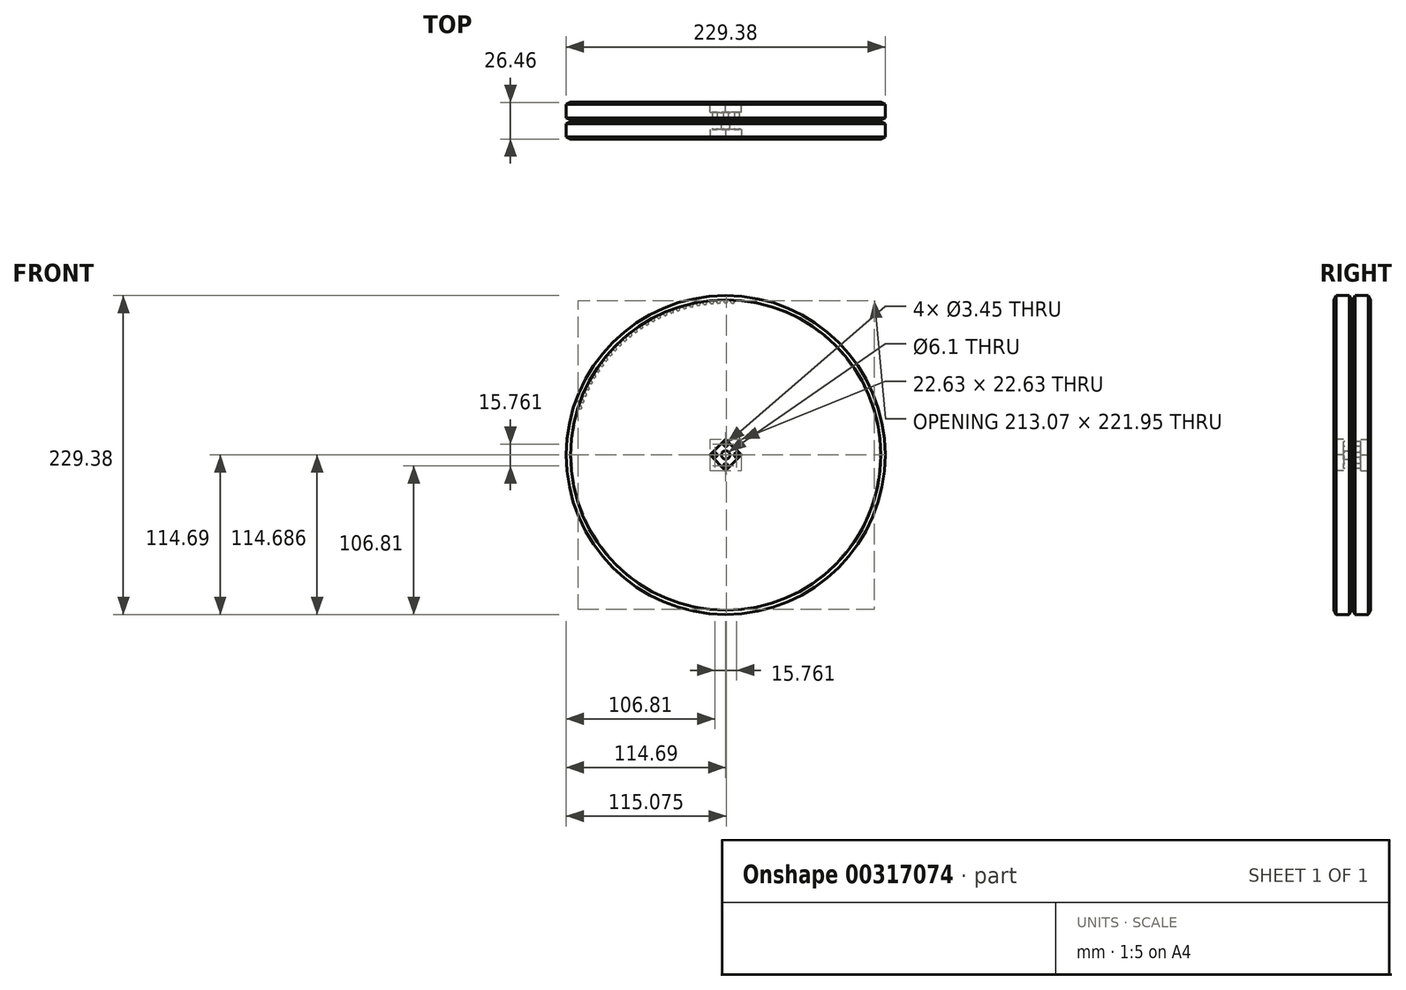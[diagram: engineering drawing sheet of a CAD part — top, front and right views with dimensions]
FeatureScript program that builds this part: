
annotation { "Feature Type Name" : "Feature", "Feature Type Description" : "" }
export const myFeature = defineFeature(function(context is Context, id is Id, definition is map)
    precondition{}
    {
        {
            var Q0;
            Q0=qCreatedBy(makeId("Front.planeOp"),FACE);
            var sketch = newSketch(context, id + "F0", { "sketchPlane" : qUnion([Q0])});
            skArc(sketch, "E0", {"start": v(-1.98, 110.97) * mm, "mid": v(-2.5, 110.96) * mm, "end": v(-3, 110.95) * mm});
            skArc(sketch, "E1", {"start": v(0.5, 109.19) * mm, "mid": v(0, 109.19) * mm, "end": v(-0.5, 109.19) * mm});
            skLineSegment(sketch, "E2", {"start": v(0, 0) * mm, "end": v(0, 109.19) * mm, "construction": true});
            skLineSegment(sketch, "E3", {"start": v(0.86, 109.42) * mm, "end": v(1.42, 110.62) * mm});
            skLineSegment(sketch, "E4", {"start": v(-0.86, 109.42) * mm, "end": v(-1.42, 110.62) * mm});
            skLineSegment(sketch, "E5", {"start": v(0, 109.19) * mm, "end": v(0, 110.99) * mm, "construction": true});
            skPoint(sketch, "E6.visualSharp", {"position": v(-1.59, 110.98) * mm});
            skArc(sketch, "E6.filletArc", {"start": v(-1.42, 110.62) * mm, "mid": v(-1.65, 110.88) * mm, "end": v(-1.98, 110.97) * mm});
            skPoint(sketch, "E7.visualSharp", {"position": v(1.59, 110.98) * mm});
            skArc(sketch, "E7.filletArc", {"start": v(1.98, 110.97) * mm, "mid": v(1.65, 110.88) * mm, "end": v(1.42, 110.62) * mm});
            skPoint(sketch, "E8.visualSharp", {"position": v(-0.75, 109.19) * mm});
            skArc(sketch, "E8.filletArc", {"start": v(-0.86, 109.42) * mm, "mid": v(-0.71, 109.25) * mm, "end": v(-0.5, 109.19) * mm});
            skPoint(sketch, "E9.visualSharp", {"position": v(0.75, 109.19) * mm});
            skArc(sketch, "E9.filletArc", {"start": v(0.5, 109.19) * mm, "mid": v(0.71, 109.25) * mm, "end": v(0.86, 109.42) * mm});
            skLineSegment(sketch, "E10.1.0", {"start": v(-4.9, 109.08) * mm, "end": v(-4.98, 110.88) * mm, "construction": true});
            skLineSegment(sketch, "E10.1.1", {"start": v(-5.77, 109.27) * mm, "end": v(-6.38, 110.45) * mm});
            skPoint(sketch, "E10.1.2", {"position": v(-6.56, 110.8) * mm});
            skPoint(sketch, "E10.1.3", {"position": v(-4.15, 109.1) * mm});
            skPoint(sketch, "E10.1.4", {"position": v(-5.65, 109.04) * mm});
            skPoint(sketch, "E10.1.5", {"position": v(-3.4, 110.94) * mm});
            skLineSegment(sketch, "E10.1.6", {"start": v(-4.05, 109.35) * mm, "end": v(-3.54, 110.58) * mm});
            skArc(sketch, "E10.1.7", {"start": v(-6.38, 110.45) * mm, "mid": v(-6.62, 110.7) * mm, "end": v(-6.95, 110.77) * mm});
            skArc(sketch, "E10.1.8", {"start": v(-3, 110.95) * mm, "mid": v(-3.33, 110.84) * mm, "end": v(-3.54, 110.58) * mm});
            skArc(sketch, "E10.1.9", {"start": v(-4.4, 109.1) * mm, "mid": v(-4.9, 109.08) * mm, "end": v(-5.4, 109.06) * mm});
            skArc(sketch, "E10.1.10", {"start": v(-4.4, 109.1) * mm, "mid": v(-4.2, 109.17) * mm, "end": v(-4.05, 109.35) * mm});
            skArc(sketch, "E10.1.11", {"start": v(-5.77, 109.27) * mm, "mid": v(-5.61, 109.1) * mm, "end": v(-5.4, 109.06) * mm});
            skLineSegment(sketch, "E10.2.0", {"start": v(-9.79, 108.75) * mm, "end": v(-9.95, 110.54) * mm, "construction": true});
            skLineSegment(sketch, "E10.2.1", {"start": v(-10.66, 108.9) * mm, "end": v(-11.33, 110.05) * mm});
            skPoint(sketch, "E10.2.2", {"position": v(-11.53, 110.39) * mm});
            skPoint(sketch, "E10.2.3", {"position": v(-9.04, 108.81) * mm});
            skPoint(sketch, "E10.2.4", {"position": v(-10.53, 108.68) * mm});
            skPoint(sketch, "E10.2.5", {"position": v(-8.37, 110.67) * mm});
            skLineSegment(sketch, "E10.2.6", {"start": v(-8.95, 109.05) * mm, "end": v(-8.5, 110.3) * mm});
            skArc(sketch, "E10.2.7", {"start": v(-11.33, 110.05) * mm, "mid": v(-11.58, 110.29) * mm, "end": v(-11.91, 110.35) * mm});
            skArc(sketch, "E10.2.8", {"start": v(-7.98, 110.7) * mm, "mid": v(-8.3, 110.58) * mm, "end": v(-8.5, 110.3) * mm});
            skArc(sketch, "E10.2.9", {"start": v(-9.3, 108.8) * mm, "mid": v(-9.79, 108.75) * mm, "end": v(-10.28, 108.7) * mm});
            skArc(sketch, "E10.2.10", {"start": v(-9.3, 108.8) * mm, "mid": v(-9.09, 108.87) * mm, "end": v(-8.95, 109.05) * mm});
            skArc(sketch, "E10.2.11", {"start": v(-10.66, 108.9) * mm, "mid": v(-10.5, 108.75) * mm, "end": v(-10.28, 108.7) * mm});
            skLineSegment(sketch, "E10.3.0", {"start": v(-14.66, 108.2) * mm, "end": v(-14.9, 109.98) * mm, "construction": true});
            skLineSegment(sketch, "E10.3.1", {"start": v(-15.54, 108.31) * mm, "end": v(-16.26, 109.43) * mm});
            skPoint(sketch, "E10.3.2", {"position": v(-16.47, 109.76) * mm});
            skPoint(sketch, "E10.3.3", {"position": v(-13.91, 108.3) * mm});
            skPoint(sketch, "E10.3.4", {"position": v(-15.4, 108.1) * mm});
            skPoint(sketch, "E10.3.5", {"position": v(-13.33, 110.19) * mm});
            skLineSegment(sketch, "E10.3.6", {"start": v(-13.84, 108.54) * mm, "end": v(-13.44, 109.81) * mm});
            skArc(sketch, "E10.3.7", {"start": v(-16.26, 109.43) * mm, "mid": v(-16.52, 109.66) * mm, "end": v(-16.85, 109.7) * mm});
            skArc(sketch, "E10.3.8", {"start": v(-12.94, 110.23) * mm, "mid": v(-13.25, 110.1) * mm, "end": v(-13.44, 109.81) * mm});
            skArc(sketch, "E10.3.9", {"start": v(-14.17, 108.27) * mm, "mid": v(-14.66, 108.2) * mm, "end": v(-15.15, 108.13) * mm});
            skArc(sketch, "E10.3.10", {"start": v(-14.17, 108.27) * mm, "mid": v(-13.96, 108.36) * mm, "end": v(-13.84, 108.54) * mm});
            skArc(sketch, "E10.3.11", {"start": v(-15.54, 108.31) * mm, "mid": v(-15.37, 108.17) * mm, "end": v(-15.15, 108.13) * mm});
            skLineSegment(sketch, "E10.4.0", {"start": v(-19.5, 107.43) * mm, "end": v(-19.82, 109.2) * mm, "construction": true});
            skLineSegment(sketch, "E10.4.1", {"start": v(-20.38, 107.5) * mm, "end": v(-21.15, 108.6) * mm});
            skPoint(sketch, "E10.4.2", {"position": v(-21.38, 108.91) * mm});
            skPoint(sketch, "E10.4.3", {"position": v(-18.76, 107.57) * mm});
            skPoint(sketch, "E10.4.4", {"position": v(-20.23, 107.3) * mm});
            skPoint(sketch, "E10.4.5", {"position": v(-18.26, 109.48) * mm});
            skLineSegment(sketch, "E10.4.6", {"start": v(-18.7, 107.81) * mm, "end": v(-18.35, 109.1) * mm});
            skArc(sketch, "E10.4.7", {"start": v(-21.15, 108.6) * mm, "mid": v(-21.42, 108.8) * mm, "end": v(-21.76, 108.83) * mm});
            skArc(sketch, "E10.4.8", {"start": v(-17.87, 109.54) * mm, "mid": v(-18.18, 109.4) * mm, "end": v(-18.35, 109.1) * mm});
            skArc(sketch, "E10.4.9", {"start": v(-19.01, 107.52) * mm, "mid": v(-19.5, 107.43) * mm, "end": v(-19.98, 107.34) * mm});
            skArc(sketch, "E10.4.10", {"start": v(-19.01, 107.52) * mm, "mid": v(-18.8, 107.62) * mm, "end": v(-18.7, 107.81) * mm});
            skArc(sketch, "E10.4.11", {"start": v(-20.38, 107.5) * mm, "mid": v(-20.2, 107.37) * mm, "end": v(-19.98, 107.34) * mm});
            skLineSegment(sketch, "E10.5.0", {"start": v(-24.3, 106.45) * mm, "end": v(-24.7, 108.2) * mm, "construction": true});
            skLineSegment(sketch, "E10.5.1", {"start": v(-25.18, 106.48) * mm, "end": v(-26, 107.53) * mm});
            skPoint(sketch, "E10.5.2", {"position": v(-26.24, 107.84) * mm});
            skPoint(sketch, "E10.5.3", {"position": v(-23.56, 106.62) * mm});
            skPoint(sketch, "E10.5.4", {"position": v(-25.03, 106.28) * mm});
            skPoint(sketch, "E10.5.5", {"position": v(-23.15, 108.55) * mm});
            skLineSegment(sketch, "E10.5.6", {"start": v(-23.51, 106.87) * mm, "end": v(-23.23, 108.17) * mm});
            skArc(sketch, "E10.5.7", {"start": v(-26, 107.53) * mm, "mid": v(-26.28, 107.73) * mm, "end": v(-26.62, 107.75) * mm});
            skArc(sketch, "E10.5.8", {"start": v(-22.77, 108.63) * mm, "mid": v(-23.07, 108.47) * mm, "end": v(-23.23, 108.17) * mm});
            skArc(sketch, "E10.5.9", {"start": v(-23.81, 106.56) * mm, "mid": v(-24.3, 106.45) * mm, "end": v(-24.78, 106.34) * mm});
            skArc(sketch, "E10.5.10", {"start": v(-23.81, 106.56) * mm, "mid": v(-23.62, 106.67) * mm, "end": v(-23.51, 106.87) * mm});
            skArc(sketch, "E10.5.11", {"start": v(-25.18, 106.48) * mm, "mid": v(-25, 106.35) * mm, "end": v(-24.78, 106.34) * mm});
            skLineSegment(sketch, "E10.6.0", {"start": v(-29.05, 105.25) * mm, "end": v(-29.53, 106.99) * mm, "construction": true});
            skLineSegment(sketch, "E10.6.1", {"start": v(-29.94, 105.25) * mm, "end": v(-30.8, 106.26) * mm});
            skPoint(sketch, "E10.6.2", {"position": v(-31.05, 106.56) * mm});
            skPoint(sketch, "E10.6.3", {"position": v(-28.32, 105.45) * mm});
            skPoint(sketch, "E10.6.4", {"position": v(-29.77, 105.05) * mm});
            skPoint(sketch, "E10.6.5", {"position": v(-28, 107.4) * mm});
            skLineSegment(sketch, "E10.6.6", {"start": v(-28.28, 105.7) * mm, "end": v(-28.06, 107.02) * mm});
            skArc(sketch, "E10.6.7", {"start": v(-30.8, 106.26) * mm, "mid": v(-31.09, 106.45) * mm, "end": v(-31.43, 106.45) * mm});
            skArc(sketch, "E10.6.8", {"start": v(-27.62, 107.5) * mm, "mid": v(-27.91, 107.32) * mm, "end": v(-28.06, 107.02) * mm});
            skArc(sketch, "E10.6.9", {"start": v(-28.57, 105.38) * mm, "mid": v(-29.05, 105.25) * mm, "end": v(-29.52, 105.12) * mm});
            skArc(sketch, "E10.6.10", {"start": v(-28.57, 105.38) * mm, "mid": v(-28.38, 105.5) * mm, "end": v(-28.28, 105.7) * mm});
            skArc(sketch, "E10.6.11", {"start": v(-29.94, 105.25) * mm, "mid": v(-29.75, 105.12) * mm, "end": v(-29.52, 105.12) * mm});
            skLineSegment(sketch, "E10.7.0", {"start": v(-33.74, 103.84) * mm, "end": v(-34.3, 105.56) * mm, "construction": true});
            skLineSegment(sketch, "E10.7.1", {"start": v(-34.63, 103.8) * mm, "end": v(-35.54, 104.77) * mm});
            skPoint(sketch, "E10.7.2", {"position": v(-35.8, 105.06) * mm});
            skPoint(sketch, "E10.7.3", {"position": v(-33.03, 104.07) * mm});
            skPoint(sketch, "E10.7.4", {"position": v(-34.45, 103.61) * mm});
            skPoint(sketch, "E10.7.5", {"position": v(-32.79, 106.04) * mm});
            skLineSegment(sketch, "E10.7.6", {"start": v(-33, 104.33) * mm, "end": v(-32.83, 105.65) * mm});
            skArc(sketch, "E10.7.7", {"start": v(-35.54, 104.77) * mm, "mid": v(-35.83, 104.94) * mm, "end": v(-36.17, 104.93) * mm});
            skArc(sketch, "E10.7.8", {"start": v(-32.41, 106.15) * mm, "mid": v(-32.7, 105.96) * mm, "end": v(-32.83, 105.65) * mm});
            skArc(sketch, "E10.7.9", {"start": v(-33.27, 104) * mm, "mid": v(-33.74, 103.84) * mm, "end": v(-34.21, 103.7) * mm});
            skArc(sketch, "E10.7.10", {"start": v(-33.27, 104) * mm, "mid": v(-33.08, 104.12) * mm, "end": v(-33, 104.33) * mm});
            skArc(sketch, "E10.7.11", {"start": v(-34.63, 103.8) * mm, "mid": v(-34.44, 103.68) * mm, "end": v(-34.21, 103.7) * mm});
            skLineSegment(sketch, "E10.8.0", {"start": v(-38.37, 102.23) * mm, "end": v(-39, 103.91) * mm, "construction": true});
            skLineSegment(sketch, "E10.8.1", {"start": v(-39.25, 102.14) * mm, "end": v(-40.2, 103.07) * mm});
            skPoint(sketch, "E10.8.2", {"position": v(-40.48, 103.34) * mm});
            skPoint(sketch, "E10.8.3", {"position": v(-37.66, 102.49) * mm});
            skPoint(sketch, "E10.8.4", {"position": v(-39.07, 101.96) * mm});
            skPoint(sketch, "E10.8.5", {"position": v(-37.51, 104.46) * mm});
            skLineSegment(sketch, "E10.8.6", {"start": v(-37.64, 102.74) * mm, "end": v(-37.54, 104.07) * mm});
            skArc(sketch, "E10.8.7", {"start": v(-40.2, 103.07) * mm, "mid": v(-40.5, 103.23) * mm, "end": v(-40.84, 103.2) * mm});
            skArc(sketch, "E10.8.8", {"start": v(-37.14, 104.59) * mm, "mid": v(-37.42, 104.39) * mm, "end": v(-37.54, 104.07) * mm});
            skArc(sketch, "E10.8.9", {"start": v(-37.9, 102.4) * mm, "mid": v(-38.37, 102.23) * mm, "end": v(-38.83, 102.05) * mm});
            skArc(sketch, "E10.8.10", {"start": v(-37.9, 102.4) * mm, "mid": v(-37.72, 102.53) * mm, "end": v(-37.64, 102.74) * mm});
            skArc(sketch, "E10.8.11", {"start": v(-39.25, 102.14) * mm, "mid": v(-39.05, 102.03) * mm, "end": v(-38.83, 102.05) * mm});
            skLineSegment(sketch, "E10.9.0", {"start": v(-42.91, 100.4) * mm, "end": v(-43.62, 102.06) * mm, "construction": true});
            skLineSegment(sketch, "E10.9.1", {"start": v(-43.8, 100.28) * mm, "end": v(-44.78, 101.16) * mm});
            skPoint(sketch, "E10.9.2", {"position": v(-45.07, 101.42) * mm});
            skPoint(sketch, "E10.9.3", {"position": v(-42.22, 100.7) * mm});
            skPoint(sketch, "E10.9.4", {"position": v(-43.6, 100.1) * mm});
            skPoint(sketch, "E10.9.5", {"position": v(-42.16, 102.67) * mm});
            skLineSegment(sketch, "E10.9.6", {"start": v(-42.21, 100.95) * mm, "end": v(-42.17, 102.28) * mm});
            skArc(sketch, "E10.9.7", {"start": v(-44.78, 101.16) * mm, "mid": v(-45.1, 101.3) * mm, "end": v(-45.43, 101.26) * mm});
            skArc(sketch, "E10.9.8", {"start": v(-41.8, 102.82) * mm, "mid": v(-42.06, 102.6) * mm, "end": v(-42.17, 102.28) * mm});
            skArc(sketch, "E10.9.9", {"start": v(-42.46, 100.6) * mm, "mid": v(-42.91, 100.4) * mm, "end": v(-43.37, 100.2) * mm});
            skArc(sketch, "E10.9.10", {"start": v(-42.46, 100.6) * mm, "mid": v(-42.28, 100.74) * mm, "end": v(-42.21, 100.95) * mm});
            skArc(sketch, "E10.9.11", {"start": v(-43.8, 100.28) * mm, "mid": v(-43.6, 100.18) * mm, "end": v(-43.37, 100.2) * mm});
            skLineSegment(sketch, "E10.10.0", {"start": v(-47.38, 98.38) * mm, "end": v(-48.16, 100) * mm, "construction": true});
            skLineSegment(sketch, "E10.10.1", {"start": v(-48.25, 98.21) * mm, "end": v(-49.28, 99.05) * mm});
            skPoint(sketch, "E10.10.2", {"position": v(-49.58, 99.3) * mm});
            skPoint(sketch, "E10.10.3", {"position": v(-46.7, 98.7) * mm});
            skPoint(sketch, "E10.10.4", {"position": v(-48.05, 98.05) * mm});
            skPoint(sketch, "E10.10.5", {"position": v(-46.72, 100.67) * mm});
            skLineSegment(sketch, "E10.10.6", {"start": v(-46.7, 98.95) * mm, "end": v(-46.72, 100.29) * mm});
            skArc(sketch, "E10.10.7", {"start": v(-49.28, 99.05) * mm, "mid": v(-49.6, 99.18) * mm, "end": v(-49.93, 99.12) * mm});
            skArc(sketch, "E10.10.8", {"start": v(-46.37, 100.84) * mm, "mid": v(-46.63, 100.61) * mm, "end": v(-46.72, 100.29) * mm});
            skArc(sketch, "E10.10.9", {"start": v(-46.93, 98.59) * mm, "mid": v(-47.38, 98.38) * mm, "end": v(-47.82, 98.16) * mm});
            skArc(sketch, "E10.10.10", {"start": v(-46.93, 98.59) * mm, "mid": v(-46.76, 98.74) * mm, "end": v(-46.7, 98.95) * mm});
            skArc(sketch, "E10.10.11", {"start": v(-48.25, 98.21) * mm, "mid": v(-48.04, 98.12) * mm, "end": v(-47.82, 98.16) * mm});
            skLineSegment(sketch, "E10.11.0", {"start": v(-51.74, 96.15) * mm, "end": v(-52.6, 97.74) * mm, "construction": true});
            skLineSegment(sketch, "E10.11.1", {"start": v(-52.6, 95.95) * mm, "end": v(-53.67, 96.74) * mm});
            skPoint(sketch, "E10.11.2", {"position": v(-53.98, 96.97) * mm});
            skPoint(sketch, "E10.11.3", {"position": v(-51.08, 96.5) * mm});
            skPoint(sketch, "E10.11.4", {"position": v(-52.4, 95.8) * mm});
            skPoint(sketch, "E10.11.5", {"position": v(-51.2, 98.48) * mm});
            skLineSegment(sketch, "E10.11.6", {"start": v(-51.1, 96.76) * mm, "end": v(-51.17, 98.09) * mm});
            skArc(sketch, "E10.11.7", {"start": v(-53.67, 96.74) * mm, "mid": v(-54, 96.86) * mm, "end": v(-54.33, 96.78) * mm});
            skArc(sketch, "E10.11.8", {"start": v(-50.85, 98.66) * mm, "mid": v(-51.1, 98.42) * mm, "end": v(-51.17, 98.09) * mm});
            skArc(sketch, "E10.11.9", {"start": v(-51.3, 96.38) * mm, "mid": v(-51.74, 96.15) * mm, "end": v(-52.18, 95.92) * mm});
            skArc(sketch, "E10.11.10", {"start": v(-51.3, 96.38) * mm, "mid": v(-51.14, 96.54) * mm, "end": v(-51.1, 96.76) * mm});
            skArc(sketch, "E10.11.11", {"start": v(-52.6, 95.95) * mm, "mid": v(-52.4, 95.87) * mm, "end": v(-52.18, 95.92) * mm});
            skLineSegment(sketch, "E10.12.0", {"start": v(-56, 93.73) * mm, "end": v(-56.93, 95.28) * mm, "construction": true});
            skLineSegment(sketch, "E10.12.1", {"start": v(-56.86, 93.49) * mm, "end": v(-57.96, 94.24) * mm});
            skPoint(sketch, "E10.12.2", {"position": v(-58.28, 94.46) * mm});
            skPoint(sketch, "E10.12.3", {"position": v(-55.36, 94.12) * mm});
            skPoint(sketch, "E10.12.4", {"position": v(-56.65, 93.35) * mm});
            skPoint(sketch, "E10.12.5", {"position": v(-55.56, 96.08) * mm});
            skLineSegment(sketch, "E10.12.6", {"start": v(-55.38, 94.37) * mm, "end": v(-55.52, 95.7) * mm});
            skArc(sketch, "E10.12.7", {"start": v(-57.96, 94.24) * mm, "mid": v(-58.28, 94.34) * mm, "end": v(-58.61, 94.25) * mm});
            skArc(sketch, "E10.12.8", {"start": v(-55.22, 96.28) * mm, "mid": v(-55.46, 96.03) * mm, "end": v(-55.52, 95.7) * mm});
            skArc(sketch, "E10.12.9", {"start": v(-55.58, 93.99) * mm, "mid": v(-56, 93.73) * mm, "end": v(-56.43, 93.48) * mm});
            skArc(sketch, "E10.12.10", {"start": v(-55.58, 93.99) * mm, "mid": v(-55.42, 94.15) * mm, "end": v(-55.38, 94.37) * mm});
            skArc(sketch, "E10.12.11", {"start": v(-56.86, 93.49) * mm, "mid": v(-56.64, 93.42) * mm, "end": v(-56.43, 93.48) * mm});
            skLineSegment(sketch, "E10.13.0", {"start": v(-60.15, 91.13) * mm, "end": v(-61.14, 92.63) * mm, "construction": true});
            skLineSegment(sketch, "E10.13.1", {"start": v(-61, 90.84) * mm, "end": v(-62.13, 91.54) * mm});
            skPoint(sketch, "E10.13.2", {"position": v(-62.46, 91.75) * mm});
            skPoint(sketch, "E10.13.3", {"position": v(-59.52, 91.54) * mm});
            skPoint(sketch, "E10.13.4", {"position": v(-60.78, 90.71) * mm});
            skPoint(sketch, "E10.13.5", {"position": v(-59.81, 93.5) * mm});
            skLineSegment(sketch, "E10.13.6", {"start": v(-59.56, 91.8) * mm, "end": v(-59.76, 93.1) * mm});
            skArc(sketch, "E10.13.7", {"start": v(-62.13, 91.54) * mm, "mid": v(-62.46, 91.63) * mm, "end": v(-62.78, 91.53) * mm});
            skArc(sketch, "E10.13.8", {"start": v(-59.49, 93.7) * mm, "mid": v(-59.7, 93.44) * mm, "end": v(-59.76, 93.1) * mm});
            skArc(sketch, "E10.13.9", {"start": v(-59.74, 91.4) * mm, "mid": v(-60.15, 91.13) * mm, "end": v(-60.56, 90.85) * mm});
            skArc(sketch, "E10.13.10", {"start": v(-59.74, 91.4) * mm, "mid": v(-59.6, 91.57) * mm, "end": v(-59.56, 91.8) * mm});
            skArc(sketch, "E10.13.11", {"start": v(-61, 90.84) * mm, "mid": v(-60.78, 90.79) * mm, "end": v(-60.56, 90.85) * mm});
            skLineSegment(sketch, "E10.14.0", {"start": v(-64.18, 88.34) * mm, "end": v(-65.24, 89.8) * mm, "construction": true});
            skLineSegment(sketch, "E10.14.1", {"start": v(-65, 88.02) * mm, "end": v(-66.17, 88.66) * mm});
            skPoint(sketch, "E10.14.2", {"position": v(-66.51, 88.85) * mm});
            skPoint(sketch, "E10.14.3", {"position": v(-63.57, 88.77) * mm});
            skPoint(sketch, "E10.14.4", {"position": v(-64.78, 87.9) * mm});
            skPoint(sketch, "E10.14.5", {"position": v(-63.95, 90.71) * mm});
            skLineSegment(sketch, "E10.14.6", {"start": v(-63.62, 89.03) * mm, "end": v(-63.87, 90.33) * mm});
            skArc(sketch, "E10.14.7", {"start": v(-66.17, 88.66) * mm, "mid": v(-66.5, 88.74) * mm, "end": v(-66.83, 88.62) * mm});
            skArc(sketch, "E10.14.8", {"start": v(-63.63, 90.94) * mm, "mid": v(-63.84, 90.67) * mm, "end": v(-63.87, 90.33) * mm});
            skArc(sketch, "E10.14.9", {"start": v(-63.78, 88.62) * mm, "mid": v(-64.18, 88.34) * mm, "end": v(-64.58, 88.04) * mm});
            skArc(sketch, "E10.14.10", {"start": v(-63.78, 88.62) * mm, "mid": v(-63.64, 88.8) * mm, "end": v(-63.62, 89.03) * mm});
            skArc(sketch, "E10.14.11", {"start": v(-65, 88.02) * mm, "mid": v(-64.79, 87.97) * mm, "end": v(-64.58, 88.04) * mm});
            skLineSegment(sketch, "E10.15.0", {"start": v(-68.08, 85.37) * mm, "end": v(-69.2, 86.77) * mm, "construction": true});
            skLineSegment(sketch, "E10.15.1", {"start": v(-68.9, 85.01) * mm, "end": v(-70.08, 85.6) * mm});
            skPoint(sketch, "E10.15.2", {"position": v(-70.43, 85.78) * mm});
            skPoint(sketch, "E10.15.3", {"position": v(-67.49, 85.83) * mm});
            skPoint(sketch, "E10.15.4", {"position": v(-68.66, 84.9) * mm});
            skPoint(sketch, "E10.15.5", {"position": v(-67.95, 87.75) * mm});
            skLineSegment(sketch, "E10.15.6", {"start": v(-67.55, 86.08) * mm, "end": v(-67.86, 87.38) * mm});
            skArc(sketch, "E10.15.7", {"start": v(-70.08, 85.6) * mm, "mid": v(-70.42, 85.66) * mm, "end": v(-70.73, 85.53) * mm});
            skArc(sketch, "E10.15.8", {"start": v(-67.64, 88) * mm, "mid": v(-67.85, 87.72) * mm, "end": v(-67.86, 87.38) * mm});
            skArc(sketch, "E10.15.9", {"start": v(-67.7, 85.67) * mm, "mid": v(-68.08, 85.37) * mm, "end": v(-68.46, 85.06) * mm});
            skArc(sketch, "E10.15.10", {"start": v(-67.7, 85.67) * mm, "mid": v(-67.56, 85.86) * mm, "end": v(-67.55, 86.08) * mm});
            skArc(sketch, "E10.15.11", {"start": v(-68.9, 85.01) * mm, "mid": v(-68.67, 84.97) * mm, "end": v(-68.46, 85.06) * mm});
            skArc(sketch, "E11.trimOffspring", {"start": v(3, 110.95) * mm, "mid": v(2.5, 110.96) * mm, "end": v(1.98, 110.97) * mm});
            skArc(sketch, "E12.trimOffspring", {"start": v(-66.83, 88.62) * mm, "mid": v(-67.24, 88.3) * mm, "end": v(-67.64, 88) * mm});
            skArc(sketch, "E13.trimOffspring", {"start": v(-62.78, 91.53) * mm, "mid": v(-63.2, 91.23) * mm, "end": v(-63.63, 90.94) * mm});
            skArc(sketch, "E14.trimOffspring", {"start": v(-58.61, 94.25) * mm, "mid": v(-59.05, 93.98) * mm, "end": v(-59.49, 93.7) * mm});
            skArc(sketch, "E15.trimOffspring", {"start": v(-54.33, 96.78) * mm, "mid": v(-54.77, 96.53) * mm, "end": v(-55.22, 96.28) * mm});
            skArc(sketch, "E16.trimOffspring", {"start": v(-49.93, 99.12) * mm, "mid": v(-50.39, 98.9) * mm, "end": v(-50.85, 98.66) * mm});
            skArc(sketch, "E17.trimOffspring", {"start": v(-45.43, 101.26) * mm, "mid": v(-45.9, 101.05) * mm, "end": v(-46.37, 100.84) * mm});
            skArc(sketch, "E18.trimOffspring", {"start": v(-40.84, 103.2) * mm, "mid": v(-41.32, 103.01) * mm, "end": v(-41.8, 102.82) * mm});
            skArc(sketch, "E19.trimOffspring", {"start": v(-36.17, 104.93) * mm, "mid": v(-36.66, 104.76) * mm, "end": v(-37.14, 104.59) * mm});
            skArc(sketch, "E20.trimOffspring", {"start": v(-31.43, 106.45) * mm, "mid": v(-31.92, 106.3) * mm, "end": v(-32.41, 106.15) * mm});
            skArc(sketch, "E21.trimOffspring", {"start": v(-26.62, 107.75) * mm, "mid": v(-27.12, 107.62) * mm, "end": v(-27.62, 107.5) * mm});
            skArc(sketch, "E22.trimOffspring", {"start": v(-21.76, 108.83) * mm, "mid": v(-22.26, 108.73) * mm, "end": v(-22.77, 108.63) * mm});
            skArc(sketch, "E23.trimOffspring", {"start": v(-16.85, 109.7) * mm, "mid": v(-17.36, 109.62) * mm, "end": v(-17.87, 109.54) * mm});
            skArc(sketch, "E24.trimOffspring", {"start": v(-11.91, 110.35) * mm, "mid": v(-12.43, 110.3) * mm, "end": v(-12.94, 110.23) * mm});
            skArc(sketch, "E25.trimOffspring", {"start": v(-6.95, 110.77) * mm, "mid": v(-7.47, 110.74) * mm, "end": v(-7.98, 110.7) * mm});
            skArc(sketch, "E26", {"start": v(-70.73, 85.53) * mm, "mid": v(-71.13, 85.2) * mm, "end": v(-71.52, 84.87) * mm, "construction": true});
            skCircle(sketch, "E27", {"center": v(0, 0) * mm, "radius": 109.19 * mm, "construction": true});
            skCircle(sketch, "E28", {"center": v(0, 0) * mm, "radius": 111.42 * mm, "construction": true});
            skLineSegment(sketch, "E29", {"start": v(0, 110.99) * mm, "end": v(0, 111.42) * mm, "construction": true});
            skLineSegment(sketch, "E30", {"start": v(4.98, 110.88) * mm, "end": v(5, 111.3) * mm, "construction": true});
            skLineSegment(sketch, "E31.3.16.0", {"start": v(-72.64, 81.84) * mm, "end": v(-73.85, 82.37) * mm});
            skPoint(sketch, "E31.6.16.0", {"position": v(-74.21, 82.53) * mm});
            skPoint(sketch, "E31.7.16.0", {"position": v(-71.27, 82.72) * mm});
            skPoint(sketch, "E31.8.16.0", {"position": v(-72.4, 81.73) * mm});
            skPoint(sketch, "E31.9.16.0", {"position": v(-71.82, 84.62) * mm});
            skLineSegment(sketch, "E31.10.16.0", {"start": v(-71.34, 82.96) * mm, "end": v(-71.71, 84.24) * mm});
            skArc(sketch, "E31.13.16.0", {"start": v(-73.85, 82.37) * mm, "mid": v(-74.2, 82.42) * mm, "end": v(-74.5, 82.27) * mm});
            skLineSegment(sketch, "E31.14.16.0", {"start": v(-71.84, 82.23) * mm, "end": v(-73.02, 83.58) * mm, "construction": true});
            skArc(sketch, "E31.17.16.0", {"start": v(-71.52, 84.87) * mm, "mid": v(-71.71, 84.58) * mm, "end": v(-71.71, 84.24) * mm});
            skArc(sketch, "E31.21.16.0", {"start": v(-71.47, 82.55) * mm, "mid": v(-71.84, 82.23) * mm, "end": v(-72.21, 81.9) * mm});
            skArc(sketch, "E31.25.16.0", {"start": v(-71.47, 82.55) * mm, "mid": v(-71.34, 82.74) * mm, "end": v(-71.34, 82.96) * mm});
            skArc(sketch, "E31.29.16.0", {"start": v(-72.64, 81.84) * mm, "mid": v(-72.41, 81.8) * mm, "end": v(-72.21, 81.9) * mm});
            skLineSegment(sketch, "E31.3.17.0", {"start": v(-76.24, 78.5) * mm, "end": v(-77.48, 78.98) * mm});
            skPoint(sketch, "E31.6.17.0", {"position": v(-77.84, 79.12) * mm});
            skPoint(sketch, "E31.7.17.0", {"position": v(-74.91, 79.44) * mm});
            skPoint(sketch, "E31.8.17.0", {"position": v(-76, 78.4) * mm});
            skPoint(sketch, "E31.9.17.0", {"position": v(-75.55, 81.3) * mm});
            skLineSegment(sketch, "E31.10.17.0", {"start": v(-75, 79.68) * mm, "end": v(-75.42, 80.94) * mm});
            skArc(sketch, "E31.13.17.0", {"start": v(-77.48, 78.98) * mm, "mid": v(-77.82, 79) * mm, "end": v(-78.12, 78.84) * mm});
            skLineSegment(sketch, "E31.14.17.0", {"start": v(-75.46, 78.92) * mm, "end": v(-76.7, 80.22) * mm, "construction": true});
            skArc(sketch, "E31.17.17.0", {"start": v(-75.26, 81.57) * mm, "mid": v(-75.43, 81.28) * mm, "end": v(-75.42, 80.94) * mm});
            skArc(sketch, "E31.21.17.0", {"start": v(-75.1, 79.26) * mm, "mid": v(-75.46, 78.92) * mm, "end": v(-75.81, 78.58) * mm});
            skArc(sketch, "E31.25.17.0", {"start": v(-75.1, 79.26) * mm, "mid": v(-74.99, 79.46) * mm, "end": v(-75, 79.68) * mm});
            skArc(sketch, "E31.29.17.0", {"start": v(-76.24, 78.5) * mm, "mid": v(-76.01, 78.47) * mm, "end": v(-75.81, 78.58) * mm});
            skLineSegment(sketch, "E31.3.18.0", {"start": v(-79.68, 75) * mm, "end": v(-80.94, 75.42) * mm});
            skPoint(sketch, "E31.6.18.0", {"position": v(-81.3, 75.55) * mm});
            skPoint(sketch, "E31.7.18.0", {"position": v(-78.4, 76) * mm});
            skPoint(sketch, "E31.8.18.0", {"position": v(-79.44, 74.91) * mm});
            skPoint(sketch, "E31.9.18.0", {"position": v(-79.12, 77.84) * mm});
            skLineSegment(sketch, "E31.10.18.0", {"start": v(-78.5, 76.24) * mm, "end": v(-78.98, 77.48) * mm});
            skArc(sketch, "E31.13.18.0", {"start": v(-80.94, 75.42) * mm, "mid": v(-81.28, 75.43) * mm, "end": v(-81.57, 75.26) * mm});
            skLineSegment(sketch, "E31.14.18.0", {"start": v(-78.92, 75.46) * mm, "end": v(-80.22, 76.7) * mm, "construction": true});
            skArc(sketch, "E31.17.18.0", {"start": v(-78.84, 78.12) * mm, "mid": v(-79, 77.82) * mm, "end": v(-78.98, 77.48) * mm});
            skArc(sketch, "E31.21.18.0", {"start": v(-78.58, 75.81) * mm, "mid": v(-78.92, 75.46) * mm, "end": v(-79.26, 75.1) * mm});
            skArc(sketch, "E31.25.18.0", {"start": v(-78.58, 75.81) * mm, "mid": v(-78.47, 76.01) * mm, "end": v(-78.5, 76.24) * mm});
            skArc(sketch, "E31.29.18.0", {"start": v(-79.68, 75) * mm, "mid": v(-79.46, 74.99) * mm, "end": v(-79.26, 75.1) * mm});
            skArc(sketch, "E32.trimOffspring", {"start": v(-74.5, 82.27) * mm, "mid": v(-74.88, 81.92) * mm, "end": v(-75.26, 81.57) * mm, "construction": true});
            skArc(sketch, "E33.trimOffspring", {"start": v(-70.73, 85.53) * mm, "mid": v(-71.13, 85.2) * mm, "end": v(-71.52, 84.87) * mm});
            skArc(sketch, "E34.trimOffspring", {"start": v(-74.5, 82.27) * mm, "mid": v(-74.88, 81.92) * mm, "end": v(-75.26, 81.57) * mm});
            skArc(sketch, "E35.trimOffspring", {"start": v(-78.12, 78.84) * mm, "mid": v(-78.62, 78.34) * mm, "end": v(-79.12, 77.84) * mm, "construction": true});
            skArc(sketch, "E36.trimOffspring", {"start": v(-78.12, 78.84) * mm, "mid": v(-78.62, 78.34) * mm, "end": v(-79.12, 77.84) * mm});
            skLineSegment(sketch, "E37.3.19.0", {"start": v(-82.96, 71.34) * mm, "end": v(-84.24, 71.71) * mm});
            skPoint(sketch, "E37.6.19.0", {"position": v(-84.62, 71.82) * mm});
            skPoint(sketch, "E37.7.19.0", {"position": v(-81.73, 72.4) * mm});
            skPoint(sketch, "E37.8.19.0", {"position": v(-82.72, 71.27) * mm});
            skPoint(sketch, "E37.9.19.0", {"position": v(-82.53, 74.21) * mm});
            skLineSegment(sketch, "E37.10.19.0", {"start": v(-81.84, 72.64) * mm, "end": v(-82.37, 73.85) * mm});
            skArc(sketch, "E37.13.19.0", {"start": v(-84.24, 71.71) * mm, "mid": v(-84.58, 71.71) * mm, "end": v(-84.87, 71.52) * mm});
            skLineSegment(sketch, "E37.14.19.0", {"start": v(-82.23, 71.84) * mm, "end": v(-83.58, 73.02) * mm, "construction": true});
            skArc(sketch, "E37.17.19.0", {"start": v(-82.27, 74.5) * mm, "mid": v(-82.42, 74.2) * mm, "end": v(-82.37, 73.85) * mm});
            skArc(sketch, "E37.21.19.0", {"start": v(-81.9, 72.21) * mm, "mid": v(-82.23, 71.84) * mm, "end": v(-82.55, 71.47) * mm});
            skArc(sketch, "E37.25.19.0", {"start": v(-81.9, 72.21) * mm, "mid": v(-81.8, 72.41) * mm, "end": v(-81.84, 72.64) * mm});
            skArc(sketch, "E37.29.19.0", {"start": v(-82.96, 71.34) * mm, "mid": v(-82.74, 71.34) * mm, "end": v(-82.55, 71.47) * mm});
            skLineSegment(sketch, "E37.3.20.0", {"start": v(-86.08, 67.55) * mm, "end": v(-87.38, 67.86) * mm});
            skPoint(sketch, "E37.6.20.0", {"position": v(-87.75, 67.95) * mm});
            skPoint(sketch, "E37.7.20.0", {"position": v(-84.9, 68.66) * mm});
            skPoint(sketch, "E37.8.20.0", {"position": v(-85.83, 67.49) * mm});
            skPoint(sketch, "E37.9.20.0", {"position": v(-85.78, 70.43) * mm});
            skLineSegment(sketch, "E37.10.20.0", {"start": v(-85.01, 68.9) * mm, "end": v(-85.6, 70.08) * mm});
            skArc(sketch, "E37.13.20.0", {"start": v(-87.38, 67.86) * mm, "mid": v(-87.72, 67.85) * mm, "end": v(-88, 67.64) * mm});
            skLineSegment(sketch, "E37.14.20.0", {"start": v(-85.37, 68.08) * mm, "end": v(-86.77, 69.2) * mm, "construction": true});
            skArc(sketch, "E37.17.20.0", {"start": v(-85.53, 70.73) * mm, "mid": v(-85.66, 70.42) * mm, "end": v(-85.6, 70.08) * mm});
            skArc(sketch, "E37.21.20.0", {"start": v(-85.06, 68.46) * mm, "mid": v(-85.37, 68.08) * mm, "end": v(-85.67, 67.7) * mm});
            skArc(sketch, "E37.25.20.0", {"start": v(-85.06, 68.46) * mm, "mid": v(-84.97, 68.67) * mm, "end": v(-85.01, 68.9) * mm});
            skArc(sketch, "E37.29.20.0", {"start": v(-86.08, 67.55) * mm, "mid": v(-85.86, 67.56) * mm, "end": v(-85.67, 67.7) * mm});
            skLineSegment(sketch, "E37.3.21.0", {"start": v(-89.03, 63.62) * mm, "end": v(-90.33, 63.87) * mm});
            skPoint(sketch, "E37.6.21.0", {"position": v(-90.71, 63.95) * mm});
            skPoint(sketch, "E37.7.21.0", {"position": v(-87.9, 64.78) * mm});
            skPoint(sketch, "E37.8.21.0", {"position": v(-88.77, 63.57) * mm});
            skPoint(sketch, "E37.9.21.0", {"position": v(-88.85, 66.51) * mm});
            skLineSegment(sketch, "E37.10.21.0", {"start": v(-88.02, 65) * mm, "end": v(-88.66, 66.17) * mm});
            skArc(sketch, "E37.13.21.0", {"start": v(-90.33, 63.87) * mm, "mid": v(-90.67, 63.84) * mm, "end": v(-90.94, 63.63) * mm});
            skLineSegment(sketch, "E37.14.21.0", {"start": v(-88.34, 64.18) * mm, "end": v(-89.8, 65.24) * mm, "construction": true});
            skArc(sketch, "E37.17.21.0", {"start": v(-88.62, 66.83) * mm, "mid": v(-88.74, 66.5) * mm, "end": v(-88.66, 66.17) * mm});
            skArc(sketch, "E37.21.21.0", {"start": v(-88.04, 64.58) * mm, "mid": v(-88.34, 64.18) * mm, "end": v(-88.62, 63.78) * mm});
            skArc(sketch, "E37.25.21.0", {"start": v(-88.04, 64.58) * mm, "mid": v(-87.97, 64.79) * mm, "end": v(-88.02, 65) * mm});
            skArc(sketch, "E37.29.21.0", {"start": v(-89.03, 63.62) * mm, "mid": v(-88.8, 63.64) * mm, "end": v(-88.62, 63.78) * mm});
            skLineSegment(sketch, "E37.3.22.0", {"start": v(-91.8, 59.56) * mm, "end": v(-93.1, 59.76) * mm});
            skPoint(sketch, "E37.6.22.0", {"position": v(-93.5, 59.81) * mm});
            skPoint(sketch, "E37.7.22.0", {"position": v(-90.71, 60.78) * mm});
            skPoint(sketch, "E37.8.22.0", {"position": v(-91.54, 59.52) * mm});
            skPoint(sketch, "E37.9.22.0", {"position": v(-91.75, 62.46) * mm});
            skLineSegment(sketch, "E37.10.22.0", {"start": v(-90.84, 61) * mm, "end": v(-91.54, 62.13) * mm});
            skArc(sketch, "E37.13.22.0", {"start": v(-93.1, 59.76) * mm, "mid": v(-93.44, 59.7) * mm, "end": v(-93.7, 59.49) * mm});
            skLineSegment(sketch, "E37.14.22.0", {"start": v(-91.13, 60.15) * mm, "end": v(-92.63, 61.14) * mm, "construction": true});
            skArc(sketch, "E37.17.22.0", {"start": v(-91.53, 62.78) * mm, "mid": v(-91.63, 62.46) * mm, "end": v(-91.54, 62.13) * mm});
            skArc(sketch, "E37.21.22.0", {"start": v(-90.85, 60.56) * mm, "mid": v(-91.13, 60.15) * mm, "end": v(-91.4, 59.74) * mm});
            skArc(sketch, "E37.25.22.0", {"start": v(-90.85, 60.56) * mm, "mid": v(-90.79, 60.78) * mm, "end": v(-90.84, 61) * mm});
            skArc(sketch, "E37.29.22.0", {"start": v(-91.8, 59.56) * mm, "mid": v(-91.57, 59.6) * mm, "end": v(-91.4, 59.74) * mm});
            skLineSegment(sketch, "E37.3.23.0", {"start": v(-94.37, 55.38) * mm, "end": v(-95.7, 55.52) * mm});
            skPoint(sketch, "E37.6.23.0", {"position": v(-96.08, 55.56) * mm});
            skPoint(sketch, "E37.7.23.0", {"position": v(-93.35, 56.65) * mm});
            skPoint(sketch, "E37.8.23.0", {"position": v(-94.12, 55.36) * mm});
            skPoint(sketch, "E37.9.23.0", {"position": v(-94.46, 58.28) * mm});
            skLineSegment(sketch, "E37.10.23.0", {"start": v(-93.49, 56.86) * mm, "end": v(-94.24, 57.96) * mm});
            skArc(sketch, "E37.13.23.0", {"start": v(-95.7, 55.52) * mm, "mid": v(-96.03, 55.46) * mm, "end": v(-96.28, 55.22) * mm});
            skLineSegment(sketch, "E37.14.23.0", {"start": v(-93.73, 56) * mm, "end": v(-95.28, 56.93) * mm, "construction": true});
            skArc(sketch, "E37.17.23.0", {"start": v(-94.25, 58.61) * mm, "mid": v(-94.34, 58.28) * mm, "end": v(-94.24, 57.96) * mm});
            skArc(sketch, "E37.21.23.0", {"start": v(-93.48, 56.43) * mm, "mid": v(-93.73, 56) * mm, "end": v(-93.99, 55.58) * mm});
            skArc(sketch, "E37.25.23.0", {"start": v(-93.48, 56.43) * mm, "mid": v(-93.42, 56.64) * mm, "end": v(-93.49, 56.86) * mm});
            skArc(sketch, "E37.29.23.0", {"start": v(-94.37, 55.38) * mm, "mid": v(-94.15, 55.42) * mm, "end": v(-93.99, 55.58) * mm});
            skLineSegment(sketch, "E37.3.24.0", {"start": v(-96.76, 51.1) * mm, "end": v(-98.09, 51.17) * mm});
            skPoint(sketch, "E37.6.24.0", {"position": v(-98.48, 51.2) * mm});
            skPoint(sketch, "E37.7.24.0", {"position": v(-95.8, 52.4) * mm});
            skPoint(sketch, "E37.8.24.0", {"position": v(-96.5, 51.08) * mm});
            skPoint(sketch, "E37.9.24.0", {"position": v(-96.97, 53.98) * mm});
            skLineSegment(sketch, "E37.10.24.0", {"start": v(-95.95, 52.6) * mm, "end": v(-96.74, 53.67) * mm});
            skArc(sketch, "E37.13.24.0", {"start": v(-98.09, 51.17) * mm, "mid": v(-98.42, 51.1) * mm, "end": v(-98.66, 50.85) * mm});
            skLineSegment(sketch, "E37.14.24.0", {"start": v(-96.15, 51.74) * mm, "end": v(-97.74, 52.6) * mm, "construction": true});
            skArc(sketch, "E37.17.24.0", {"start": v(-96.78, 54.33) * mm, "mid": v(-96.86, 54) * mm, "end": v(-96.74, 53.67) * mm});
            skArc(sketch, "E37.21.24.0", {"start": v(-95.92, 52.18) * mm, "mid": v(-96.15, 51.74) * mm, "end": v(-96.38, 51.3) * mm});
            skArc(sketch, "E37.25.24.0", {"start": v(-95.92, 52.18) * mm, "mid": v(-95.87, 52.4) * mm, "end": v(-95.95, 52.6) * mm});
            skArc(sketch, "E37.29.24.0", {"start": v(-96.76, 51.1) * mm, "mid": v(-96.54, 51.14) * mm, "end": v(-96.38, 51.3) * mm});
            skLineSegment(sketch, "E38.3.25.0", {"start": v(-98.95, 46.7) * mm, "end": v(-100.29, 46.72) * mm});
            skPoint(sketch, "E38.6.25.0", {"position": v(-100.67, 46.72) * mm});
            skPoint(sketch, "E38.7.25.0", {"position": v(-98.05, 48.05) * mm});
            skPoint(sketch, "E38.8.25.0", {"position": v(-98.7, 46.7) * mm});
            skPoint(sketch, "E38.9.25.0", {"position": v(-99.3, 49.58) * mm});
            skLineSegment(sketch, "E38.10.25.0", {"start": v(-98.21, 48.25) * mm, "end": v(-99.05, 49.28) * mm});
            skArc(sketch, "E38.13.25.0", {"start": v(-100.29, 46.72) * mm, "mid": v(-100.61, 46.63) * mm, "end": v(-100.84, 46.37) * mm});
            skLineSegment(sketch, "E38.14.25.0", {"start": v(-98.38, 47.38) * mm, "end": v(-100, 48.16) * mm, "construction": true});
            skArc(sketch, "E38.17.25.0", {"start": v(-99.12, 49.93) * mm, "mid": v(-99.18, 49.6) * mm, "end": v(-99.05, 49.28) * mm});
            skArc(sketch, "E38.21.25.0", {"start": v(-98.16, 47.82) * mm, "mid": v(-98.38, 47.38) * mm, "end": v(-98.59, 46.93) * mm});
            skArc(sketch, "E38.25.25.0", {"start": v(-98.16, 47.82) * mm, "mid": v(-98.12, 48.04) * mm, "end": v(-98.21, 48.25) * mm});
            skArc(sketch, "E38.29.25.0", {"start": v(-98.95, 46.7) * mm, "mid": v(-98.74, 46.76) * mm, "end": v(-98.59, 46.93) * mm});
            skLineSegment(sketch, "E38.3.26.0", {"start": v(-100.95, 42.21) * mm, "end": v(-102.28, 42.17) * mm});
            skPoint(sketch, "E38.6.26.0", {"position": v(-102.67, 42.16) * mm});
            skPoint(sketch, "E38.7.26.0", {"position": v(-100.1, 43.6) * mm});
            skPoint(sketch, "E38.8.26.0", {"position": v(-100.7, 42.22) * mm});
            skPoint(sketch, "E38.9.26.0", {"position": v(-101.42, 45.07) * mm});
            skLineSegment(sketch, "E38.10.26.0", {"start": v(-100.28, 43.8) * mm, "end": v(-101.16, 44.78) * mm});
            skArc(sketch, "E38.13.26.0", {"start": v(-102.28, 42.17) * mm, "mid": v(-102.6, 42.06) * mm, "end": v(-102.82, 41.8) * mm});
            skLineSegment(sketch, "E38.14.26.0", {"start": v(-100.4, 42.91) * mm, "end": v(-102.06, 43.62) * mm, "construction": true});
            skArc(sketch, "E38.17.26.0", {"start": v(-101.26, 45.43) * mm, "mid": v(-101.3, 45.1) * mm, "end": v(-101.16, 44.78) * mm});
            skArc(sketch, "E38.21.26.0", {"start": v(-100.2, 43.37) * mm, "mid": v(-100.4, 42.91) * mm, "end": v(-100.6, 42.46) * mm});
            skArc(sketch, "E38.25.26.0", {"start": v(-100.2, 43.37) * mm, "mid": v(-100.18, 43.6) * mm, "end": v(-100.28, 43.8) * mm});
            skArc(sketch, "E38.29.26.0", {"start": v(-100.95, 42.21) * mm, "mid": v(-100.74, 42.28) * mm, "end": v(-100.6, 42.46) * mm});
            skLineSegment(sketch, "E38.3.27.0", {"start": v(-102.74, 37.64) * mm, "end": v(-104.07, 37.54) * mm});
            skPoint(sketch, "E38.6.27.0", {"position": v(-104.46, 37.51) * mm});
            skPoint(sketch, "E38.7.27.0", {"position": v(-101.96, 39.07) * mm});
            skPoint(sketch, "E38.8.27.0", {"position": v(-102.49, 37.66) * mm});
            skPoint(sketch, "E38.9.27.0", {"position": v(-103.34, 40.48) * mm});
            skLineSegment(sketch, "E38.10.27.0", {"start": v(-102.14, 39.25) * mm, "end": v(-103.07, 40.2) * mm});
            skArc(sketch, "E38.13.27.0", {"start": v(-104.07, 37.54) * mm, "mid": v(-104.39, 37.42) * mm, "end": v(-104.59, 37.14) * mm});
            skLineSegment(sketch, "E38.14.27.0", {"start": v(-102.23, 38.37) * mm, "end": v(-103.91, 39) * mm, "construction": true});
            skArc(sketch, "E38.17.27.0", {"start": v(-103.2, 40.84) * mm, "mid": v(-103.23, 40.5) * mm, "end": v(-103.07, 40.2) * mm});
            skArc(sketch, "E38.21.27.0", {"start": v(-102.05, 38.83) * mm, "mid": v(-102.23, 38.37) * mm, "end": v(-102.4, 37.9) * mm});
            skArc(sketch, "E38.25.27.0", {"start": v(-102.05, 38.83) * mm, "mid": v(-102.03, 39.05) * mm, "end": v(-102.14, 39.25) * mm});
            skArc(sketch, "E38.29.27.0", {"start": v(-102.74, 37.64) * mm, "mid": v(-102.53, 37.72) * mm, "end": v(-102.4, 37.9) * mm});
            skLineSegment(sketch, "E38.3.28.0", {"start": v(-104.33, 33) * mm, "end": v(-105.65, 32.83) * mm});
            skPoint(sketch, "E38.6.28.0", {"position": v(-106.04, 32.79) * mm});
            skPoint(sketch, "E38.7.28.0", {"position": v(-103.61, 34.45) * mm});
            skPoint(sketch, "E38.8.28.0", {"position": v(-104.07, 33.03) * mm});
            skPoint(sketch, "E38.9.28.0", {"position": v(-105.06, 35.8) * mm});
            skLineSegment(sketch, "E38.10.28.0", {"start": v(-103.8, 34.63) * mm, "end": v(-104.77, 35.54) * mm});
            skArc(sketch, "E38.13.28.0", {"start": v(-105.65, 32.83) * mm, "mid": v(-105.96, 32.7) * mm, "end": v(-106.15, 32.41) * mm});
            skLineSegment(sketch, "E38.14.28.0", {"start": v(-103.84, 33.74) * mm, "end": v(-105.56, 34.3) * mm, "construction": true});
            skArc(sketch, "E38.17.28.0", {"start": v(-104.93, 36.17) * mm, "mid": v(-104.94, 35.83) * mm, "end": v(-104.77, 35.54) * mm});
            skArc(sketch, "E38.21.28.0", {"start": v(-103.7, 34.21) * mm, "mid": v(-103.84, 33.74) * mm, "end": v(-104, 33.27) * mm});
            skArc(sketch, "E38.25.28.0", {"start": v(-103.7, 34.21) * mm, "mid": v(-103.68, 34.44) * mm, "end": v(-103.8, 34.63) * mm});
            skArc(sketch, "E38.29.28.0", {"start": v(-104.33, 33) * mm, "mid": v(-104.12, 33.08) * mm, "end": v(-104, 33.27) * mm});
            skLineSegment(sketch, "E38.3.29.0", {"start": v(-105.7, 28.28) * mm, "end": v(-107.02, 28.06) * mm});
            skPoint(sketch, "E38.6.29.0", {"position": v(-107.4, 28) * mm});
            skPoint(sketch, "E38.7.29.0", {"position": v(-105.05, 29.77) * mm});
            skPoint(sketch, "E38.8.29.0", {"position": v(-105.45, 28.32) * mm});
            skPoint(sketch, "E38.9.29.0", {"position": v(-106.56, 31.05) * mm});
            skLineSegment(sketch, "E38.10.29.0", {"start": v(-105.25, 29.94) * mm, "end": v(-106.26, 30.8) * mm});
            skArc(sketch, "E38.13.29.0", {"start": v(-107.02, 28.06) * mm, "mid": v(-107.32, 27.91) * mm, "end": v(-107.5, 27.62) * mm});
            skLineSegment(sketch, "E38.14.29.0", {"start": v(-105.25, 29.05) * mm, "end": v(-106.99, 29.53) * mm, "construction": true});
            skArc(sketch, "E38.17.29.0", {"start": v(-106.45, 31.43) * mm, "mid": v(-106.45, 31.09) * mm, "end": v(-106.26, 30.8) * mm});
            skArc(sketch, "E38.21.29.0", {"start": v(-105.12, 29.52) * mm, "mid": v(-105.25, 29.05) * mm, "end": v(-105.38, 28.57) * mm});
            skArc(sketch, "E38.25.29.0", {"start": v(-105.12, 29.52) * mm, "mid": v(-105.12, 29.75) * mm, "end": v(-105.25, 29.94) * mm});
            skArc(sketch, "E38.29.29.0", {"start": v(-105.7, 28.28) * mm, "mid": v(-105.5, 28.38) * mm, "end": v(-105.38, 28.57) * mm});
            skLineSegment(sketch, "E39.3.30.0", {"start": v(-106.87, 23.51) * mm, "end": v(-108.17, 23.23) * mm});
            skPoint(sketch, "E39.6.30.0", {"position": v(-108.55, 23.15) * mm});
            skPoint(sketch, "E39.7.30.0", {"position": v(-106.28, 25.03) * mm});
            skPoint(sketch, "E39.8.30.0", {"position": v(-106.62, 23.56) * mm});
            skPoint(sketch, "E39.9.30.0", {"position": v(-107.84, 26.24) * mm});
            skLineSegment(sketch, "E39.10.30.0", {"start": v(-106.48, 25.18) * mm, "end": v(-107.53, 26) * mm});
            skArc(sketch, "E39.13.30.0", {"start": v(-108.17, 23.23) * mm, "mid": v(-108.47, 23.07) * mm, "end": v(-108.63, 22.77) * mm});
            skLineSegment(sketch, "E39.14.30.0", {"start": v(-106.45, 24.3) * mm, "end": v(-108.2, 24.7) * mm, "construction": true});
            skArc(sketch, "E39.17.30.0", {"start": v(-107.75, 26.62) * mm, "mid": v(-107.73, 26.28) * mm, "end": v(-107.53, 26) * mm});
            skArc(sketch, "E39.21.30.0", {"start": v(-106.34, 24.78) * mm, "mid": v(-106.45, 24.3) * mm, "end": v(-106.56, 23.81) * mm});
            skArc(sketch, "E39.25.30.0", {"start": v(-106.34, 24.78) * mm, "mid": v(-106.35, 25) * mm, "end": v(-106.48, 25.18) * mm});
            skArc(sketch, "E39.29.30.0", {"start": v(-106.87, 23.51) * mm, "mid": v(-106.67, 23.62) * mm, "end": v(-106.56, 23.81) * mm});
            skLineSegment(sketch, "E39.3.31.0", {"start": v(-107.81, 18.7) * mm, "end": v(-109.1, 18.35) * mm});
            skPoint(sketch, "E39.6.31.0", {"position": v(-109.48, 18.26) * mm});
            skPoint(sketch, "E39.7.31.0", {"position": v(-107.3, 20.23) * mm});
            skPoint(sketch, "E39.8.31.0", {"position": v(-107.57, 18.76) * mm});
            skPoint(sketch, "E39.9.31.0", {"position": v(-108.91, 21.38) * mm});
            skLineSegment(sketch, "E39.10.31.0", {"start": v(-107.5, 20.38) * mm, "end": v(-108.6, 21.15) * mm});
            skArc(sketch, "E39.13.31.0", {"start": v(-109.1, 18.35) * mm, "mid": v(-109.4, 18.18) * mm, "end": v(-109.54, 17.87) * mm});
            skLineSegment(sketch, "E39.14.31.0", {"start": v(-107.43, 19.5) * mm, "end": v(-109.2, 19.82) * mm, "construction": true});
            skArc(sketch, "E39.17.31.0", {"start": v(-108.83, 21.76) * mm, "mid": v(-108.8, 21.42) * mm, "end": v(-108.6, 21.15) * mm});
            skArc(sketch, "E39.21.31.0", {"start": v(-107.34, 19.98) * mm, "mid": v(-107.43, 19.5) * mm, "end": v(-107.52, 19.01) * mm});
            skArc(sketch, "E39.25.31.0", {"start": v(-107.34, 19.98) * mm, "mid": v(-107.37, 20.2) * mm, "end": v(-107.5, 20.38) * mm});
            skArc(sketch, "E39.29.31.0", {"start": v(-107.81, 18.7) * mm, "mid": v(-107.62, 18.8) * mm, "end": v(-107.52, 19.01) * mm});
            skLineSegment(sketch, "E39.3.32.0", {"start": v(-108.54, 13.84) * mm, "end": v(-109.81, 13.44) * mm});
            skPoint(sketch, "E39.6.32.0", {"position": v(-110.19, 13.33) * mm});
            skPoint(sketch, "E39.7.32.0", {"position": v(-108.1, 15.4) * mm});
            skPoint(sketch, "E39.8.32.0", {"position": v(-108.3, 13.91) * mm});
            skPoint(sketch, "E39.9.32.0", {"position": v(-109.76, 16.47) * mm});
            skLineSegment(sketch, "E39.10.32.0", {"start": v(-108.31, 15.54) * mm, "end": v(-109.43, 16.26) * mm});
            skArc(sketch, "E39.13.32.0", {"start": v(-109.81, 13.44) * mm, "mid": v(-110.1, 13.25) * mm, "end": v(-110.23, 12.94) * mm});
            skLineSegment(sketch, "E39.14.32.0", {"start": v(-108.2, 14.66) * mm, "end": v(-109.98, 14.9) * mm, "construction": true});
            skArc(sketch, "E39.17.32.0", {"start": v(-109.7, 16.85) * mm, "mid": v(-109.66, 16.52) * mm, "end": v(-109.43, 16.26) * mm});
            skArc(sketch, "E39.21.32.0", {"start": v(-108.13, 15.15) * mm, "mid": v(-108.2, 14.66) * mm, "end": v(-108.27, 14.17) * mm});
            skArc(sketch, "E39.25.32.0", {"start": v(-108.13, 15.15) * mm, "mid": v(-108.17, 15.37) * mm, "end": v(-108.31, 15.54) * mm});
            skArc(sketch, "E39.29.32.0", {"start": v(-108.54, 13.84) * mm, "mid": v(-108.36, 13.96) * mm, "end": v(-108.27, 14.17) * mm});
            skLineSegment(sketch, "E39.3.33.0", {"start": v(-109.05, 8.95) * mm, "end": v(-110.3, 8.5) * mm});
            skPoint(sketch, "E39.6.33.0", {"position": v(-110.67, 8.37) * mm});
            skPoint(sketch, "E39.7.33.0", {"position": v(-108.68, 10.53) * mm});
            skPoint(sketch, "E39.8.33.0", {"position": v(-108.81, 9.04) * mm});
            skPoint(sketch, "E39.9.33.0", {"position": v(-110.39, 11.53) * mm});
            skLineSegment(sketch, "E39.10.33.0", {"start": v(-108.9, 10.66) * mm, "end": v(-110.05, 11.33) * mm});
            skArc(sketch, "E39.13.33.0", {"start": v(-110.3, 8.5) * mm, "mid": v(-110.58, 8.3) * mm, "end": v(-110.7, 7.98) * mm});
            skLineSegment(sketch, "E39.14.33.0", {"start": v(-108.75, 9.79) * mm, "end": v(-110.54, 9.95) * mm, "construction": true});
            skArc(sketch, "E39.17.33.0", {"start": v(-110.35, 11.91) * mm, "mid": v(-110.29, 11.58) * mm, "end": v(-110.05, 11.33) * mm});
            skArc(sketch, "E39.21.33.0", {"start": v(-108.7, 10.28) * mm, "mid": v(-108.75, 9.79) * mm, "end": v(-108.8, 9.3) * mm});
            skArc(sketch, "E39.25.33.0", {"start": v(-108.7, 10.28) * mm, "mid": v(-108.75, 10.5) * mm, "end": v(-108.9, 10.66) * mm});
            skArc(sketch, "E39.29.33.0", {"start": v(-109.05, 8.95) * mm, "mid": v(-108.87, 9.09) * mm, "end": v(-108.8, 9.3) * mm});
            skLineSegment(sketch, "E39.3.34.0", {"start": v(-109.35, 4.05) * mm, "end": v(-110.58, 3.54) * mm});
            skPoint(sketch, "E39.6.34.0", {"position": v(-110.94, 3.4) * mm});
            skPoint(sketch, "E39.7.34.0", {"position": v(-109.04, 5.65) * mm});
            skPoint(sketch, "E39.8.34.0", {"position": v(-109.1, 4.15) * mm});
            skPoint(sketch, "E39.9.34.0", {"position": v(-110.8, 6.56) * mm});
            skLineSegment(sketch, "E39.10.34.0", {"start": v(-109.27, 5.77) * mm, "end": v(-110.45, 6.38) * mm});
            skArc(sketch, "E39.13.34.0", {"start": v(-110.58, 3.54) * mm, "mid": v(-110.84, 3.33) * mm, "end": v(-110.95, 3) * mm});
            skLineSegment(sketch, "E39.14.34.0", {"start": v(-109.08, 4.9) * mm, "end": v(-110.88, 4.98) * mm, "construction": true});
            skArc(sketch, "E39.17.34.0", {"start": v(-110.77, 6.95) * mm, "mid": v(-110.7, 6.62) * mm, "end": v(-110.45, 6.38) * mm});
            skArc(sketch, "E39.21.34.0", {"start": v(-109.06, 5.4) * mm, "mid": v(-109.08, 4.9) * mm, "end": v(-109.1, 4.4) * mm});
            skArc(sketch, "E39.25.34.0", {"start": v(-109.06, 5.4) * mm, "mid": v(-109.1, 5.61) * mm, "end": v(-109.27, 5.77) * mm});
            skArc(sketch, "E39.29.34.0", {"start": v(-109.35, 4.05) * mm, "mid": v(-109.17, 4.2) * mm, "end": v(-109.1, 4.4) * mm});
            skLineSegment(sketch, "E39.3.35.0", {"start": v(-109.42, -0.86) * mm, "end": v(-110.62, -1.42) * mm});
            skPoint(sketch, "E39.6.35.0", {"position": v(-110.98, -1.59) * mm});
            skPoint(sketch, "E39.7.35.0", {"position": v(-109.19, 0.75) * mm});
            skPoint(sketch, "E39.8.35.0", {"position": v(-109.19, -0.75) * mm});
            skPoint(sketch, "E39.9.35.0", {"position": v(-110.98, 1.59) * mm});
            skLineSegment(sketch, "E39.10.35.0", {"start": v(-109.42, 0.86) * mm, "end": v(-110.62, 1.42) * mm});
            skArc(sketch, "E39.13.35.0", {"start": v(-110.62, -1.42) * mm, "mid": v(-110.88, -1.65) * mm, "end": v(-110.97, -1.98) * mm});
            skLineSegment(sketch, "E39.14.35.0", {"start": v(-109.19, 0) * mm, "end": v(-110.99, 0) * mm, "construction": true});
            skArc(sketch, "E39.17.35.0", {"start": v(-110.97, 1.98) * mm, "mid": v(-110.88, 1.65) * mm, "end": v(-110.62, 1.42) * mm});
            skArc(sketch, "E39.21.35.0", {"start": v(-109.19, 0.5) * mm, "mid": v(-109.19, 0) * mm, "end": v(-109.19, -0.5) * mm});
            skArc(sketch, "E39.25.35.0", {"start": v(-109.19, 0.5) * mm, "mid": v(-109.25, 0.71) * mm, "end": v(-109.42, 0.86) * mm});
            skArc(sketch, "E39.29.35.0", {"start": v(-109.42, -0.86) * mm, "mid": v(-109.25, -0.71) * mm, "end": v(-109.19, -0.5) * mm});
            skLineSegment(sketch, "E39.3.36.0", {"start": v(-109.27, -5.77) * mm, "end": v(-110.45, -6.38) * mm});
            skPoint(sketch, "E39.6.36.0", {"position": v(-110.8, -6.56) * mm});
            skPoint(sketch, "E39.7.36.0", {"position": v(-109.1, -4.15) * mm});
            skPoint(sketch, "E39.8.36.0", {"position": v(-109.04, -5.65) * mm});
            skPoint(sketch, "E39.9.36.0", {"position": v(-110.94, -3.4) * mm});
            skLineSegment(sketch, "E39.10.36.0", {"start": v(-109.35, -4.05) * mm, "end": v(-110.58, -3.54) * mm});
            skArc(sketch, "E39.13.36.0", {"start": v(-110.45, -6.38) * mm, "mid": v(-110.7, -6.62) * mm, "end": v(-110.77, -6.95) * mm});
            skLineSegment(sketch, "E39.14.36.0", {"start": v(-109.08, -4.9) * mm, "end": v(-110.88, -4.98) * mm, "construction": true});
            skArc(sketch, "E39.17.36.0", {"start": v(-110.95, -3) * mm, "mid": v(-110.84, -3.33) * mm, "end": v(-110.58, -3.54) * mm});
            skArc(sketch, "E39.21.36.0", {"start": v(-109.1, -4.4) * mm, "mid": v(-109.08, -4.9) * mm, "end": v(-109.06, -5.4) * mm});
            skArc(sketch, "E39.25.36.0", {"start": v(-109.1, -4.4) * mm, "mid": v(-109.17, -4.2) * mm, "end": v(-109.35, -4.05) * mm});
            skArc(sketch, "E39.29.36.0", {"start": v(-109.27, -5.77) * mm, "mid": v(-109.1, -5.61) * mm, "end": v(-109.06, -5.4) * mm});
            skLineSegment(sketch, "E39.3.37.0", {"start": v(-108.9, -10.66) * mm, "end": v(-110.05, -11.33) * mm});
            skPoint(sketch, "E39.6.37.0", {"position": v(-110.39, -11.53) * mm});
            skPoint(sketch, "E39.7.37.0", {"position": v(-108.81, -9.04) * mm});
            skPoint(sketch, "E39.8.37.0", {"position": v(-108.68, -10.53) * mm});
            skPoint(sketch, "E39.9.37.0", {"position": v(-110.67, -8.37) * mm});
            skLineSegment(sketch, "E39.10.37.0", {"start": v(-109.05, -8.95) * mm, "end": v(-110.3, -8.5) * mm});
            skArc(sketch, "E39.13.37.0", {"start": v(-110.05, -11.33) * mm, "mid": v(-110.29, -11.58) * mm, "end": v(-110.35, -11.91) * mm});
            skLineSegment(sketch, "E39.14.37.0", {"start": v(-108.75, -9.79) * mm, "end": v(-110.54, -9.95) * mm, "construction": true});
            skArc(sketch, "E39.17.37.0", {"start": v(-110.7, -7.98) * mm, "mid": v(-110.58, -8.3) * mm, "end": v(-110.3, -8.5) * mm});
            skArc(sketch, "E39.21.37.0", {"start": v(-108.8, -9.3) * mm, "mid": v(-108.75, -9.79) * mm, "end": v(-108.7, -10.28) * mm});
            skArc(sketch, "E39.25.37.0", {"start": v(-108.8, -9.3) * mm, "mid": v(-108.87, -9.09) * mm, "end": v(-109.05, -8.95) * mm});
            skArc(sketch, "E39.29.37.0", {"start": v(-108.9, -10.66) * mm, "mid": v(-108.75, -10.5) * mm, "end": v(-108.7, -10.28) * mm});
            skLineSegment(sketch, "E39.3.38.0", {"start": v(-108.31, -15.54) * mm, "end": v(-109.43, -16.26) * mm});
            skPoint(sketch, "E39.6.38.0", {"position": v(-109.76, -16.47) * mm});
            skPoint(sketch, "E39.7.38.0", {"position": v(-108.3, -13.91) * mm});
            skPoint(sketch, "E39.8.38.0", {"position": v(-108.1, -15.4) * mm});
            skPoint(sketch, "E39.9.38.0", {"position": v(-110.19, -13.33) * mm});
            skLineSegment(sketch, "E39.10.38.0", {"start": v(-108.54, -13.84) * mm, "end": v(-109.81, -13.44) * mm});
            skArc(sketch, "E39.13.38.0", {"start": v(-109.43, -16.26) * mm, "mid": v(-109.66, -16.52) * mm, "end": v(-109.7, -16.85) * mm});
            skLineSegment(sketch, "E39.14.38.0", {"start": v(-108.2, -14.66) * mm, "end": v(-109.98, -14.9) * mm, "construction": true});
            skArc(sketch, "E39.17.38.0", {"start": v(-110.23, -12.94) * mm, "mid": v(-110.1, -13.25) * mm, "end": v(-109.81, -13.44) * mm});
            skArc(sketch, "E39.21.38.0", {"start": v(-108.27, -14.17) * mm, "mid": v(-108.2, -14.66) * mm, "end": v(-108.13, -15.15) * mm});
            skArc(sketch, "E39.25.38.0", {"start": v(-108.27, -14.17) * mm, "mid": v(-108.36, -13.96) * mm, "end": v(-108.54, -13.84) * mm});
            skArc(sketch, "E39.29.38.0", {"start": v(-108.31, -15.54) * mm, "mid": v(-108.17, -15.37) * mm, "end": v(-108.13, -15.15) * mm});
            skLineSegment(sketch, "E39.3.39.0", {"start": v(-107.5, -20.38) * mm, "end": v(-108.6, -21.15) * mm});
            skPoint(sketch, "E39.6.39.0", {"position": v(-108.91, -21.38) * mm});
            skPoint(sketch, "E39.7.39.0", {"position": v(-107.57, -18.76) * mm});
            skPoint(sketch, "E39.8.39.0", {"position": v(-107.3, -20.23) * mm});
            skPoint(sketch, "E39.9.39.0", {"position": v(-109.48, -18.26) * mm});
            skLineSegment(sketch, "E39.10.39.0", {"start": v(-107.81, -18.7) * mm, "end": v(-109.1, -18.35) * mm});
            skArc(sketch, "E39.13.39.0", {"start": v(-108.6, -21.15) * mm, "mid": v(-108.8, -21.42) * mm, "end": v(-108.83, -21.76) * mm});
            skLineSegment(sketch, "E39.14.39.0", {"start": v(-107.43, -19.5) * mm, "end": v(-109.2, -19.82) * mm, "construction": true});
            skArc(sketch, "E39.17.39.0", {"start": v(-109.54, -17.87) * mm, "mid": v(-109.4, -18.18) * mm, "end": v(-109.1, -18.35) * mm});
            skArc(sketch, "E39.21.39.0", {"start": v(-107.52, -19.01) * mm, "mid": v(-107.43, -19.5) * mm, "end": v(-107.34, -19.98) * mm});
            skArc(sketch, "E39.25.39.0", {"start": v(-107.52, -19.01) * mm, "mid": v(-107.62, -18.8) * mm, "end": v(-107.81, -18.7) * mm});
            skArc(sketch, "E39.29.39.0", {"start": v(-107.5, -20.38) * mm, "mid": v(-107.37, -20.2) * mm, "end": v(-107.34, -19.98) * mm});
            skLineSegment(sketch, "E39.3.40.0", {"start": v(-106.48, -25.18) * mm, "end": v(-107.53, -26) * mm});
            skPoint(sketch, "E39.6.40.0", {"position": v(-107.84, -26.24) * mm});
            skPoint(sketch, "E39.7.40.0", {"position": v(-106.62, -23.56) * mm});
            skPoint(sketch, "E39.8.40.0", {"position": v(-106.28, -25.03) * mm});
            skPoint(sketch, "E39.9.40.0", {"position": v(-108.55, -23.15) * mm});
            skLineSegment(sketch, "E39.10.40.0", {"start": v(-106.87, -23.51) * mm, "end": v(-108.17, -23.23) * mm});
            skArc(sketch, "E39.13.40.0", {"start": v(-107.53, -26) * mm, "mid": v(-107.73, -26.28) * mm, "end": v(-107.75, -26.62) * mm});
            skLineSegment(sketch, "E39.14.40.0", {"start": v(-106.45, -24.3) * mm, "end": v(-108.2, -24.7) * mm, "construction": true});
            skArc(sketch, "E39.17.40.0", {"start": v(-108.63, -22.77) * mm, "mid": v(-108.47, -23.07) * mm, "end": v(-108.17, -23.23) * mm});
            skArc(sketch, "E39.21.40.0", {"start": v(-106.56, -23.81) * mm, "mid": v(-106.45, -24.3) * mm, "end": v(-106.34, -24.78) * mm});
            skArc(sketch, "E39.25.40.0", {"start": v(-106.56, -23.81) * mm, "mid": v(-106.67, -23.62) * mm, "end": v(-106.87, -23.51) * mm});
            skArc(sketch, "E39.29.40.0", {"start": v(-106.48, -25.18) * mm, "mid": v(-106.35, -25) * mm, "end": v(-106.34, -24.78) * mm});
            skLineSegment(sketch, "E39.3.41.0", {"start": v(-105.25, -29.94) * mm, "end": v(-106.26, -30.8) * mm});
            skPoint(sketch, "E39.6.41.0", {"position": v(-106.56, -31.05) * mm});
            skPoint(sketch, "E39.7.41.0", {"position": v(-105.45, -28.32) * mm});
            skPoint(sketch, "E39.8.41.0", {"position": v(-105.05, -29.77) * mm});
            skPoint(sketch, "E39.9.41.0", {"position": v(-107.4, -28) * mm});
            skLineSegment(sketch, "E39.10.41.0", {"start": v(-105.7, -28.28) * mm, "end": v(-107.02, -28.06) * mm});
            skArc(sketch, "E39.13.41.0", {"start": v(-106.26, -30.8) * mm, "mid": v(-106.45, -31.09) * mm, "end": v(-106.45, -31.43) * mm});
            skLineSegment(sketch, "E39.14.41.0", {"start": v(-105.25, -29.05) * mm, "end": v(-106.99, -29.53) * mm, "construction": true});
            skArc(sketch, "E39.17.41.0", {"start": v(-107.5, -27.62) * mm, "mid": v(-107.32, -27.91) * mm, "end": v(-107.02, -28.06) * mm});
            skArc(sketch, "E39.21.41.0", {"start": v(-105.38, -28.57) * mm, "mid": v(-105.25, -29.05) * mm, "end": v(-105.12, -29.52) * mm});
            skArc(sketch, "E39.25.41.0", {"start": v(-105.38, -28.57) * mm, "mid": v(-105.5, -28.38) * mm, "end": v(-105.7, -28.28) * mm});
            skArc(sketch, "E39.29.41.0", {"start": v(-105.25, -29.94) * mm, "mid": v(-105.12, -29.75) * mm, "end": v(-105.12, -29.52) * mm});
            skLineSegment(sketch, "E39.3.42.0", {"start": v(-103.8, -34.63) * mm, "end": v(-104.77, -35.54) * mm});
            skPoint(sketch, "E39.6.42.0", {"position": v(-105.06, -35.8) * mm});
            skPoint(sketch, "E39.7.42.0", {"position": v(-104.07, -33.03) * mm});
            skPoint(sketch, "E39.8.42.0", {"position": v(-103.61, -34.45) * mm});
            skPoint(sketch, "E39.9.42.0", {"position": v(-106.04, -32.79) * mm});
            skLineSegment(sketch, "E39.10.42.0", {"start": v(-104.33, -33) * mm, "end": v(-105.65, -32.83) * mm});
            skArc(sketch, "E39.13.42.0", {"start": v(-104.77, -35.54) * mm, "mid": v(-104.94, -35.83) * mm, "end": v(-104.93, -36.17) * mm});
            skLineSegment(sketch, "E39.14.42.0", {"start": v(-103.84, -33.74) * mm, "end": v(-105.56, -34.3) * mm, "construction": true});
            skArc(sketch, "E39.17.42.0", {"start": v(-106.15, -32.41) * mm, "mid": v(-105.96, -32.7) * mm, "end": v(-105.65, -32.83) * mm});
            skArc(sketch, "E39.21.42.0", {"start": v(-104, -33.27) * mm, "mid": v(-103.84, -33.74) * mm, "end": v(-103.7, -34.21) * mm});
            skArc(sketch, "E39.25.42.0", {"start": v(-104, -33.27) * mm, "mid": v(-104.12, -33.08) * mm, "end": v(-104.33, -33) * mm});
            skArc(sketch, "E39.29.42.0", {"start": v(-103.8, -34.63) * mm, "mid": v(-103.68, -34.44) * mm, "end": v(-103.7, -34.21) * mm});
            skLineSegment(sketch, "E39.3.43.0", {"start": v(-102.14, -39.25) * mm, "end": v(-103.07, -40.2) * mm});
            skPoint(sketch, "E39.6.43.0", {"position": v(-103.34, -40.48) * mm});
            skPoint(sketch, "E39.7.43.0", {"position": v(-102.49, -37.66) * mm});
            skPoint(sketch, "E39.8.43.0", {"position": v(-101.96, -39.07) * mm});
            skPoint(sketch, "E39.9.43.0", {"position": v(-104.46, -37.51) * mm});
            skLineSegment(sketch, "E39.10.43.0", {"start": v(-102.74, -37.64) * mm, "end": v(-104.07, -37.54) * mm});
            skArc(sketch, "E39.13.43.0", {"start": v(-103.07, -40.2) * mm, "mid": v(-103.23, -40.5) * mm, "end": v(-103.2, -40.84) * mm});
            skLineSegment(sketch, "E39.14.43.0", {"start": v(-102.23, -38.37) * mm, "end": v(-103.91, -39) * mm, "construction": true});
            skArc(sketch, "E39.17.43.0", {"start": v(-104.59, -37.14) * mm, "mid": v(-104.39, -37.42) * mm, "end": v(-104.07, -37.54) * mm});
            skArc(sketch, "E39.21.43.0", {"start": v(-102.4, -37.9) * mm, "mid": v(-102.23, -38.37) * mm, "end": v(-102.05, -38.83) * mm});
            skArc(sketch, "E39.25.43.0", {"start": v(-102.4, -37.9) * mm, "mid": v(-102.53, -37.72) * mm, "end": v(-102.74, -37.64) * mm});
            skArc(sketch, "E39.29.43.0", {"start": v(-102.14, -39.25) * mm, "mid": v(-102.03, -39.05) * mm, "end": v(-102.05, -38.83) * mm});
            skLineSegment(sketch, "E39.3.44.0", {"start": v(-100.28, -43.8) * mm, "end": v(-101.16, -44.78) * mm});
            skPoint(sketch, "E39.6.44.0", {"position": v(-101.42, -45.07) * mm});
            skPoint(sketch, "E39.7.44.0", {"position": v(-100.7, -42.22) * mm});
            skPoint(sketch, "E39.8.44.0", {"position": v(-100.1, -43.6) * mm});
            skPoint(sketch, "E39.9.44.0", {"position": v(-102.67, -42.16) * mm});
            skLineSegment(sketch, "E39.10.44.0", {"start": v(-100.95, -42.21) * mm, "end": v(-102.28, -42.17) * mm});
            skArc(sketch, "E39.13.44.0", {"start": v(-101.16, -44.78) * mm, "mid": v(-101.3, -45.1) * mm, "end": v(-101.26, -45.43) * mm});
            skLineSegment(sketch, "E39.14.44.0", {"start": v(-100.4, -42.91) * mm, "end": v(-102.06, -43.62) * mm, "construction": true});
            skArc(sketch, "E39.17.44.0", {"start": v(-102.82, -41.8) * mm, "mid": v(-102.6, -42.06) * mm, "end": v(-102.28, -42.17) * mm});
            skArc(sketch, "E39.21.44.0", {"start": v(-100.6, -42.46) * mm, "mid": v(-100.4, -42.91) * mm, "end": v(-100.2, -43.37) * mm});
            skArc(sketch, "E39.25.44.0", {"start": v(-100.6, -42.46) * mm, "mid": v(-100.74, -42.28) * mm, "end": v(-100.95, -42.21) * mm});
            skArc(sketch, "E39.29.44.0", {"start": v(-100.28, -43.8) * mm, "mid": v(-100.18, -43.6) * mm, "end": v(-100.2, -43.37) * mm});
            skLineSegment(sketch, "E39.3.45.0", {"start": v(-98.21, -48.25) * mm, "end": v(-99.05, -49.28) * mm});
            skPoint(sketch, "E39.6.45.0", {"position": v(-99.3, -49.58) * mm});
            skPoint(sketch, "E39.7.45.0", {"position": v(-98.7, -46.7) * mm});
            skPoint(sketch, "E39.8.45.0", {"position": v(-98.05, -48.05) * mm});
            skPoint(sketch, "E39.9.45.0", {"position": v(-100.67, -46.72) * mm});
            skLineSegment(sketch, "E39.10.45.0", {"start": v(-98.95, -46.7) * mm, "end": v(-100.29, -46.72) * mm});
            skArc(sketch, "E39.13.45.0", {"start": v(-99.05, -49.28) * mm, "mid": v(-99.18, -49.6) * mm, "end": v(-99.12, -49.93) * mm});
            skLineSegment(sketch, "E39.14.45.0", {"start": v(-98.38, -47.38) * mm, "end": v(-100, -48.16) * mm, "construction": true});
            skArc(sketch, "E39.17.45.0", {"start": v(-100.84, -46.37) * mm, "mid": v(-100.61, -46.63) * mm, "end": v(-100.29, -46.72) * mm});
            skArc(sketch, "E39.21.45.0", {"start": v(-98.59, -46.93) * mm, "mid": v(-98.38, -47.38) * mm, "end": v(-98.16, -47.82) * mm});
            skArc(sketch, "E39.25.45.0", {"start": v(-98.59, -46.93) * mm, "mid": v(-98.74, -46.76) * mm, "end": v(-98.95, -46.7) * mm});
            skArc(sketch, "E39.29.45.0", {"start": v(-98.21, -48.25) * mm, "mid": v(-98.12, -48.04) * mm, "end": v(-98.16, -47.82) * mm});
            skLineSegment(sketch, "E39.3.46.0", {"start": v(-95.95, -52.6) * mm, "end": v(-96.74, -53.67) * mm});
            skPoint(sketch, "E39.6.46.0", {"position": v(-96.97, -53.98) * mm});
            skPoint(sketch, "E39.7.46.0", {"position": v(-96.5, -51.08) * mm});
            skPoint(sketch, "E39.8.46.0", {"position": v(-95.8, -52.4) * mm});
            skPoint(sketch, "E39.9.46.0", {"position": v(-98.48, -51.2) * mm});
            skLineSegment(sketch, "E39.10.46.0", {"start": v(-96.76, -51.1) * mm, "end": v(-98.09, -51.17) * mm});
            skArc(sketch, "E39.13.46.0", {"start": v(-96.74, -53.67) * mm, "mid": v(-96.86, -54) * mm, "end": v(-96.78, -54.33) * mm});
            skLineSegment(sketch, "E39.14.46.0", {"start": v(-96.15, -51.74) * mm, "end": v(-97.74, -52.6) * mm, "construction": true});
            skArc(sketch, "E39.17.46.0", {"start": v(-98.66, -50.85) * mm, "mid": v(-98.42, -51.1) * mm, "end": v(-98.09, -51.17) * mm});
            skArc(sketch, "E39.21.46.0", {"start": v(-96.38, -51.3) * mm, "mid": v(-96.15, -51.74) * mm, "end": v(-95.92, -52.18) * mm});
            skArc(sketch, "E39.25.46.0", {"start": v(-96.38, -51.3) * mm, "mid": v(-96.54, -51.14) * mm, "end": v(-96.76, -51.1) * mm});
            skArc(sketch, "E39.29.46.0", {"start": v(-95.95, -52.6) * mm, "mid": v(-95.87, -52.4) * mm, "end": v(-95.92, -52.18) * mm});
            skLineSegment(sketch, "E39.3.47.0", {"start": v(-93.49, -56.86) * mm, "end": v(-94.24, -57.96) * mm});
            skPoint(sketch, "E39.6.47.0", {"position": v(-94.46, -58.28) * mm});
            skPoint(sketch, "E39.7.47.0", {"position": v(-94.12, -55.36) * mm});
            skPoint(sketch, "E39.8.47.0", {"position": v(-93.35, -56.65) * mm});
            skPoint(sketch, "E39.9.47.0", {"position": v(-96.08, -55.56) * mm});
            skLineSegment(sketch, "E39.10.47.0", {"start": v(-94.37, -55.38) * mm, "end": v(-95.7, -55.52) * mm});
            skArc(sketch, "E39.13.47.0", {"start": v(-94.24, -57.96) * mm, "mid": v(-94.34, -58.28) * mm, "end": v(-94.25, -58.61) * mm});
            skLineSegment(sketch, "E39.14.47.0", {"start": v(-93.73, -56) * mm, "end": v(-95.28, -56.93) * mm, "construction": true});
            skArc(sketch, "E39.17.47.0", {"start": v(-96.28, -55.22) * mm, "mid": v(-96.03, -55.46) * mm, "end": v(-95.7, -55.52) * mm});
            skArc(sketch, "E39.21.47.0", {"start": v(-93.99, -55.58) * mm, "mid": v(-93.73, -56) * mm, "end": v(-93.48, -56.43) * mm});
            skArc(sketch, "E39.25.47.0", {"start": v(-93.99, -55.58) * mm, "mid": v(-94.15, -55.42) * mm, "end": v(-94.37, -55.38) * mm});
            skArc(sketch, "E39.29.47.0", {"start": v(-93.49, -56.86) * mm, "mid": v(-93.42, -56.64) * mm, "end": v(-93.48, -56.43) * mm});
            skLineSegment(sketch, "E39.3.48.0", {"start": v(-90.84, -61) * mm, "end": v(-91.54, -62.13) * mm});
            skPoint(sketch, "E39.6.48.0", {"position": v(-91.75, -62.46) * mm});
            skPoint(sketch, "E39.7.48.0", {"position": v(-91.54, -59.52) * mm});
            skPoint(sketch, "E39.8.48.0", {"position": v(-90.71, -60.78) * mm});
            skPoint(sketch, "E39.9.48.0", {"position": v(-93.5, -59.81) * mm});
            skLineSegment(sketch, "E39.10.48.0", {"start": v(-91.8, -59.56) * mm, "end": v(-93.1, -59.76) * mm});
            skArc(sketch, "E39.13.48.0", {"start": v(-91.54, -62.13) * mm, "mid": v(-91.63, -62.46) * mm, "end": v(-91.53, -62.78) * mm});
            skLineSegment(sketch, "E39.14.48.0", {"start": v(-91.13, -60.15) * mm, "end": v(-92.63, -61.14) * mm, "construction": true});
            skArc(sketch, "E39.17.48.0", {"start": v(-93.7, -59.49) * mm, "mid": v(-93.44, -59.7) * mm, "end": v(-93.1, -59.76) * mm});
            skArc(sketch, "E39.21.48.0", {"start": v(-91.4, -59.74) * mm, "mid": v(-91.13, -60.15) * mm, "end": v(-90.85, -60.56) * mm});
            skArc(sketch, "E39.25.48.0", {"start": v(-91.4, -59.74) * mm, "mid": v(-91.57, -59.6) * mm, "end": v(-91.8, -59.56) * mm});
            skArc(sketch, "E39.29.48.0", {"start": v(-90.84, -61) * mm, "mid": v(-90.79, -60.78) * mm, "end": v(-90.85, -60.56) * mm});
            skLineSegment(sketch, "E39.3.49.0", {"start": v(-88.02, -65) * mm, "end": v(-88.66, -66.17) * mm});
            skPoint(sketch, "E39.6.49.0", {"position": v(-88.85, -66.51) * mm});
            skPoint(sketch, "E39.7.49.0", {"position": v(-88.77, -63.57) * mm});
            skPoint(sketch, "E39.8.49.0", {"position": v(-87.9, -64.78) * mm});
            skPoint(sketch, "E39.9.49.0", {"position": v(-90.71, -63.95) * mm});
            skLineSegment(sketch, "E39.10.49.0", {"start": v(-89.03, -63.62) * mm, "end": v(-90.33, -63.87) * mm});
            skArc(sketch, "E39.13.49.0", {"start": v(-88.66, -66.17) * mm, "mid": v(-88.74, -66.5) * mm, "end": v(-88.62, -66.83) * mm});
            skLineSegment(sketch, "E39.14.49.0", {"start": v(-88.34, -64.18) * mm, "end": v(-89.8, -65.24) * mm, "construction": true});
            skArc(sketch, "E39.17.49.0", {"start": v(-90.94, -63.63) * mm, "mid": v(-90.67, -63.84) * mm, "end": v(-90.33, -63.87) * mm});
            skArc(sketch, "E39.21.49.0", {"start": v(-88.62, -63.78) * mm, "mid": v(-88.34, -64.18) * mm, "end": v(-88.04, -64.58) * mm});
            skArc(sketch, "E39.25.49.0", {"start": v(-88.62, -63.78) * mm, "mid": v(-88.8, -63.64) * mm, "end": v(-89.03, -63.62) * mm});
            skArc(sketch, "E39.29.49.0", {"start": v(-88.02, -65) * mm, "mid": v(-87.97, -64.79) * mm, "end": v(-88.04, -64.58) * mm});
            skLineSegment(sketch, "E40.3.50.0", {"start": v(-85.01, -68.9) * mm, "end": v(-85.6, -70.08) * mm});
            skPoint(sketch, "E40.6.50.0", {"position": v(-85.78, -70.43) * mm});
            skPoint(sketch, "E40.7.50.0", {"position": v(-85.83, -67.49) * mm});
            skPoint(sketch, "E40.8.50.0", {"position": v(-84.9, -68.66) * mm});
            skPoint(sketch, "E40.9.50.0", {"position": v(-87.75, -67.95) * mm});
            skLineSegment(sketch, "E40.10.50.0", {"start": v(-86.08, -67.55) * mm, "end": v(-87.38, -67.86) * mm});
            skArc(sketch, "E40.13.50.0", {"start": v(-85.6, -70.08) * mm, "mid": v(-85.66, -70.42) * mm, "end": v(-85.53, -70.73) * mm});
            skLineSegment(sketch, "E40.14.50.0", {"start": v(-85.37, -68.08) * mm, "end": v(-86.77, -69.2) * mm, "construction": true});
            skArc(sketch, "E40.17.50.0", {"start": v(-88, -67.64) * mm, "mid": v(-87.72, -67.85) * mm, "end": v(-87.38, -67.86) * mm});
            skArc(sketch, "E40.21.50.0", {"start": v(-85.67, -67.7) * mm, "mid": v(-85.37, -68.08) * mm, "end": v(-85.06, -68.46) * mm});
            skArc(sketch, "E40.25.50.0", {"start": v(-85.67, -67.7) * mm, "mid": v(-85.86, -67.56) * mm, "end": v(-86.08, -67.55) * mm});
            skArc(sketch, "E40.29.50.0", {"start": v(-85.01, -68.9) * mm, "mid": v(-84.97, -68.67) * mm, "end": v(-85.06, -68.46) * mm});
            skLineSegment(sketch, "E40.3.51.0", {"start": v(-81.84, -72.64) * mm, "end": v(-82.37, -73.85) * mm});
            skPoint(sketch, "E40.6.51.0", {"position": v(-82.53, -74.21) * mm});
            skPoint(sketch, "E40.7.51.0", {"position": v(-82.72, -71.27) * mm});
            skPoint(sketch, "E40.8.51.0", {"position": v(-81.73, -72.4) * mm});
            skPoint(sketch, "E40.9.51.0", {"position": v(-84.62, -71.82) * mm});
            skLineSegment(sketch, "E40.10.51.0", {"start": v(-82.96, -71.34) * mm, "end": v(-84.24, -71.71) * mm});
            skArc(sketch, "E40.13.51.0", {"start": v(-82.37, -73.85) * mm, "mid": v(-82.42, -74.2) * mm, "end": v(-82.27, -74.5) * mm});
            skLineSegment(sketch, "E40.14.51.0", {"start": v(-82.23, -71.84) * mm, "end": v(-83.58, -73.02) * mm, "construction": true});
            skArc(sketch, "E40.17.51.0", {"start": v(-84.87, -71.52) * mm, "mid": v(-84.58, -71.71) * mm, "end": v(-84.24, -71.71) * mm});
            skArc(sketch, "E40.21.51.0", {"start": v(-82.55, -71.47) * mm, "mid": v(-82.23, -71.84) * mm, "end": v(-81.9, -72.21) * mm});
            skArc(sketch, "E40.25.51.0", {"start": v(-82.55, -71.47) * mm, "mid": v(-82.74, -71.34) * mm, "end": v(-82.96, -71.34) * mm});
            skArc(sketch, "E40.29.51.0", {"start": v(-81.84, -72.64) * mm, "mid": v(-81.8, -72.41) * mm, "end": v(-81.9, -72.21) * mm});
            skLineSegment(sketch, "E40.3.52.0", {"start": v(-78.5, -76.24) * mm, "end": v(-78.98, -77.48) * mm});
            skPoint(sketch, "E40.6.52.0", {"position": v(-79.12, -77.84) * mm});
            skPoint(sketch, "E40.7.52.0", {"position": v(-79.44, -74.91) * mm});
            skPoint(sketch, "E40.8.52.0", {"position": v(-78.4, -76) * mm});
            skPoint(sketch, "E40.9.52.0", {"position": v(-81.3, -75.55) * mm});
            skLineSegment(sketch, "E40.10.52.0", {"start": v(-79.68, -75) * mm, "end": v(-80.94, -75.42) * mm});
            skArc(sketch, "E40.13.52.0", {"start": v(-78.98, -77.48) * mm, "mid": v(-79, -77.82) * mm, "end": v(-78.84, -78.12) * mm});
            skLineSegment(sketch, "E40.14.52.0", {"start": v(-78.92, -75.46) * mm, "end": v(-80.22, -76.7) * mm, "construction": true});
            skArc(sketch, "E40.17.52.0", {"start": v(-81.57, -75.26) * mm, "mid": v(-81.28, -75.43) * mm, "end": v(-80.94, -75.42) * mm});
            skArc(sketch, "E40.21.52.0", {"start": v(-79.26, -75.1) * mm, "mid": v(-78.92, -75.46) * mm, "end": v(-78.58, -75.81) * mm});
            skArc(sketch, "E40.25.52.0", {"start": v(-79.26, -75.1) * mm, "mid": v(-79.46, -74.99) * mm, "end": v(-79.68, -75) * mm});
            skArc(sketch, "E40.29.52.0", {"start": v(-78.5, -76.24) * mm, "mid": v(-78.47, -76.01) * mm, "end": v(-78.58, -75.81) * mm});
            skLineSegment(sketch, "E40.3.53.0", {"start": v(-75, -79.68) * mm, "end": v(-75.42, -80.94) * mm});
            skPoint(sketch, "E40.6.53.0", {"position": v(-75.55, -81.3) * mm});
            skPoint(sketch, "E40.7.53.0", {"position": v(-76, -78.4) * mm});
            skPoint(sketch, "E40.8.53.0", {"position": v(-74.91, -79.44) * mm});
            skPoint(sketch, "E40.9.53.0", {"position": v(-77.84, -79.12) * mm});
            skLineSegment(sketch, "E40.10.53.0", {"start": v(-76.24, -78.5) * mm, "end": v(-77.48, -78.98) * mm});
            skArc(sketch, "E40.13.53.0", {"start": v(-75.42, -80.94) * mm, "mid": v(-75.43, -81.28) * mm, "end": v(-75.26, -81.57) * mm});
            skLineSegment(sketch, "E40.14.53.0", {"start": v(-75.46, -78.92) * mm, "end": v(-76.7, -80.22) * mm, "construction": true});
            skArc(sketch, "E40.17.53.0", {"start": v(-78.12, -78.84) * mm, "mid": v(-77.82, -79) * mm, "end": v(-77.48, -78.98) * mm});
            skArc(sketch, "E40.21.53.0", {"start": v(-75.81, -78.58) * mm, "mid": v(-75.46, -78.92) * mm, "end": v(-75.1, -79.26) * mm});
            skArc(sketch, "E40.25.53.0", {"start": v(-75.81, -78.58) * mm, "mid": v(-76.01, -78.47) * mm, "end": v(-76.24, -78.5) * mm});
            skArc(sketch, "E40.29.53.0", {"start": v(-75, -79.68) * mm, "mid": v(-74.99, -79.46) * mm, "end": v(-75.1, -79.26) * mm});
            skLineSegment(sketch, "E40.3.54.0", {"start": v(-71.34, -82.96) * mm, "end": v(-71.71, -84.24) * mm});
            skPoint(sketch, "E40.6.54.0", {"position": v(-71.82, -84.62) * mm});
            skPoint(sketch, "E40.7.54.0", {"position": v(-72.4, -81.73) * mm});
            skPoint(sketch, "E40.8.54.0", {"position": v(-71.27, -82.72) * mm});
            skPoint(sketch, "E40.9.54.0", {"position": v(-74.21, -82.53) * mm});
            skLineSegment(sketch, "E40.10.54.0", {"start": v(-72.64, -81.84) * mm, "end": v(-73.85, -82.37) * mm});
            skArc(sketch, "E40.13.54.0", {"start": v(-71.71, -84.24) * mm, "mid": v(-71.71, -84.58) * mm, "end": v(-71.52, -84.87) * mm});
            skLineSegment(sketch, "E40.14.54.0", {"start": v(-71.84, -82.23) * mm, "end": v(-73.02, -83.58) * mm, "construction": true});
            skArc(sketch, "E40.17.54.0", {"start": v(-74.5, -82.27) * mm, "mid": v(-74.2, -82.42) * mm, "end": v(-73.85, -82.37) * mm});
            skArc(sketch, "E40.21.54.0", {"start": v(-72.21, -81.9) * mm, "mid": v(-71.84, -82.23) * mm, "end": v(-71.47, -82.55) * mm});
            skArc(sketch, "E40.25.54.0", {"start": v(-72.21, -81.9) * mm, "mid": v(-72.41, -81.8) * mm, "end": v(-72.64, -81.84) * mm});
            skArc(sketch, "E40.29.54.0", {"start": v(-71.34, -82.96) * mm, "mid": v(-71.34, -82.74) * mm, "end": v(-71.47, -82.55) * mm});
            skLineSegment(sketch, "E40.3.55.0", {"start": v(-67.55, -86.08) * mm, "end": v(-67.86, -87.38) * mm});
            skPoint(sketch, "E40.6.55.0", {"position": v(-67.95, -87.75) * mm});
            skPoint(sketch, "E40.7.55.0", {"position": v(-68.66, -84.9) * mm});
            skPoint(sketch, "E40.8.55.0", {"position": v(-67.49, -85.83) * mm});
            skPoint(sketch, "E40.9.55.0", {"position": v(-70.43, -85.78) * mm});
            skLineSegment(sketch, "E40.10.55.0", {"start": v(-68.9, -85.01) * mm, "end": v(-70.08, -85.6) * mm});
            skArc(sketch, "E40.13.55.0", {"start": v(-67.86, -87.38) * mm, "mid": v(-67.85, -87.72) * mm, "end": v(-67.64, -88) * mm});
            skLineSegment(sketch, "E40.14.55.0", {"start": v(-68.08, -85.37) * mm, "end": v(-69.2, -86.77) * mm, "construction": true});
            skArc(sketch, "E40.17.55.0", {"start": v(-70.73, -85.53) * mm, "mid": v(-70.42, -85.66) * mm, "end": v(-70.08, -85.6) * mm});
            skArc(sketch, "E40.21.55.0", {"start": v(-68.46, -85.06) * mm, "mid": v(-68.08, -85.37) * mm, "end": v(-67.7, -85.67) * mm});
            skArc(sketch, "E40.25.55.0", {"start": v(-68.46, -85.06) * mm, "mid": v(-68.67, -84.97) * mm, "end": v(-68.9, -85.01) * mm});
            skArc(sketch, "E40.29.55.0", {"start": v(-67.55, -86.08) * mm, "mid": v(-67.56, -85.86) * mm, "end": v(-67.7, -85.67) * mm});
            skLineSegment(sketch, "E40.3.56.0", {"start": v(-63.62, -89.03) * mm, "end": v(-63.87, -90.33) * mm});
            skPoint(sketch, "E40.6.56.0", {"position": v(-63.95, -90.71) * mm});
            skPoint(sketch, "E40.7.56.0", {"position": v(-64.78, -87.9) * mm});
            skPoint(sketch, "E40.8.56.0", {"position": v(-63.57, -88.77) * mm});
            skPoint(sketch, "E40.9.56.0", {"position": v(-66.51, -88.85) * mm});
            skLineSegment(sketch, "E40.10.56.0", {"start": v(-65, -88.02) * mm, "end": v(-66.17, -88.66) * mm});
            skArc(sketch, "E40.13.56.0", {"start": v(-63.87, -90.33) * mm, "mid": v(-63.84, -90.67) * mm, "end": v(-63.63, -90.94) * mm});
            skLineSegment(sketch, "E40.14.56.0", {"start": v(-64.18, -88.34) * mm, "end": v(-65.24, -89.8) * mm, "construction": true});
            skArc(sketch, "E40.17.56.0", {"start": v(-66.83, -88.62) * mm, "mid": v(-66.5, -88.74) * mm, "end": v(-66.17, -88.66) * mm});
            skArc(sketch, "E40.21.56.0", {"start": v(-64.58, -88.04) * mm, "mid": v(-64.18, -88.34) * mm, "end": v(-63.78, -88.62) * mm});
            skArc(sketch, "E40.25.56.0", {"start": v(-64.58, -88.04) * mm, "mid": v(-64.79, -87.97) * mm, "end": v(-65, -88.02) * mm});
            skArc(sketch, "E40.29.56.0", {"start": v(-63.62, -89.03) * mm, "mid": v(-63.64, -88.8) * mm, "end": v(-63.78, -88.62) * mm});
            skLineSegment(sketch, "E40.3.57.0", {"start": v(-59.56, -91.8) * mm, "end": v(-59.76, -93.1) * mm});
            skPoint(sketch, "E40.6.57.0", {"position": v(-59.81, -93.5) * mm});
            skPoint(sketch, "E40.7.57.0", {"position": v(-60.78, -90.71) * mm});
            skPoint(sketch, "E40.8.57.0", {"position": v(-59.52, -91.54) * mm});
            skPoint(sketch, "E40.9.57.0", {"position": v(-62.46, -91.75) * mm});
            skLineSegment(sketch, "E40.10.57.0", {"start": v(-61, -90.84) * mm, "end": v(-62.13, -91.54) * mm});
            skArc(sketch, "E40.13.57.0", {"start": v(-59.76, -93.1) * mm, "mid": v(-59.7, -93.44) * mm, "end": v(-59.49, -93.7) * mm});
            skLineSegment(sketch, "E40.14.57.0", {"start": v(-60.15, -91.13) * mm, "end": v(-61.14, -92.63) * mm, "construction": true});
            skArc(sketch, "E40.17.57.0", {"start": v(-62.78, -91.53) * mm, "mid": v(-62.46, -91.63) * mm, "end": v(-62.13, -91.54) * mm});
            skArc(sketch, "E40.21.57.0", {"start": v(-60.56, -90.85) * mm, "mid": v(-60.15, -91.13) * mm, "end": v(-59.74, -91.4) * mm});
            skArc(sketch, "E40.25.57.0", {"start": v(-60.56, -90.85) * mm, "mid": v(-60.78, -90.79) * mm, "end": v(-61, -90.84) * mm});
            skArc(sketch, "E40.29.57.0", {"start": v(-59.56, -91.8) * mm, "mid": v(-59.6, -91.57) * mm, "end": v(-59.74, -91.4) * mm});
            skLineSegment(sketch, "E40.3.58.0", {"start": v(-55.38, -94.37) * mm, "end": v(-55.52, -95.7) * mm});
            skPoint(sketch, "E40.6.58.0", {"position": v(-55.56, -96.08) * mm});
            skPoint(sketch, "E40.7.58.0", {"position": v(-56.65, -93.35) * mm});
            skPoint(sketch, "E40.8.58.0", {"position": v(-55.36, -94.12) * mm});
            skPoint(sketch, "E40.9.58.0", {"position": v(-58.28, -94.46) * mm});
            skLineSegment(sketch, "E40.10.58.0", {"start": v(-56.86, -93.49) * mm, "end": v(-57.96, -94.24) * mm});
            skArc(sketch, "E40.13.58.0", {"start": v(-55.52, -95.7) * mm, "mid": v(-55.46, -96.03) * mm, "end": v(-55.22, -96.28) * mm});
            skLineSegment(sketch, "E40.14.58.0", {"start": v(-56, -93.73) * mm, "end": v(-56.93, -95.28) * mm, "construction": true});
            skArc(sketch, "E40.17.58.0", {"start": v(-58.61, -94.25) * mm, "mid": v(-58.28, -94.34) * mm, "end": v(-57.96, -94.24) * mm});
            skArc(sketch, "E40.21.58.0", {"start": v(-56.43, -93.48) * mm, "mid": v(-56, -93.73) * mm, "end": v(-55.58, -93.99) * mm});
            skArc(sketch, "E40.25.58.0", {"start": v(-56.43, -93.48) * mm, "mid": v(-56.64, -93.42) * mm, "end": v(-56.86, -93.49) * mm});
            skArc(sketch, "E40.29.58.0", {"start": v(-55.38, -94.37) * mm, "mid": v(-55.42, -94.15) * mm, "end": v(-55.58, -93.99) * mm});
            skLineSegment(sketch, "E40.3.59.0", {"start": v(-51.1, -96.76) * mm, "end": v(-51.17, -98.09) * mm});
            skPoint(sketch, "E40.6.59.0", {"position": v(-51.2, -98.48) * mm});
            skPoint(sketch, "E40.7.59.0", {"position": v(-52.4, -95.8) * mm});
            skPoint(sketch, "E40.8.59.0", {"position": v(-51.08, -96.5) * mm});
            skPoint(sketch, "E40.9.59.0", {"position": v(-53.98, -96.97) * mm});
            skLineSegment(sketch, "E40.10.59.0", {"start": v(-52.6, -95.95) * mm, "end": v(-53.67, -96.74) * mm});
            skArc(sketch, "E40.13.59.0", {"start": v(-51.17, -98.09) * mm, "mid": v(-51.1, -98.42) * mm, "end": v(-50.85, -98.66) * mm});
            skLineSegment(sketch, "E40.14.59.0", {"start": v(-51.74, -96.15) * mm, "end": v(-52.6, -97.74) * mm, "construction": true});
            skArc(sketch, "E40.17.59.0", {"start": v(-54.33, -96.78) * mm, "mid": v(-54, -96.86) * mm, "end": v(-53.67, -96.74) * mm});
            skArc(sketch, "E40.21.59.0", {"start": v(-52.18, -95.92) * mm, "mid": v(-51.74, -96.15) * mm, "end": v(-51.3, -96.38) * mm});
            skArc(sketch, "E40.25.59.0", {"start": v(-52.18, -95.92) * mm, "mid": v(-52.4, -95.87) * mm, "end": v(-52.6, -95.95) * mm});
            skArc(sketch, "E40.29.59.0", {"start": v(-51.1, -96.76) * mm, "mid": v(-51.14, -96.54) * mm, "end": v(-51.3, -96.38) * mm});
            skLineSegment(sketch, "E40.3.60.0", {"start": v(-46.7, -98.95) * mm, "end": v(-46.72, -100.29) * mm});
            skPoint(sketch, "E40.6.60.0", {"position": v(-46.72, -100.67) * mm});
            skPoint(sketch, "E40.7.60.0", {"position": v(-48.05, -98.05) * mm});
            skPoint(sketch, "E40.8.60.0", {"position": v(-46.7, -98.7) * mm});
            skPoint(sketch, "E40.9.60.0", {"position": v(-49.58, -99.3) * mm});
            skLineSegment(sketch, "E40.10.60.0", {"start": v(-48.25, -98.21) * mm, "end": v(-49.28, -99.05) * mm});
            skArc(sketch, "E40.13.60.0", {"start": v(-46.72, -100.29) * mm, "mid": v(-46.63, -100.61) * mm, "end": v(-46.37, -100.84) * mm});
            skLineSegment(sketch, "E40.14.60.0", {"start": v(-47.38, -98.38) * mm, "end": v(-48.16, -100) * mm, "construction": true});
            skArc(sketch, "E40.17.60.0", {"start": v(-49.93, -99.12) * mm, "mid": v(-49.6, -99.18) * mm, "end": v(-49.28, -99.05) * mm});
            skArc(sketch, "E40.21.60.0", {"start": v(-47.82, -98.16) * mm, "mid": v(-47.38, -98.38) * mm, "end": v(-46.93, -98.59) * mm});
            skArc(sketch, "E40.25.60.0", {"start": v(-47.82, -98.16) * mm, "mid": v(-48.04, -98.12) * mm, "end": v(-48.25, -98.21) * mm});
            skArc(sketch, "E40.29.60.0", {"start": v(-46.7, -98.95) * mm, "mid": v(-46.76, -98.74) * mm, "end": v(-46.93, -98.59) * mm});
            skLineSegment(sketch, "E40.3.61.0", {"start": v(-42.21, -100.95) * mm, "end": v(-42.17, -102.28) * mm});
            skPoint(sketch, "E40.6.61.0", {"position": v(-42.16, -102.67) * mm});
            skPoint(sketch, "E40.7.61.0", {"position": v(-43.6, -100.1) * mm});
            skPoint(sketch, "E40.8.61.0", {"position": v(-42.22, -100.7) * mm});
            skPoint(sketch, "E40.9.61.0", {"position": v(-45.07, -101.42) * mm});
            skLineSegment(sketch, "E40.10.61.0", {"start": v(-43.8, -100.28) * mm, "end": v(-44.78, -101.16) * mm});
            skArc(sketch, "E40.13.61.0", {"start": v(-42.17, -102.28) * mm, "mid": v(-42.06, -102.6) * mm, "end": v(-41.8, -102.82) * mm});
            skLineSegment(sketch, "E40.14.61.0", {"start": v(-42.91, -100.4) * mm, "end": v(-43.62, -102.06) * mm, "construction": true});
            skArc(sketch, "E40.17.61.0", {"start": v(-45.43, -101.26) * mm, "mid": v(-45.1, -101.3) * mm, "end": v(-44.78, -101.16) * mm});
            skArc(sketch, "E40.21.61.0", {"start": v(-43.37, -100.2) * mm, "mid": v(-42.91, -100.4) * mm, "end": v(-42.46, -100.6) * mm});
            skArc(sketch, "E40.25.61.0", {"start": v(-43.37, -100.2) * mm, "mid": v(-43.6, -100.18) * mm, "end": v(-43.8, -100.28) * mm});
            skArc(sketch, "E40.29.61.0", {"start": v(-42.21, -100.95) * mm, "mid": v(-42.28, -100.74) * mm, "end": v(-42.46, -100.6) * mm});
            skLineSegment(sketch, "E40.3.62.0", {"start": v(-37.64, -102.74) * mm, "end": v(-37.54, -104.07) * mm});
            skPoint(sketch, "E40.6.62.0", {"position": v(-37.51, -104.46) * mm});
            skPoint(sketch, "E40.7.62.0", {"position": v(-39.07, -101.96) * mm});
            skPoint(sketch, "E40.8.62.0", {"position": v(-37.66, -102.49) * mm});
            skPoint(sketch, "E40.9.62.0", {"position": v(-40.48, -103.34) * mm});
            skLineSegment(sketch, "E40.10.62.0", {"start": v(-39.25, -102.14) * mm, "end": v(-40.2, -103.07) * mm});
            skArc(sketch, "E40.13.62.0", {"start": v(-37.54, -104.07) * mm, "mid": v(-37.42, -104.39) * mm, "end": v(-37.14, -104.59) * mm});
            skLineSegment(sketch, "E40.14.62.0", {"start": v(-38.37, -102.23) * mm, "end": v(-39, -103.91) * mm, "construction": true});
            skArc(sketch, "E40.17.62.0", {"start": v(-40.84, -103.2) * mm, "mid": v(-40.5, -103.23) * mm, "end": v(-40.2, -103.07) * mm});
            skArc(sketch, "E40.21.62.0", {"start": v(-38.83, -102.05) * mm, "mid": v(-38.37, -102.23) * mm, "end": v(-37.9, -102.4) * mm});
            skArc(sketch, "E40.25.62.0", {"start": v(-38.83, -102.05) * mm, "mid": v(-39.05, -102.03) * mm, "end": v(-39.25, -102.14) * mm});
            skArc(sketch, "E40.29.62.0", {"start": v(-37.64, -102.74) * mm, "mid": v(-37.72, -102.53) * mm, "end": v(-37.9, -102.4) * mm});
            skLineSegment(sketch, "E40.3.63.0", {"start": v(-33, -104.33) * mm, "end": v(-32.83, -105.65) * mm});
            skPoint(sketch, "E40.6.63.0", {"position": v(-32.79, -106.04) * mm});
            skPoint(sketch, "E40.7.63.0", {"position": v(-34.45, -103.61) * mm});
            skPoint(sketch, "E40.8.63.0", {"position": v(-33.03, -104.07) * mm});
            skPoint(sketch, "E40.9.63.0", {"position": v(-35.8, -105.06) * mm});
            skLineSegment(sketch, "E40.10.63.0", {"start": v(-34.63, -103.8) * mm, "end": v(-35.54, -104.77) * mm});
            skArc(sketch, "E40.13.63.0", {"start": v(-32.83, -105.65) * mm, "mid": v(-32.7, -105.96) * mm, "end": v(-32.41, -106.15) * mm});
            skLineSegment(sketch, "E40.14.63.0", {"start": v(-33.74, -103.84) * mm, "end": v(-34.3, -105.56) * mm, "construction": true});
            skArc(sketch, "E40.17.63.0", {"start": v(-36.17, -104.93) * mm, "mid": v(-35.83, -104.94) * mm, "end": v(-35.54, -104.77) * mm});
            skArc(sketch, "E40.21.63.0", {"start": v(-34.21, -103.7) * mm, "mid": v(-33.74, -103.84) * mm, "end": v(-33.27, -104) * mm});
            skArc(sketch, "E40.25.63.0", {"start": v(-34.21, -103.7) * mm, "mid": v(-34.44, -103.68) * mm, "end": v(-34.63, -103.8) * mm});
            skArc(sketch, "E40.29.63.0", {"start": v(-33, -104.33) * mm, "mid": v(-33.08, -104.12) * mm, "end": v(-33.27, -104) * mm});
            skLineSegment(sketch, "E40.3.64.0", {"start": v(-28.28, -105.7) * mm, "end": v(-28.06, -107.02) * mm});
            skPoint(sketch, "E40.6.64.0", {"position": v(-28, -107.4) * mm});
            skPoint(sketch, "E40.7.64.0", {"position": v(-29.77, -105.05) * mm});
            skPoint(sketch, "E40.8.64.0", {"position": v(-28.32, -105.45) * mm});
            skPoint(sketch, "E40.9.64.0", {"position": v(-31.05, -106.56) * mm});
            skLineSegment(sketch, "E40.10.64.0", {"start": v(-29.94, -105.25) * mm, "end": v(-30.8, -106.26) * mm});
            skArc(sketch, "E40.13.64.0", {"start": v(-28.06, -107.02) * mm, "mid": v(-27.91, -107.32) * mm, "end": v(-27.62, -107.5) * mm});
            skLineSegment(sketch, "E40.14.64.0", {"start": v(-29.05, -105.25) * mm, "end": v(-29.53, -106.99) * mm, "construction": true});
            skArc(sketch, "E40.17.64.0", {"start": v(-31.43, -106.45) * mm, "mid": v(-31.09, -106.45) * mm, "end": v(-30.8, -106.26) * mm});
            skArc(sketch, "E40.21.64.0", {"start": v(-29.52, -105.12) * mm, "mid": v(-29.05, -105.25) * mm, "end": v(-28.57, -105.38) * mm});
            skArc(sketch, "E40.25.64.0", {"start": v(-29.52, -105.12) * mm, "mid": v(-29.75, -105.12) * mm, "end": v(-29.94, -105.25) * mm});
            skArc(sketch, "E40.29.64.0", {"start": v(-28.28, -105.7) * mm, "mid": v(-28.38, -105.5) * mm, "end": v(-28.57, -105.38) * mm});
            skLineSegment(sketch, "E40.3.65.0", {"start": v(-23.51, -106.87) * mm, "end": v(-23.23, -108.17) * mm});
            skPoint(sketch, "E40.6.65.0", {"position": v(-23.15, -108.55) * mm});
            skPoint(sketch, "E40.7.65.0", {"position": v(-25.03, -106.28) * mm});
            skPoint(sketch, "E40.8.65.0", {"position": v(-23.56, -106.62) * mm});
            skPoint(sketch, "E40.9.65.0", {"position": v(-26.24, -107.84) * mm});
            skLineSegment(sketch, "E40.10.65.0", {"start": v(-25.18, -106.48) * mm, "end": v(-26, -107.53) * mm});
            skArc(sketch, "E40.13.65.0", {"start": v(-23.23, -108.17) * mm, "mid": v(-23.07, -108.47) * mm, "end": v(-22.77, -108.63) * mm});
            skLineSegment(sketch, "E40.14.65.0", {"start": v(-24.3, -106.45) * mm, "end": v(-24.7, -108.2) * mm, "construction": true});
            skArc(sketch, "E40.17.65.0", {"start": v(-26.62, -107.75) * mm, "mid": v(-26.28, -107.73) * mm, "end": v(-26, -107.53) * mm});
            skArc(sketch, "E40.21.65.0", {"start": v(-24.78, -106.34) * mm, "mid": v(-24.3, -106.45) * mm, "end": v(-23.81, -106.56) * mm});
            skArc(sketch, "E40.25.65.0", {"start": v(-24.78, -106.34) * mm, "mid": v(-25, -106.35) * mm, "end": v(-25.18, -106.48) * mm});
            skArc(sketch, "E40.29.65.0", {"start": v(-23.51, -106.87) * mm, "mid": v(-23.62, -106.67) * mm, "end": v(-23.81, -106.56) * mm});
            skLineSegment(sketch, "E40.3.66.0", {"start": v(-18.7, -107.81) * mm, "end": v(-18.35, -109.1) * mm});
            skPoint(sketch, "E40.6.66.0", {"position": v(-18.26, -109.48) * mm});
            skPoint(sketch, "E40.7.66.0", {"position": v(-20.23, -107.3) * mm});
            skPoint(sketch, "E40.8.66.0", {"position": v(-18.76, -107.57) * mm});
            skPoint(sketch, "E40.9.66.0", {"position": v(-21.38, -108.91) * mm});
            skLineSegment(sketch, "E40.10.66.0", {"start": v(-20.38, -107.5) * mm, "end": v(-21.15, -108.6) * mm});
            skArc(sketch, "E40.13.66.0", {"start": v(-18.35, -109.1) * mm, "mid": v(-18.18, -109.4) * mm, "end": v(-17.87, -109.54) * mm});
            skLineSegment(sketch, "E40.14.66.0", {"start": v(-19.5, -107.43) * mm, "end": v(-19.82, -109.2) * mm, "construction": true});
            skArc(sketch, "E40.17.66.0", {"start": v(-21.76, -108.83) * mm, "mid": v(-21.42, -108.8) * mm, "end": v(-21.15, -108.6) * mm});
            skArc(sketch, "E40.21.66.0", {"start": v(-19.98, -107.34) * mm, "mid": v(-19.5, -107.43) * mm, "end": v(-19.01, -107.52) * mm});
            skArc(sketch, "E40.25.66.0", {"start": v(-19.98, -107.34) * mm, "mid": v(-20.2, -107.37) * mm, "end": v(-20.38, -107.5) * mm});
            skArc(sketch, "E40.29.66.0", {"start": v(-18.7, -107.81) * mm, "mid": v(-18.8, -107.62) * mm, "end": v(-19.01, -107.52) * mm});
            skLineSegment(sketch, "E40.3.67.0", {"start": v(-13.84, -108.54) * mm, "end": v(-13.44, -109.81) * mm});
            skPoint(sketch, "E40.6.67.0", {"position": v(-13.33, -110.19) * mm});
            skPoint(sketch, "E40.7.67.0", {"position": v(-15.4, -108.1) * mm});
            skPoint(sketch, "E40.8.67.0", {"position": v(-13.91, -108.3) * mm});
            skPoint(sketch, "E40.9.67.0", {"position": v(-16.47, -109.76) * mm});
            skLineSegment(sketch, "E40.10.67.0", {"start": v(-15.54, -108.31) * mm, "end": v(-16.26, -109.43) * mm});
            skArc(sketch, "E40.13.67.0", {"start": v(-13.44, -109.81) * mm, "mid": v(-13.25, -110.1) * mm, "end": v(-12.94, -110.23) * mm});
            skLineSegment(sketch, "E40.14.67.0", {"start": v(-14.66, -108.2) * mm, "end": v(-14.9, -109.98) * mm, "construction": true});
            skArc(sketch, "E40.17.67.0", {"start": v(-16.85, -109.7) * mm, "mid": v(-16.52, -109.66) * mm, "end": v(-16.26, -109.43) * mm});
            skArc(sketch, "E40.21.67.0", {"start": v(-15.15, -108.13) * mm, "mid": v(-14.66, -108.2) * mm, "end": v(-14.17, -108.27) * mm});
            skArc(sketch, "E40.25.67.0", {"start": v(-15.15, -108.13) * mm, "mid": v(-15.37, -108.17) * mm, "end": v(-15.54, -108.31) * mm});
            skArc(sketch, "E40.29.67.0", {"start": v(-13.84, -108.54) * mm, "mid": v(-13.96, -108.36) * mm, "end": v(-14.17, -108.27) * mm});
            skLineSegment(sketch, "E40.3.68.0", {"start": v(-8.95, -109.05) * mm, "end": v(-8.5, -110.3) * mm});
            skPoint(sketch, "E40.6.68.0", {"position": v(-8.37, -110.67) * mm});
            skPoint(sketch, "E40.7.68.0", {"position": v(-10.53, -108.68) * mm});
            skPoint(sketch, "E40.8.68.0", {"position": v(-9.04, -108.81) * mm});
            skPoint(sketch, "E40.9.68.0", {"position": v(-11.53, -110.39) * mm});
            skLineSegment(sketch, "E40.10.68.0", {"start": v(-10.66, -108.9) * mm, "end": v(-11.33, -110.05) * mm});
            skArc(sketch, "E40.13.68.0", {"start": v(-8.5, -110.3) * mm, "mid": v(-8.3, -110.58) * mm, "end": v(-7.98, -110.7) * mm});
            skLineSegment(sketch, "E40.14.68.0", {"start": v(-9.79, -108.75) * mm, "end": v(-9.95, -110.54) * mm, "construction": true});
            skArc(sketch, "E40.17.68.0", {"start": v(-11.91, -110.35) * mm, "mid": v(-11.58, -110.29) * mm, "end": v(-11.33, -110.05) * mm});
            skArc(sketch, "E40.21.68.0", {"start": v(-10.28, -108.7) * mm, "mid": v(-9.79, -108.75) * mm, "end": v(-9.3, -108.8) * mm});
            skArc(sketch, "E40.25.68.0", {"start": v(-10.28, -108.7) * mm, "mid": v(-10.5, -108.75) * mm, "end": v(-10.66, -108.9) * mm});
            skArc(sketch, "E40.29.68.0", {"start": v(-8.95, -109.05) * mm, "mid": v(-9.09, -108.87) * mm, "end": v(-9.3, -108.8) * mm});
            skLineSegment(sketch, "E40.3.69.0", {"start": v(-4.05, -109.35) * mm, "end": v(-3.54, -110.58) * mm});
            skPoint(sketch, "E40.6.69.0", {"position": v(-3.4, -110.94) * mm});
            skPoint(sketch, "E40.7.69.0", {"position": v(-5.65, -109.04) * mm});
            skPoint(sketch, "E40.8.69.0", {"position": v(-4.15, -109.1) * mm});
            skPoint(sketch, "E40.9.69.0", {"position": v(-6.56, -110.8) * mm});
            skLineSegment(sketch, "E40.10.69.0", {"start": v(-5.77, -109.27) * mm, "end": v(-6.38, -110.45) * mm});
            skArc(sketch, "E40.13.69.0", {"start": v(-3.54, -110.58) * mm, "mid": v(-3.33, -110.84) * mm, "end": v(-3, -110.95) * mm});
            skLineSegment(sketch, "E40.14.69.0", {"start": v(-4.9, -109.08) * mm, "end": v(-4.98, -110.88) * mm, "construction": true});
            skArc(sketch, "E40.17.69.0", {"start": v(-6.95, -110.77) * mm, "mid": v(-6.62, -110.7) * mm, "end": v(-6.38, -110.45) * mm});
            skArc(sketch, "E40.21.69.0", {"start": v(-5.4, -109.06) * mm, "mid": v(-4.9, -109.08) * mm, "end": v(-4.4, -109.1) * mm});
            skArc(sketch, "E40.25.69.0", {"start": v(-5.4, -109.06) * mm, "mid": v(-5.61, -109.1) * mm, "end": v(-5.77, -109.27) * mm});
            skArc(sketch, "E40.29.69.0", {"start": v(-4.05, -109.35) * mm, "mid": v(-4.2, -109.17) * mm, "end": v(-4.4, -109.1) * mm});
            skLineSegment(sketch, "E40.3.70.0", {"start": v(0.86, -109.42) * mm, "end": v(1.42, -110.62) * mm});
            skPoint(sketch, "E40.6.70.0", {"position": v(1.59, -110.98) * mm});
            skPoint(sketch, "E40.7.70.0", {"position": v(-0.75, -109.19) * mm});
            skPoint(sketch, "E40.8.70.0", {"position": v(0.75, -109.19) * mm});
            skPoint(sketch, "E40.9.70.0", {"position": v(-1.59, -110.98) * mm});
            skLineSegment(sketch, "E40.10.70.0", {"start": v(-0.86, -109.42) * mm, "end": v(-1.42, -110.62) * mm});
            skArc(sketch, "E40.13.70.0", {"start": v(1.42, -110.62) * mm, "mid": v(1.65, -110.88) * mm, "end": v(1.98, -110.97) * mm});
            skLineSegment(sketch, "E40.14.70.0", {"start": v(0, -109.19) * mm, "end": v(0, -110.99) * mm, "construction": true});
            skArc(sketch, "E40.17.70.0", {"start": v(-1.98, -110.97) * mm, "mid": v(-1.65, -110.88) * mm, "end": v(-1.42, -110.62) * mm});
            skArc(sketch, "E40.21.70.0", {"start": v(-0.5, -109.19) * mm, "mid": v(0, -109.19) * mm, "end": v(0.5, -109.19) * mm});
            skArc(sketch, "E40.25.70.0", {"start": v(-0.5, -109.19) * mm, "mid": v(-0.71, -109.25) * mm, "end": v(-0.86, -109.42) * mm});
            skArc(sketch, "E40.29.70.0", {"start": v(0.86, -109.42) * mm, "mid": v(0.71, -109.25) * mm, "end": v(0.5, -109.19) * mm});
            skLineSegment(sketch, "E40.3.71.0", {"start": v(5.77, -109.27) * mm, "end": v(6.38, -110.45) * mm});
            skPoint(sketch, "E40.6.71.0", {"position": v(6.56, -110.8) * mm});
            skPoint(sketch, "E40.7.71.0", {"position": v(4.15, -109.1) * mm});
            skPoint(sketch, "E40.8.71.0", {"position": v(5.65, -109.04) * mm});
            skPoint(sketch, "E40.9.71.0", {"position": v(3.4, -110.94) * mm});
            skLineSegment(sketch, "E40.10.71.0", {"start": v(4.05, -109.35) * mm, "end": v(3.54, -110.58) * mm});
            skArc(sketch, "E40.13.71.0", {"start": v(6.38, -110.45) * mm, "mid": v(6.62, -110.7) * mm, "end": v(6.95, -110.77) * mm});
            skLineSegment(sketch, "E40.14.71.0", {"start": v(4.9, -109.08) * mm, "end": v(4.98, -110.88) * mm, "construction": true});
            skArc(sketch, "E40.17.71.0", {"start": v(3, -110.95) * mm, "mid": v(3.33, -110.84) * mm, "end": v(3.54, -110.58) * mm});
            skArc(sketch, "E40.21.71.0", {"start": v(4.4, -109.1) * mm, "mid": v(4.9, -109.08) * mm, "end": v(5.4, -109.06) * mm});
            skArc(sketch, "E40.25.71.0", {"start": v(4.4, -109.1) * mm, "mid": v(4.2, -109.17) * mm, "end": v(4.05, -109.35) * mm});
            skArc(sketch, "E40.29.71.0", {"start": v(5.77, -109.27) * mm, "mid": v(5.61, -109.1) * mm, "end": v(5.4, -109.06) * mm});
            skLineSegment(sketch, "E40.3.72.0", {"start": v(10.66, -108.9) * mm, "end": v(11.33, -110.05) * mm});
            skPoint(sketch, "E40.6.72.0", {"position": v(11.53, -110.39) * mm});
            skPoint(sketch, "E40.7.72.0", {"position": v(9.04, -108.81) * mm});
            skPoint(sketch, "E40.8.72.0", {"position": v(10.53, -108.68) * mm});
            skPoint(sketch, "E40.9.72.0", {"position": v(8.37, -110.67) * mm});
            skLineSegment(sketch, "E40.10.72.0", {"start": v(8.95, -109.05) * mm, "end": v(8.5, -110.3) * mm});
            skArc(sketch, "E40.13.72.0", {"start": v(11.33, -110.05) * mm, "mid": v(11.58, -110.29) * mm, "end": v(11.91, -110.35) * mm});
            skLineSegment(sketch, "E40.14.72.0", {"start": v(9.79, -108.75) * mm, "end": v(9.95, -110.54) * mm, "construction": true});
            skArc(sketch, "E40.17.72.0", {"start": v(7.98, -110.7) * mm, "mid": v(8.3, -110.58) * mm, "end": v(8.5, -110.3) * mm});
            skArc(sketch, "E40.21.72.0", {"start": v(9.3, -108.8) * mm, "mid": v(9.79, -108.75) * mm, "end": v(10.28, -108.7) * mm});
            skArc(sketch, "E40.25.72.0", {"start": v(9.3, -108.8) * mm, "mid": v(9.09, -108.87) * mm, "end": v(8.95, -109.05) * mm});
            skArc(sketch, "E40.29.72.0", {"start": v(10.66, -108.9) * mm, "mid": v(10.5, -108.75) * mm, "end": v(10.28, -108.7) * mm});
            skLineSegment(sketch, "E40.3.73.0", {"start": v(15.54, -108.31) * mm, "end": v(16.26, -109.43) * mm});
            skPoint(sketch, "E40.6.73.0", {"position": v(16.47, -109.76) * mm});
            skPoint(sketch, "E40.7.73.0", {"position": v(13.91, -108.3) * mm});
            skPoint(sketch, "E40.8.73.0", {"position": v(15.4, -108.1) * mm});
            skPoint(sketch, "E40.9.73.0", {"position": v(13.33, -110.19) * mm});
            skLineSegment(sketch, "E40.10.73.0", {"start": v(13.84, -108.54) * mm, "end": v(13.44, -109.81) * mm});
            skArc(sketch, "E40.13.73.0", {"start": v(16.26, -109.43) * mm, "mid": v(16.52, -109.66) * mm, "end": v(16.85, -109.7) * mm});
            skLineSegment(sketch, "E40.14.73.0", {"start": v(14.66, -108.2) * mm, "end": v(14.9, -109.98) * mm, "construction": true});
            skArc(sketch, "E40.17.73.0", {"start": v(12.94, -110.23) * mm, "mid": v(13.25, -110.1) * mm, "end": v(13.44, -109.81) * mm});
            skArc(sketch, "E40.21.73.0", {"start": v(14.17, -108.27) * mm, "mid": v(14.66, -108.2) * mm, "end": v(15.15, -108.13) * mm});
            skArc(sketch, "E40.25.73.0", {"start": v(14.17, -108.27) * mm, "mid": v(13.96, -108.36) * mm, "end": v(13.84, -108.54) * mm});
            skArc(sketch, "E40.29.73.0", {"start": v(15.54, -108.31) * mm, "mid": v(15.37, -108.17) * mm, "end": v(15.15, -108.13) * mm});
            skLineSegment(sketch, "E40.3.74.0", {"start": v(20.38, -107.5) * mm, "end": v(21.15, -108.6) * mm});
            skPoint(sketch, "E40.6.74.0", {"position": v(21.38, -108.91) * mm});
            skPoint(sketch, "E40.7.74.0", {"position": v(18.76, -107.57) * mm});
            skPoint(sketch, "E40.8.74.0", {"position": v(20.23, -107.3) * mm});
            skPoint(sketch, "E40.9.74.0", {"position": v(18.26, -109.48) * mm});
            skLineSegment(sketch, "E40.10.74.0", {"start": v(18.7, -107.81) * mm, "end": v(18.35, -109.1) * mm});
            skArc(sketch, "E40.13.74.0", {"start": v(21.15, -108.6) * mm, "mid": v(21.42, -108.8) * mm, "end": v(21.76, -108.83) * mm});
            skLineSegment(sketch, "E40.14.74.0", {"start": v(19.5, -107.43) * mm, "end": v(19.82, -109.2) * mm, "construction": true});
            skArc(sketch, "E40.17.74.0", {"start": v(17.87, -109.54) * mm, "mid": v(18.18, -109.4) * mm, "end": v(18.35, -109.1) * mm});
            skArc(sketch, "E40.21.74.0", {"start": v(19.01, -107.52) * mm, "mid": v(19.5, -107.43) * mm, "end": v(19.98, -107.34) * mm});
            skArc(sketch, "E40.25.74.0", {"start": v(19.01, -107.52) * mm, "mid": v(18.8, -107.62) * mm, "end": v(18.7, -107.81) * mm});
            skArc(sketch, "E40.29.74.0", {"start": v(20.38, -107.5) * mm, "mid": v(20.2, -107.37) * mm, "end": v(19.98, -107.34) * mm});
            skLineSegment(sketch, "E40.3.75.0", {"start": v(25.18, -106.48) * mm, "end": v(26, -107.53) * mm});
            skPoint(sketch, "E40.6.75.0", {"position": v(26.24, -107.84) * mm});
            skPoint(sketch, "E40.7.75.0", {"position": v(23.56, -106.62) * mm});
            skPoint(sketch, "E40.8.75.0", {"position": v(25.03, -106.28) * mm});
            skPoint(sketch, "E40.9.75.0", {"position": v(23.15, -108.55) * mm});
            skLineSegment(sketch, "E40.10.75.0", {"start": v(23.51, -106.87) * mm, "end": v(23.23, -108.17) * mm});
            skArc(sketch, "E40.13.75.0", {"start": v(26, -107.53) * mm, "mid": v(26.28, -107.73) * mm, "end": v(26.62, -107.75) * mm});
            skLineSegment(sketch, "E40.14.75.0", {"start": v(24.3, -106.45) * mm, "end": v(24.7, -108.2) * mm, "construction": true});
            skArc(sketch, "E40.17.75.0", {"start": v(22.77, -108.63) * mm, "mid": v(23.07, -108.47) * mm, "end": v(23.23, -108.17) * mm});
            skArc(sketch, "E40.21.75.0", {"start": v(23.81, -106.56) * mm, "mid": v(24.3, -106.45) * mm, "end": v(24.78, -106.34) * mm});
            skArc(sketch, "E40.25.75.0", {"start": v(23.81, -106.56) * mm, "mid": v(23.62, -106.67) * mm, "end": v(23.51, -106.87) * mm});
            skArc(sketch, "E40.29.75.0", {"start": v(25.18, -106.48) * mm, "mid": v(25, -106.35) * mm, "end": v(24.78, -106.34) * mm});
            skLineSegment(sketch, "E40.3.76.0", {"start": v(29.94, -105.25) * mm, "end": v(30.8, -106.26) * mm});
            skPoint(sketch, "E40.6.76.0", {"position": v(31.05, -106.56) * mm});
            skPoint(sketch, "E40.7.76.0", {"position": v(28.32, -105.45) * mm});
            skPoint(sketch, "E40.8.76.0", {"position": v(29.77, -105.05) * mm});
            skPoint(sketch, "E40.9.76.0", {"position": v(28, -107.4) * mm});
            skLineSegment(sketch, "E40.10.76.0", {"start": v(28.28, -105.7) * mm, "end": v(28.06, -107.02) * mm});
            skArc(sketch, "E40.13.76.0", {"start": v(30.8, -106.26) * mm, "mid": v(31.09, -106.45) * mm, "end": v(31.43, -106.45) * mm});
            skLineSegment(sketch, "E40.14.76.0", {"start": v(29.05, -105.25) * mm, "end": v(29.53, -106.99) * mm, "construction": true});
            skArc(sketch, "E40.17.76.0", {"start": v(27.62, -107.5) * mm, "mid": v(27.91, -107.32) * mm, "end": v(28.06, -107.02) * mm});
            skArc(sketch, "E40.21.76.0", {"start": v(28.57, -105.38) * mm, "mid": v(29.05, -105.25) * mm, "end": v(29.52, -105.12) * mm});
            skArc(sketch, "E40.25.76.0", {"start": v(28.57, -105.38) * mm, "mid": v(28.38, -105.5) * mm, "end": v(28.28, -105.7) * mm});
            skArc(sketch, "E40.29.76.0", {"start": v(29.94, -105.25) * mm, "mid": v(29.75, -105.12) * mm, "end": v(29.52, -105.12) * mm});
            skLineSegment(sketch, "E40.3.77.0", {"start": v(34.63, -103.8) * mm, "end": v(35.54, -104.77) * mm});
            skPoint(sketch, "E40.6.77.0", {"position": v(35.8, -105.06) * mm});
            skPoint(sketch, "E40.7.77.0", {"position": v(33.03, -104.07) * mm});
            skPoint(sketch, "E40.8.77.0", {"position": v(34.45, -103.61) * mm});
            skPoint(sketch, "E40.9.77.0", {"position": v(32.79, -106.04) * mm});
            skLineSegment(sketch, "E40.10.77.0", {"start": v(33, -104.33) * mm, "end": v(32.83, -105.65) * mm});
            skArc(sketch, "E40.13.77.0", {"start": v(35.54, -104.77) * mm, "mid": v(35.83, -104.94) * mm, "end": v(36.17, -104.93) * mm});
            skLineSegment(sketch, "E40.14.77.0", {"start": v(33.74, -103.84) * mm, "end": v(34.3, -105.56) * mm, "construction": true});
            skArc(sketch, "E40.17.77.0", {"start": v(32.41, -106.15) * mm, "mid": v(32.7, -105.96) * mm, "end": v(32.83, -105.65) * mm});
            skArc(sketch, "E40.21.77.0", {"start": v(33.27, -104) * mm, "mid": v(33.74, -103.84) * mm, "end": v(34.21, -103.7) * mm});
            skArc(sketch, "E40.25.77.0", {"start": v(33.27, -104) * mm, "mid": v(33.08, -104.12) * mm, "end": v(33, -104.33) * mm});
            skArc(sketch, "E40.29.77.0", {"start": v(34.63, -103.8) * mm, "mid": v(34.44, -103.68) * mm, "end": v(34.21, -103.7) * mm});
            skLineSegment(sketch, "E40.3.78.0", {"start": v(39.25, -102.14) * mm, "end": v(40.2, -103.07) * mm});
            skPoint(sketch, "E40.6.78.0", {"position": v(40.48, -103.34) * mm});
            skPoint(sketch, "E40.7.78.0", {"position": v(37.66, -102.49) * mm});
            skPoint(sketch, "E40.8.78.0", {"position": v(39.07, -101.96) * mm});
            skPoint(sketch, "E40.9.78.0", {"position": v(37.51, -104.46) * mm});
            skLineSegment(sketch, "E40.10.78.0", {"start": v(37.64, -102.74) * mm, "end": v(37.54, -104.07) * mm});
            skArc(sketch, "E40.13.78.0", {"start": v(40.2, -103.07) * mm, "mid": v(40.5, -103.23) * mm, "end": v(40.84, -103.2) * mm});
            skLineSegment(sketch, "E40.14.78.0", {"start": v(38.37, -102.23) * mm, "end": v(39, -103.91) * mm, "construction": true});
            skArc(sketch, "E40.17.78.0", {"start": v(37.14, -104.59) * mm, "mid": v(37.42, -104.39) * mm, "end": v(37.54, -104.07) * mm});
            skArc(sketch, "E40.21.78.0", {"start": v(37.9, -102.4) * mm, "mid": v(38.37, -102.23) * mm, "end": v(38.83, -102.05) * mm});
            skArc(sketch, "E40.25.78.0", {"start": v(37.9, -102.4) * mm, "mid": v(37.72, -102.53) * mm, "end": v(37.64, -102.74) * mm});
            skArc(sketch, "E40.29.78.0", {"start": v(39.25, -102.14) * mm, "mid": v(39.05, -102.03) * mm, "end": v(38.83, -102.05) * mm});
            skLineSegment(sketch, "E40.3.79.0", {"start": v(43.8, -100.28) * mm, "end": v(44.78, -101.16) * mm});
            skPoint(sketch, "E40.6.79.0", {"position": v(45.07, -101.42) * mm});
            skPoint(sketch, "E40.7.79.0", {"position": v(42.22, -100.7) * mm});
            skPoint(sketch, "E40.8.79.0", {"position": v(43.6, -100.1) * mm});
            skPoint(sketch, "E40.9.79.0", {"position": v(42.16, -102.67) * mm});
            skLineSegment(sketch, "E40.10.79.0", {"start": v(42.21, -100.95) * mm, "end": v(42.17, -102.28) * mm});
            skArc(sketch, "E40.13.79.0", {"start": v(44.78, -101.16) * mm, "mid": v(45.1, -101.3) * mm, "end": v(45.43, -101.26) * mm});
            skLineSegment(sketch, "E40.14.79.0", {"start": v(42.91, -100.4) * mm, "end": v(43.62, -102.06) * mm, "construction": true});
            skArc(sketch, "E40.17.79.0", {"start": v(41.8, -102.82) * mm, "mid": v(42.06, -102.6) * mm, "end": v(42.17, -102.28) * mm});
            skArc(sketch, "E40.21.79.0", {"start": v(42.46, -100.6) * mm, "mid": v(42.91, -100.4) * mm, "end": v(43.37, -100.2) * mm});
            skArc(sketch, "E40.25.79.0", {"start": v(42.46, -100.6) * mm, "mid": v(42.28, -100.74) * mm, "end": v(42.21, -100.95) * mm});
            skArc(sketch, "E40.29.79.0", {"start": v(43.8, -100.28) * mm, "mid": v(43.6, -100.18) * mm, "end": v(43.37, -100.2) * mm});
            skLineSegment(sketch, "E40.3.80.0", {"start": v(48.25, -98.21) * mm, "end": v(49.28, -99.05) * mm});
            skPoint(sketch, "E40.6.80.0", {"position": v(49.58, -99.3) * mm});
            skPoint(sketch, "E40.7.80.0", {"position": v(46.7, -98.7) * mm});
            skPoint(sketch, "E40.8.80.0", {"position": v(48.05, -98.05) * mm});
            skPoint(sketch, "E40.9.80.0", {"position": v(46.72, -100.67) * mm});
            skLineSegment(sketch, "E40.10.80.0", {"start": v(46.7, -98.95) * mm, "end": v(46.72, -100.29) * mm});
            skArc(sketch, "E40.13.80.0", {"start": v(49.28, -99.05) * mm, "mid": v(49.6, -99.18) * mm, "end": v(49.93, -99.12) * mm});
            skLineSegment(sketch, "E40.14.80.0", {"start": v(47.38, -98.38) * mm, "end": v(48.16, -100) * mm, "construction": true});
            skArc(sketch, "E40.17.80.0", {"start": v(46.37, -100.84) * mm, "mid": v(46.63, -100.61) * mm, "end": v(46.72, -100.29) * mm});
            skArc(sketch, "E40.21.80.0", {"start": v(46.93, -98.59) * mm, "mid": v(47.38, -98.38) * mm, "end": v(47.82, -98.16) * mm});
            skArc(sketch, "E40.25.80.0", {"start": v(46.93, -98.59) * mm, "mid": v(46.76, -98.74) * mm, "end": v(46.7, -98.95) * mm});
            skArc(sketch, "E40.29.80.0", {"start": v(48.25, -98.21) * mm, "mid": v(48.04, -98.12) * mm, "end": v(47.82, -98.16) * mm});
            skLineSegment(sketch, "E40.3.81.0", {"start": v(52.6, -95.95) * mm, "end": v(53.67, -96.74) * mm});
            skPoint(sketch, "E40.6.81.0", {"position": v(53.98, -96.97) * mm});
            skPoint(sketch, "E40.7.81.0", {"position": v(51.08, -96.5) * mm});
            skPoint(sketch, "E40.8.81.0", {"position": v(52.4, -95.8) * mm});
            skPoint(sketch, "E40.9.81.0", {"position": v(51.2, -98.48) * mm});
            skLineSegment(sketch, "E40.10.81.0", {"start": v(51.1, -96.76) * mm, "end": v(51.17, -98.09) * mm});
            skArc(sketch, "E40.13.81.0", {"start": v(53.67, -96.74) * mm, "mid": v(54, -96.86) * mm, "end": v(54.33, -96.78) * mm});
            skLineSegment(sketch, "E40.14.81.0", {"start": v(51.74, -96.15) * mm, "end": v(52.6, -97.74) * mm, "construction": true});
            skArc(sketch, "E40.17.81.0", {"start": v(50.85, -98.66) * mm, "mid": v(51.1, -98.42) * mm, "end": v(51.17, -98.09) * mm});
            skArc(sketch, "E40.21.81.0", {"start": v(51.3, -96.38) * mm, "mid": v(51.74, -96.15) * mm, "end": v(52.18, -95.92) * mm});
            skArc(sketch, "E40.25.81.0", {"start": v(51.3, -96.38) * mm, "mid": v(51.14, -96.54) * mm, "end": v(51.1, -96.76) * mm});
            skArc(sketch, "E40.29.81.0", {"start": v(52.6, -95.95) * mm, "mid": v(52.4, -95.87) * mm, "end": v(52.18, -95.92) * mm});
            skLineSegment(sketch, "E40.3.82.0", {"start": v(56.86, -93.49) * mm, "end": v(57.96, -94.24) * mm});
            skPoint(sketch, "E40.6.82.0", {"position": v(58.28, -94.46) * mm});
            skPoint(sketch, "E40.7.82.0", {"position": v(55.36, -94.12) * mm});
            skPoint(sketch, "E40.8.82.0", {"position": v(56.65, -93.35) * mm});
            skPoint(sketch, "E40.9.82.0", {"position": v(55.56, -96.08) * mm});
            skLineSegment(sketch, "E40.10.82.0", {"start": v(55.38, -94.37) * mm, "end": v(55.52, -95.7) * mm});
            skArc(sketch, "E40.13.82.0", {"start": v(57.96, -94.24) * mm, "mid": v(58.28, -94.34) * mm, "end": v(58.61, -94.25) * mm});
            skLineSegment(sketch, "E40.14.82.0", {"start": v(56, -93.73) * mm, "end": v(56.93, -95.28) * mm, "construction": true});
            skArc(sketch, "E40.17.82.0", {"start": v(55.22, -96.28) * mm, "mid": v(55.46, -96.03) * mm, "end": v(55.52, -95.7) * mm});
            skArc(sketch, "E40.21.82.0", {"start": v(55.58, -93.99) * mm, "mid": v(56, -93.73) * mm, "end": v(56.43, -93.48) * mm});
            skArc(sketch, "E40.25.82.0", {"start": v(55.58, -93.99) * mm, "mid": v(55.42, -94.15) * mm, "end": v(55.38, -94.37) * mm});
            skArc(sketch, "E40.29.82.0", {"start": v(56.86, -93.49) * mm, "mid": v(56.64, -93.42) * mm, "end": v(56.43, -93.48) * mm});
            skLineSegment(sketch, "E40.3.83.0", {"start": v(61, -90.84) * mm, "end": v(62.13, -91.54) * mm});
            skPoint(sketch, "E40.6.83.0", {"position": v(62.46, -91.75) * mm});
            skPoint(sketch, "E40.7.83.0", {"position": v(59.52, -91.54) * mm});
            skPoint(sketch, "E40.8.83.0", {"position": v(60.78, -90.71) * mm});
            skPoint(sketch, "E40.9.83.0", {"position": v(59.81, -93.5) * mm});
            skLineSegment(sketch, "E40.10.83.0", {"start": v(59.56, -91.8) * mm, "end": v(59.76, -93.1) * mm});
            skArc(sketch, "E40.13.83.0", {"start": v(62.13, -91.54) * mm, "mid": v(62.46, -91.63) * mm, "end": v(62.78, -91.53) * mm});
            skLineSegment(sketch, "E40.14.83.0", {"start": v(60.15, -91.13) * mm, "end": v(61.14, -92.63) * mm, "construction": true});
            skArc(sketch, "E40.17.83.0", {"start": v(59.49, -93.7) * mm, "mid": v(59.7, -93.44) * mm, "end": v(59.76, -93.1) * mm});
            skArc(sketch, "E40.21.83.0", {"start": v(59.74, -91.4) * mm, "mid": v(60.15, -91.13) * mm, "end": v(60.56, -90.85) * mm});
            skArc(sketch, "E40.25.83.0", {"start": v(59.74, -91.4) * mm, "mid": v(59.6, -91.57) * mm, "end": v(59.56, -91.8) * mm});
            skArc(sketch, "E40.29.83.0", {"start": v(61, -90.84) * mm, "mid": v(60.78, -90.79) * mm, "end": v(60.56, -90.85) * mm});
            skLineSegment(sketch, "E40.3.84.0", {"start": v(65, -88.02) * mm, "end": v(66.17, -88.66) * mm});
            skPoint(sketch, "E40.6.84.0", {"position": v(66.51, -88.85) * mm});
            skPoint(sketch, "E40.7.84.0", {"position": v(63.57, -88.77) * mm});
            skPoint(sketch, "E40.8.84.0", {"position": v(64.78, -87.9) * mm});
            skPoint(sketch, "E40.9.84.0", {"position": v(63.95, -90.71) * mm});
            skLineSegment(sketch, "E40.10.84.0", {"start": v(63.62, -89.03) * mm, "end": v(63.87, -90.33) * mm});
            skArc(sketch, "E40.13.84.0", {"start": v(66.17, -88.66) * mm, "mid": v(66.5, -88.74) * mm, "end": v(66.83, -88.62) * mm});
            skLineSegment(sketch, "E40.14.84.0", {"start": v(64.18, -88.34) * mm, "end": v(65.24, -89.8) * mm, "construction": true});
            skArc(sketch, "E40.17.84.0", {"start": v(63.63, -90.94) * mm, "mid": v(63.84, -90.67) * mm, "end": v(63.87, -90.33) * mm});
            skArc(sketch, "E40.21.84.0", {"start": v(63.78, -88.62) * mm, "mid": v(64.18, -88.34) * mm, "end": v(64.58, -88.04) * mm});
            skArc(sketch, "E40.25.84.0", {"start": v(63.78, -88.62) * mm, "mid": v(63.64, -88.8) * mm, "end": v(63.62, -89.03) * mm});
            skArc(sketch, "E40.29.84.0", {"start": v(65, -88.02) * mm, "mid": v(64.79, -87.97) * mm, "end": v(64.58, -88.04) * mm});
            skLineSegment(sketch, "E40.3.85.0", {"start": v(68.9, -85.01) * mm, "end": v(70.08, -85.6) * mm});
            skPoint(sketch, "E40.6.85.0", {"position": v(70.43, -85.78) * mm});
            skPoint(sketch, "E40.7.85.0", {"position": v(67.49, -85.83) * mm});
            skPoint(sketch, "E40.8.85.0", {"position": v(68.66, -84.9) * mm});
            skPoint(sketch, "E40.9.85.0", {"position": v(67.95, -87.75) * mm});
            skLineSegment(sketch, "E40.10.85.0", {"start": v(67.55, -86.08) * mm, "end": v(67.86, -87.38) * mm});
            skArc(sketch, "E40.13.85.0", {"start": v(70.08, -85.6) * mm, "mid": v(70.42, -85.66) * mm, "end": v(70.73, -85.53) * mm});
            skLineSegment(sketch, "E40.14.85.0", {"start": v(68.08, -85.37) * mm, "end": v(69.2, -86.77) * mm, "construction": true});
            skArc(sketch, "E40.17.85.0", {"start": v(67.64, -88) * mm, "mid": v(67.85, -87.72) * mm, "end": v(67.86, -87.38) * mm});
            skArc(sketch, "E40.21.85.0", {"start": v(67.7, -85.67) * mm, "mid": v(68.08, -85.37) * mm, "end": v(68.46, -85.06) * mm});
            skArc(sketch, "E40.25.85.0", {"start": v(67.7, -85.67) * mm, "mid": v(67.56, -85.86) * mm, "end": v(67.55, -86.08) * mm});
            skArc(sketch, "E40.29.85.0", {"start": v(68.9, -85.01) * mm, "mid": v(68.67, -84.97) * mm, "end": v(68.46, -85.06) * mm});
            skLineSegment(sketch, "E40.3.86.0", {"start": v(72.64, -81.84) * mm, "end": v(73.85, -82.37) * mm});
            skPoint(sketch, "E40.6.86.0", {"position": v(74.21, -82.53) * mm});
            skPoint(sketch, "E40.7.86.0", {"position": v(71.27, -82.72) * mm});
            skPoint(sketch, "E40.8.86.0", {"position": v(72.4, -81.73) * mm});
            skPoint(sketch, "E40.9.86.0", {"position": v(71.82, -84.62) * mm});
            skLineSegment(sketch, "E40.10.86.0", {"start": v(71.34, -82.96) * mm, "end": v(71.71, -84.24) * mm});
            skArc(sketch, "E40.13.86.0", {"start": v(73.85, -82.37) * mm, "mid": v(74.2, -82.42) * mm, "end": v(74.5, -82.27) * mm});
            skLineSegment(sketch, "E40.14.86.0", {"start": v(71.84, -82.23) * mm, "end": v(73.02, -83.58) * mm, "construction": true});
            skArc(sketch, "E40.17.86.0", {"start": v(71.52, -84.87) * mm, "mid": v(71.71, -84.58) * mm, "end": v(71.71, -84.24) * mm});
            skArc(sketch, "E40.21.86.0", {"start": v(71.47, -82.55) * mm, "mid": v(71.84, -82.23) * mm, "end": v(72.21, -81.9) * mm});
            skArc(sketch, "E40.25.86.0", {"start": v(71.47, -82.55) * mm, "mid": v(71.34, -82.74) * mm, "end": v(71.34, -82.96) * mm});
            skArc(sketch, "E40.29.86.0", {"start": v(72.64, -81.84) * mm, "mid": v(72.41, -81.8) * mm, "end": v(72.21, -81.9) * mm});
            skLineSegment(sketch, "E40.3.87.0", {"start": v(76.24, -78.5) * mm, "end": v(77.48, -78.98) * mm});
            skPoint(sketch, "E40.6.87.0", {"position": v(77.84, -79.12) * mm});
            skPoint(sketch, "E40.7.87.0", {"position": v(74.91, -79.44) * mm});
            skPoint(sketch, "E40.8.87.0", {"position": v(76, -78.4) * mm});
            skPoint(sketch, "E40.9.87.0", {"position": v(75.55, -81.3) * mm});
            skLineSegment(sketch, "E40.10.87.0", {"start": v(75, -79.68) * mm, "end": v(75.42, -80.94) * mm});
            skArc(sketch, "E40.13.87.0", {"start": v(77.48, -78.98) * mm, "mid": v(77.82, -79) * mm, "end": v(78.12, -78.84) * mm});
            skLineSegment(sketch, "E40.14.87.0", {"start": v(75.46, -78.92) * mm, "end": v(76.7, -80.22) * mm, "construction": true});
            skArc(sketch, "E40.17.87.0", {"start": v(75.26, -81.57) * mm, "mid": v(75.43, -81.28) * mm, "end": v(75.42, -80.94) * mm});
            skArc(sketch, "E40.21.87.0", {"start": v(75.1, -79.26) * mm, "mid": v(75.46, -78.92) * mm, "end": v(75.81, -78.58) * mm});
            skArc(sketch, "E40.25.87.0", {"start": v(75.1, -79.26) * mm, "mid": v(74.99, -79.46) * mm, "end": v(75, -79.68) * mm});
            skArc(sketch, "E40.29.87.0", {"start": v(76.24, -78.5) * mm, "mid": v(76.01, -78.47) * mm, "end": v(75.81, -78.58) * mm});
            skLineSegment(sketch, "E40.3.88.0", {"start": v(79.68, -75) * mm, "end": v(80.94, -75.42) * mm});
            skPoint(sketch, "E40.6.88.0", {"position": v(81.3, -75.55) * mm});
            skPoint(sketch, "E40.7.88.0", {"position": v(78.4, -76) * mm});
            skPoint(sketch, "E40.8.88.0", {"position": v(79.44, -74.91) * mm});
            skPoint(sketch, "E40.9.88.0", {"position": v(79.12, -77.84) * mm});
            skLineSegment(sketch, "E40.10.88.0", {"start": v(78.5, -76.24) * mm, "end": v(78.98, -77.48) * mm});
            skArc(sketch, "E40.13.88.0", {"start": v(80.94, -75.42) * mm, "mid": v(81.28, -75.43) * mm, "end": v(81.57, -75.26) * mm});
            skLineSegment(sketch, "E40.14.88.0", {"start": v(78.92, -75.46) * mm, "end": v(80.22, -76.7) * mm, "construction": true});
            skArc(sketch, "E40.17.88.0", {"start": v(78.84, -78.12) * mm, "mid": v(79, -77.82) * mm, "end": v(78.98, -77.48) * mm});
            skArc(sketch, "E40.21.88.0", {"start": v(78.58, -75.81) * mm, "mid": v(78.92, -75.46) * mm, "end": v(79.26, -75.1) * mm});
            skArc(sketch, "E40.25.88.0", {"start": v(78.58, -75.81) * mm, "mid": v(78.47, -76.01) * mm, "end": v(78.5, -76.24) * mm});
            skArc(sketch, "E40.29.88.0", {"start": v(79.68, -75) * mm, "mid": v(79.46, -74.99) * mm, "end": v(79.26, -75.1) * mm});
            skLineSegment(sketch, "E40.3.89.0", {"start": v(82.96, -71.34) * mm, "end": v(84.24, -71.71) * mm});
            skPoint(sketch, "E40.6.89.0", {"position": v(84.62, -71.82) * mm});
            skPoint(sketch, "E40.7.89.0", {"position": v(81.73, -72.4) * mm});
            skPoint(sketch, "E40.8.89.0", {"position": v(82.72, -71.27) * mm});
            skPoint(sketch, "E40.9.89.0", {"position": v(82.53, -74.21) * mm});
            skLineSegment(sketch, "E40.10.89.0", {"start": v(81.84, -72.64) * mm, "end": v(82.37, -73.85) * mm});
            skArc(sketch, "E40.13.89.0", {"start": v(84.24, -71.71) * mm, "mid": v(84.58, -71.71) * mm, "end": v(84.87, -71.52) * mm});
            skLineSegment(sketch, "E40.14.89.0", {"start": v(82.23, -71.84) * mm, "end": v(83.58, -73.02) * mm, "construction": true});
            skArc(sketch, "E40.17.89.0", {"start": v(82.27, -74.5) * mm, "mid": v(82.42, -74.2) * mm, "end": v(82.37, -73.85) * mm});
            skArc(sketch, "E40.21.89.0", {"start": v(81.9, -72.21) * mm, "mid": v(82.23, -71.84) * mm, "end": v(82.55, -71.47) * mm});
            skArc(sketch, "E40.25.89.0", {"start": v(81.9, -72.21) * mm, "mid": v(81.8, -72.41) * mm, "end": v(81.84, -72.64) * mm});
            skArc(sketch, "E40.29.89.0", {"start": v(82.96, -71.34) * mm, "mid": v(82.74, -71.34) * mm, "end": v(82.55, -71.47) * mm});
            skLineSegment(sketch, "E40.3.90.0", {"start": v(86.08, -67.55) * mm, "end": v(87.38, -67.86) * mm});
            skPoint(sketch, "E40.6.90.0", {"position": v(87.75, -67.95) * mm});
            skPoint(sketch, "E40.7.90.0", {"position": v(84.9, -68.66) * mm});
            skPoint(sketch, "E40.8.90.0", {"position": v(85.83, -67.49) * mm});
            skPoint(sketch, "E40.9.90.0", {"position": v(85.78, -70.43) * mm});
            skLineSegment(sketch, "E40.10.90.0", {"start": v(85.01, -68.9) * mm, "end": v(85.6, -70.08) * mm});
            skArc(sketch, "E40.13.90.0", {"start": v(87.38, -67.86) * mm, "mid": v(87.72, -67.85) * mm, "end": v(88, -67.64) * mm});
            skLineSegment(sketch, "E40.14.90.0", {"start": v(85.37, -68.08) * mm, "end": v(86.77, -69.2) * mm, "construction": true});
            skArc(sketch, "E40.17.90.0", {"start": v(85.53, -70.73) * mm, "mid": v(85.66, -70.42) * mm, "end": v(85.6, -70.08) * mm});
            skArc(sketch, "E40.21.90.0", {"start": v(85.06, -68.46) * mm, "mid": v(85.37, -68.08) * mm, "end": v(85.67, -67.7) * mm});
            skArc(sketch, "E40.25.90.0", {"start": v(85.06, -68.46) * mm, "mid": v(84.97, -68.67) * mm, "end": v(85.01, -68.9) * mm});
            skArc(sketch, "E40.29.90.0", {"start": v(86.08, -67.55) * mm, "mid": v(85.86, -67.56) * mm, "end": v(85.67, -67.7) * mm});
            skLineSegment(sketch, "E40.3.91.0", {"start": v(89.03, -63.62) * mm, "end": v(90.33, -63.87) * mm});
            skPoint(sketch, "E40.6.91.0", {"position": v(90.71, -63.95) * mm});
            skPoint(sketch, "E40.7.91.0", {"position": v(87.9, -64.78) * mm});
            skPoint(sketch, "E40.8.91.0", {"position": v(88.77, -63.57) * mm});
            skPoint(sketch, "E40.9.91.0", {"position": v(88.85, -66.51) * mm});
            skLineSegment(sketch, "E40.10.91.0", {"start": v(88.02, -65) * mm, "end": v(88.66, -66.17) * mm});
            skArc(sketch, "E40.13.91.0", {"start": v(90.33, -63.87) * mm, "mid": v(90.67, -63.84) * mm, "end": v(90.94, -63.63) * mm});
            skLineSegment(sketch, "E40.14.91.0", {"start": v(88.34, -64.18) * mm, "end": v(89.8, -65.24) * mm, "construction": true});
            skArc(sketch, "E40.17.91.0", {"start": v(88.62, -66.83) * mm, "mid": v(88.74, -66.5) * mm, "end": v(88.66, -66.17) * mm});
            skArc(sketch, "E40.21.91.0", {"start": v(88.04, -64.58) * mm, "mid": v(88.34, -64.18) * mm, "end": v(88.62, -63.78) * mm});
            skArc(sketch, "E40.25.91.0", {"start": v(88.04, -64.58) * mm, "mid": v(87.97, -64.79) * mm, "end": v(88.02, -65) * mm});
            skArc(sketch, "E40.29.91.0", {"start": v(89.03, -63.62) * mm, "mid": v(88.8, -63.64) * mm, "end": v(88.62, -63.78) * mm});
            skLineSegment(sketch, "E40.3.92.0", {"start": v(91.8, -59.56) * mm, "end": v(93.1, -59.76) * mm});
            skPoint(sketch, "E40.6.92.0", {"position": v(93.5, -59.81) * mm});
            skPoint(sketch, "E40.7.92.0", {"position": v(90.71, -60.78) * mm});
            skPoint(sketch, "E40.8.92.0", {"position": v(91.54, -59.52) * mm});
            skPoint(sketch, "E40.9.92.0", {"position": v(91.75, -62.46) * mm});
            skLineSegment(sketch, "E40.10.92.0", {"start": v(90.84, -61) * mm, "end": v(91.54, -62.13) * mm});
            skArc(sketch, "E40.13.92.0", {"start": v(93.1, -59.76) * mm, "mid": v(93.44, -59.7) * mm, "end": v(93.7, -59.49) * mm});
            skLineSegment(sketch, "E40.14.92.0", {"start": v(91.13, -60.15) * mm, "end": v(92.63, -61.14) * mm, "construction": true});
            skArc(sketch, "E40.17.92.0", {"start": v(91.53, -62.78) * mm, "mid": v(91.63, -62.46) * mm, "end": v(91.54, -62.13) * mm});
            skArc(sketch, "E40.21.92.0", {"start": v(90.85, -60.56) * mm, "mid": v(91.13, -60.15) * mm, "end": v(91.4, -59.74) * mm});
            skArc(sketch, "E40.25.92.0", {"start": v(90.85, -60.56) * mm, "mid": v(90.79, -60.78) * mm, "end": v(90.84, -61) * mm});
            skArc(sketch, "E40.29.92.0", {"start": v(91.8, -59.56) * mm, "mid": v(91.57, -59.6) * mm, "end": v(91.4, -59.74) * mm});
            skLineSegment(sketch, "E40.3.93.0", {"start": v(94.37, -55.38) * mm, "end": v(95.7, -55.52) * mm});
            skPoint(sketch, "E40.6.93.0", {"position": v(96.08, -55.56) * mm});
            skPoint(sketch, "E40.7.93.0", {"position": v(93.35, -56.65) * mm});
            skPoint(sketch, "E40.8.93.0", {"position": v(94.12, -55.36) * mm});
            skPoint(sketch, "E40.9.93.0", {"position": v(94.46, -58.28) * mm});
            skLineSegment(sketch, "E40.10.93.0", {"start": v(93.49, -56.86) * mm, "end": v(94.24, -57.96) * mm});
            skArc(sketch, "E40.13.93.0", {"start": v(95.7, -55.52) * mm, "mid": v(96.03, -55.46) * mm, "end": v(96.28, -55.22) * mm});
            skLineSegment(sketch, "E40.14.93.0", {"start": v(93.73, -56) * mm, "end": v(95.28, -56.93) * mm, "construction": true});
            skArc(sketch, "E40.17.93.0", {"start": v(94.25, -58.61) * mm, "mid": v(94.34, -58.28) * mm, "end": v(94.24, -57.96) * mm});
            skArc(sketch, "E40.21.93.0", {"start": v(93.48, -56.43) * mm, "mid": v(93.73, -56) * mm, "end": v(93.99, -55.58) * mm});
            skArc(sketch, "E40.25.93.0", {"start": v(93.48, -56.43) * mm, "mid": v(93.42, -56.64) * mm, "end": v(93.49, -56.86) * mm});
            skArc(sketch, "E40.29.93.0", {"start": v(94.37, -55.38) * mm, "mid": v(94.15, -55.42) * mm, "end": v(93.99, -55.58) * mm});
            skLineSegment(sketch, "E40.3.94.0", {"start": v(96.76, -51.1) * mm, "end": v(98.09, -51.17) * mm});
            skPoint(sketch, "E40.6.94.0", {"position": v(98.48, -51.2) * mm});
            skPoint(sketch, "E40.7.94.0", {"position": v(95.8, -52.4) * mm});
            skPoint(sketch, "E40.8.94.0", {"position": v(96.5, -51.08) * mm});
            skPoint(sketch, "E40.9.94.0", {"position": v(96.97, -53.98) * mm});
            skLineSegment(sketch, "E40.10.94.0", {"start": v(95.95, -52.6) * mm, "end": v(96.74, -53.67) * mm});
            skArc(sketch, "E40.13.94.0", {"start": v(98.09, -51.17) * mm, "mid": v(98.42, -51.1) * mm, "end": v(98.66, -50.85) * mm});
            skLineSegment(sketch, "E40.14.94.0", {"start": v(96.15, -51.74) * mm, "end": v(97.74, -52.6) * mm, "construction": true});
            skArc(sketch, "E40.17.94.0", {"start": v(96.78, -54.33) * mm, "mid": v(96.86, -54) * mm, "end": v(96.74, -53.67) * mm});
            skArc(sketch, "E40.21.94.0", {"start": v(95.92, -52.18) * mm, "mid": v(96.15, -51.74) * mm, "end": v(96.38, -51.3) * mm});
            skArc(sketch, "E40.25.94.0", {"start": v(95.92, -52.18) * mm, "mid": v(95.87, -52.4) * mm, "end": v(95.95, -52.6) * mm});
            skArc(sketch, "E40.29.94.0", {"start": v(96.76, -51.1) * mm, "mid": v(96.54, -51.14) * mm, "end": v(96.38, -51.3) * mm});
            skLineSegment(sketch, "E40.3.95.0", {"start": v(98.95, -46.7) * mm, "end": v(100.29, -46.72) * mm});
            skPoint(sketch, "E40.6.95.0", {"position": v(100.67, -46.72) * mm});
            skPoint(sketch, "E40.7.95.0", {"position": v(98.05, -48.05) * mm});
            skPoint(sketch, "E40.8.95.0", {"position": v(98.7, -46.7) * mm});
            skPoint(sketch, "E40.9.95.0", {"position": v(99.3, -49.58) * mm});
            skLineSegment(sketch, "E40.10.95.0", {"start": v(98.21, -48.25) * mm, "end": v(99.05, -49.28) * mm});
            skArc(sketch, "E40.13.95.0", {"start": v(100.29, -46.72) * mm, "mid": v(100.61, -46.63) * mm, "end": v(100.84, -46.37) * mm});
            skLineSegment(sketch, "E40.14.95.0", {"start": v(98.38, -47.38) * mm, "end": v(100, -48.16) * mm, "construction": true});
            skArc(sketch, "E40.17.95.0", {"start": v(99.12, -49.93) * mm, "mid": v(99.18, -49.6) * mm, "end": v(99.05, -49.28) * mm});
            skArc(sketch, "E40.21.95.0", {"start": v(98.16, -47.82) * mm, "mid": v(98.38, -47.38) * mm, "end": v(98.59, -46.93) * mm});
            skArc(sketch, "E40.25.95.0", {"start": v(98.16, -47.82) * mm, "mid": v(98.12, -48.04) * mm, "end": v(98.21, -48.25) * mm});
            skArc(sketch, "E40.29.95.0", {"start": v(98.95, -46.7) * mm, "mid": v(98.74, -46.76) * mm, "end": v(98.59, -46.93) * mm});
            skLineSegment(sketch, "E40.3.96.0", {"start": v(100.95, -42.21) * mm, "end": v(102.28, -42.17) * mm});
            skPoint(sketch, "E40.6.96.0", {"position": v(102.67, -42.16) * mm});
            skPoint(sketch, "E40.7.96.0", {"position": v(100.1, -43.6) * mm});
            skPoint(sketch, "E40.8.96.0", {"position": v(100.7, -42.22) * mm});
            skPoint(sketch, "E40.9.96.0", {"position": v(101.42, -45.07) * mm});
            skLineSegment(sketch, "E40.10.96.0", {"start": v(100.28, -43.8) * mm, "end": v(101.16, -44.78) * mm});
            skArc(sketch, "E40.13.96.0", {"start": v(102.28, -42.17) * mm, "mid": v(102.6, -42.06) * mm, "end": v(102.82, -41.8) * mm});
            skLineSegment(sketch, "E40.14.96.0", {"start": v(100.4, -42.91) * mm, "end": v(102.06, -43.62) * mm, "construction": true});
            skArc(sketch, "E40.17.96.0", {"start": v(101.26, -45.43) * mm, "mid": v(101.3, -45.1) * mm, "end": v(101.16, -44.78) * mm});
            skArc(sketch, "E40.21.96.0", {"start": v(100.2, -43.37) * mm, "mid": v(100.4, -42.91) * mm, "end": v(100.6, -42.46) * mm});
            skArc(sketch, "E40.25.96.0", {"start": v(100.2, -43.37) * mm, "mid": v(100.18, -43.6) * mm, "end": v(100.28, -43.8) * mm});
            skArc(sketch, "E40.29.96.0", {"start": v(100.95, -42.21) * mm, "mid": v(100.74, -42.28) * mm, "end": v(100.6, -42.46) * mm});
            skLineSegment(sketch, "E40.3.97.0", {"start": v(102.74, -37.64) * mm, "end": v(104.07, -37.54) * mm});
            skPoint(sketch, "E40.6.97.0", {"position": v(104.46, -37.51) * mm});
            skPoint(sketch, "E40.7.97.0", {"position": v(101.96, -39.07) * mm});
            skPoint(sketch, "E40.8.97.0", {"position": v(102.49, -37.66) * mm});
            skPoint(sketch, "E40.9.97.0", {"position": v(103.34, -40.48) * mm});
            skLineSegment(sketch, "E40.10.97.0", {"start": v(102.14, -39.25) * mm, "end": v(103.07, -40.2) * mm});
            skArc(sketch, "E40.13.97.0", {"start": v(104.07, -37.54) * mm, "mid": v(104.39, -37.42) * mm, "end": v(104.59, -37.14) * mm});
            skLineSegment(sketch, "E40.14.97.0", {"start": v(102.23, -38.37) * mm, "end": v(103.91, -39) * mm, "construction": true});
            skArc(sketch, "E40.17.97.0", {"start": v(103.2, -40.84) * mm, "mid": v(103.23, -40.5) * mm, "end": v(103.07, -40.2) * mm});
            skArc(sketch, "E40.21.97.0", {"start": v(102.05, -38.83) * mm, "mid": v(102.23, -38.37) * mm, "end": v(102.4, -37.9) * mm});
            skArc(sketch, "E40.25.97.0", {"start": v(102.05, -38.83) * mm, "mid": v(102.03, -39.05) * mm, "end": v(102.14, -39.25) * mm});
            skArc(sketch, "E40.29.97.0", {"start": v(102.74, -37.64) * mm, "mid": v(102.53, -37.72) * mm, "end": v(102.4, -37.9) * mm});
            skLineSegment(sketch, "E40.3.98.0", {"start": v(104.33, -33) * mm, "end": v(105.65, -32.83) * mm});
            skPoint(sketch, "E40.6.98.0", {"position": v(106.04, -32.79) * mm});
            skPoint(sketch, "E40.7.98.0", {"position": v(103.61, -34.45) * mm});
            skPoint(sketch, "E40.8.98.0", {"position": v(104.07, -33.03) * mm});
            skPoint(sketch, "E40.9.98.0", {"position": v(105.06, -35.8) * mm});
            skLineSegment(sketch, "E40.10.98.0", {"start": v(103.8, -34.63) * mm, "end": v(104.77, -35.54) * mm});
            skArc(sketch, "E40.13.98.0", {"start": v(105.65, -32.83) * mm, "mid": v(105.96, -32.7) * mm, "end": v(106.15, -32.41) * mm});
            skLineSegment(sketch, "E40.14.98.0", {"start": v(103.84, -33.74) * mm, "end": v(105.56, -34.3) * mm, "construction": true});
            skArc(sketch, "E40.17.98.0", {"start": v(104.93, -36.17) * mm, "mid": v(104.94, -35.83) * mm, "end": v(104.77, -35.54) * mm});
            skArc(sketch, "E40.21.98.0", {"start": v(103.7, -34.21) * mm, "mid": v(103.84, -33.74) * mm, "end": v(104, -33.27) * mm});
            skArc(sketch, "E40.25.98.0", {"start": v(103.7, -34.21) * mm, "mid": v(103.68, -34.44) * mm, "end": v(103.8, -34.63) * mm});
            skArc(sketch, "E40.29.98.0", {"start": v(104.33, -33) * mm, "mid": v(104.12, -33.08) * mm, "end": v(104, -33.27) * mm});
            skLineSegment(sketch, "E40.3.99.0", {"start": v(105.7, -28.28) * mm, "end": v(107.02, -28.06) * mm});
            skPoint(sketch, "E40.6.99.0", {"position": v(107.4, -28) * mm});
            skPoint(sketch, "E40.7.99.0", {"position": v(105.05, -29.77) * mm});
            skPoint(sketch, "E40.8.99.0", {"position": v(105.45, -28.32) * mm});
            skPoint(sketch, "E40.9.99.0", {"position": v(106.56, -31.05) * mm});
            skLineSegment(sketch, "E40.10.99.0", {"start": v(105.25, -29.94) * mm, "end": v(106.26, -30.8) * mm});
            skArc(sketch, "E40.13.99.0", {"start": v(107.02, -28.06) * mm, "mid": v(107.32, -27.91) * mm, "end": v(107.5, -27.62) * mm});
            skLineSegment(sketch, "E40.14.99.0", {"start": v(105.25, -29.05) * mm, "end": v(106.99, -29.53) * mm, "construction": true});
            skArc(sketch, "E40.17.99.0", {"start": v(106.45, -31.43) * mm, "mid": v(106.45, -31.09) * mm, "end": v(106.26, -30.8) * mm});
            skArc(sketch, "E40.21.99.0", {"start": v(105.12, -29.52) * mm, "mid": v(105.25, -29.05) * mm, "end": v(105.38, -28.57) * mm});
            skArc(sketch, "E40.25.99.0", {"start": v(105.12, -29.52) * mm, "mid": v(105.12, -29.75) * mm, "end": v(105.25, -29.94) * mm});
            skArc(sketch, "E40.29.99.0", {"start": v(105.7, -28.28) * mm, "mid": v(105.5, -28.38) * mm, "end": v(105.38, -28.57) * mm});
            skLineSegment(sketch, "E41.3.100.0", {"start": v(106.87, -23.51) * mm, "end": v(108.17, -23.23) * mm});
            skPoint(sketch, "E41.6.100.0", {"position": v(108.55, -23.15) * mm});
            skPoint(sketch, "E41.7.100.0", {"position": v(106.28, -25.03) * mm});
            skPoint(sketch, "E41.8.100.0", {"position": v(106.62, -23.56) * mm});
            skPoint(sketch, "E41.9.100.0", {"position": v(107.84, -26.24) * mm});
            skLineSegment(sketch, "E41.10.100.0", {"start": v(106.48, -25.18) * mm, "end": v(107.53, -26) * mm});
            skArc(sketch, "E41.13.100.0", {"start": v(108.17, -23.23) * mm, "mid": v(108.47, -23.07) * mm, "end": v(108.63, -22.77) * mm});
            skLineSegment(sketch, "E41.14.100.0", {"start": v(106.45, -24.3) * mm, "end": v(108.2, -24.7) * mm, "construction": true});
            skArc(sketch, "E41.17.100.0", {"start": v(107.75, -26.62) * mm, "mid": v(107.73, -26.28) * mm, "end": v(107.53, -26) * mm});
            skArc(sketch, "E41.21.100.0", {"start": v(106.34, -24.78) * mm, "mid": v(106.45, -24.3) * mm, "end": v(106.56, -23.81) * mm});
            skArc(sketch, "E41.25.100.0", {"start": v(106.34, -24.78) * mm, "mid": v(106.35, -25) * mm, "end": v(106.48, -25.18) * mm});
            skArc(sketch, "E41.29.100.0", {"start": v(106.87, -23.51) * mm, "mid": v(106.67, -23.62) * mm, "end": v(106.56, -23.81) * mm});
            skLineSegment(sketch, "E41.3.101.0", {"start": v(107.81, -18.7) * mm, "end": v(109.1, -18.35) * mm});
            skPoint(sketch, "E41.6.101.0", {"position": v(109.48, -18.26) * mm});
            skPoint(sketch, "E41.7.101.0", {"position": v(107.3, -20.23) * mm});
            skPoint(sketch, "E41.8.101.0", {"position": v(107.57, -18.76) * mm});
            skPoint(sketch, "E41.9.101.0", {"position": v(108.91, -21.38) * mm});
            skLineSegment(sketch, "E41.10.101.0", {"start": v(107.5, -20.38) * mm, "end": v(108.6, -21.15) * mm});
            skArc(sketch, "E41.13.101.0", {"start": v(109.1, -18.35) * mm, "mid": v(109.4, -18.18) * mm, "end": v(109.54, -17.87) * mm});
            skLineSegment(sketch, "E41.14.101.0", {"start": v(107.43, -19.5) * mm, "end": v(109.2, -19.82) * mm, "construction": true});
            skArc(sketch, "E41.17.101.0", {"start": v(108.83, -21.76) * mm, "mid": v(108.8, -21.42) * mm, "end": v(108.6, -21.15) * mm});
            skArc(sketch, "E41.21.101.0", {"start": v(107.34, -19.98) * mm, "mid": v(107.43, -19.5) * mm, "end": v(107.52, -19.01) * mm});
            skArc(sketch, "E41.25.101.0", {"start": v(107.34, -19.98) * mm, "mid": v(107.37, -20.2) * mm, "end": v(107.5, -20.38) * mm});
            skArc(sketch, "E41.29.101.0", {"start": v(107.81, -18.7) * mm, "mid": v(107.62, -18.8) * mm, "end": v(107.52, -19.01) * mm});
            skLineSegment(sketch, "E41.3.102.0", {"start": v(108.54, -13.84) * mm, "end": v(109.81, -13.44) * mm});
            skPoint(sketch, "E41.6.102.0", {"position": v(110.19, -13.33) * mm});
            skPoint(sketch, "E41.7.102.0", {"position": v(108.1, -15.4) * mm});
            skPoint(sketch, "E41.8.102.0", {"position": v(108.3, -13.91) * mm});
            skPoint(sketch, "E41.9.102.0", {"position": v(109.76, -16.47) * mm});
            skLineSegment(sketch, "E41.10.102.0", {"start": v(108.31, -15.54) * mm, "end": v(109.43, -16.26) * mm});
            skArc(sketch, "E41.13.102.0", {"start": v(109.81, -13.44) * mm, "mid": v(110.1, -13.25) * mm, "end": v(110.23, -12.94) * mm});
            skLineSegment(sketch, "E41.14.102.0", {"start": v(108.2, -14.66) * mm, "end": v(109.98, -14.9) * mm, "construction": true});
            skArc(sketch, "E41.17.102.0", {"start": v(109.7, -16.85) * mm, "mid": v(109.66, -16.52) * mm, "end": v(109.43, -16.26) * mm});
            skArc(sketch, "E41.21.102.0", {"start": v(108.13, -15.15) * mm, "mid": v(108.2, -14.66) * mm, "end": v(108.27, -14.17) * mm});
            skArc(sketch, "E41.25.102.0", {"start": v(108.13, -15.15) * mm, "mid": v(108.17, -15.37) * mm, "end": v(108.31, -15.54) * mm});
            skArc(sketch, "E41.29.102.0", {"start": v(108.54, -13.84) * mm, "mid": v(108.36, -13.96) * mm, "end": v(108.27, -14.17) * mm});
            skLineSegment(sketch, "E41.3.103.0", {"start": v(109.05, -8.95) * mm, "end": v(110.3, -8.5) * mm});
            skPoint(sketch, "E41.6.103.0", {"position": v(110.67, -8.37) * mm});
            skPoint(sketch, "E41.7.103.0", {"position": v(108.68, -10.53) * mm});
            skPoint(sketch, "E41.8.103.0", {"position": v(108.81, -9.04) * mm});
            skPoint(sketch, "E41.9.103.0", {"position": v(110.39, -11.53) * mm});
            skLineSegment(sketch, "E41.10.103.0", {"start": v(108.9, -10.66) * mm, "end": v(110.05, -11.33) * mm});
            skArc(sketch, "E41.13.103.0", {"start": v(110.3, -8.5) * mm, "mid": v(110.58, -8.3) * mm, "end": v(110.7, -7.98) * mm});
            skLineSegment(sketch, "E41.14.103.0", {"start": v(108.75, -9.79) * mm, "end": v(110.54, -9.95) * mm, "construction": true});
            skArc(sketch, "E41.17.103.0", {"start": v(110.35, -11.91) * mm, "mid": v(110.29, -11.58) * mm, "end": v(110.05, -11.33) * mm});
            skArc(sketch, "E41.21.103.0", {"start": v(108.7, -10.28) * mm, "mid": v(108.75, -9.79) * mm, "end": v(108.8, -9.3) * mm});
            skArc(sketch, "E41.25.103.0", {"start": v(108.7, -10.28) * mm, "mid": v(108.75, -10.5) * mm, "end": v(108.9, -10.66) * mm});
            skArc(sketch, "E41.29.103.0", {"start": v(109.05, -8.95) * mm, "mid": v(108.87, -9.09) * mm, "end": v(108.8, -9.3) * mm});
            skLineSegment(sketch, "E41.3.104.0", {"start": v(109.35, -4.05) * mm, "end": v(110.58, -3.54) * mm});
            skPoint(sketch, "E41.6.104.0", {"position": v(110.94, -3.4) * mm});
            skPoint(sketch, "E41.7.104.0", {"position": v(109.04, -5.65) * mm});
            skPoint(sketch, "E41.8.104.0", {"position": v(109.1, -4.15) * mm});
            skPoint(sketch, "E41.9.104.0", {"position": v(110.8, -6.56) * mm});
            skLineSegment(sketch, "E41.10.104.0", {"start": v(109.27, -5.77) * mm, "end": v(110.45, -6.38) * mm});
            skArc(sketch, "E41.13.104.0", {"start": v(110.58, -3.54) * mm, "mid": v(110.84, -3.33) * mm, "end": v(110.95, -3) * mm});
            skLineSegment(sketch, "E41.14.104.0", {"start": v(109.08, -4.9) * mm, "end": v(110.88, -4.98) * mm, "construction": true});
            skArc(sketch, "E41.17.104.0", {"start": v(110.77, -6.95) * mm, "mid": v(110.7, -6.62) * mm, "end": v(110.45, -6.38) * mm});
            skArc(sketch, "E41.21.104.0", {"start": v(109.06, -5.4) * mm, "mid": v(109.08, -4.9) * mm, "end": v(109.1, -4.4) * mm});
            skArc(sketch, "E41.25.104.0", {"start": v(109.06, -5.4) * mm, "mid": v(109.1, -5.61) * mm, "end": v(109.27, -5.77) * mm});
            skArc(sketch, "E41.29.104.0", {"start": v(109.35, -4.05) * mm, "mid": v(109.17, -4.2) * mm, "end": v(109.1, -4.4) * mm});
            skLineSegment(sketch, "E41.3.105.0", {"start": v(109.42, 0.86) * mm, "end": v(110.62, 1.42) * mm});
            skPoint(sketch, "E41.6.105.0", {"position": v(110.98, 1.59) * mm});
            skPoint(sketch, "E41.7.105.0", {"position": v(109.19, -0.75) * mm});
            skPoint(sketch, "E41.8.105.0", {"position": v(109.19, 0.75) * mm});
            skPoint(sketch, "E41.9.105.0", {"position": v(110.98, -1.59) * mm});
            skLineSegment(sketch, "E41.10.105.0", {"start": v(109.42, -0.86) * mm, "end": v(110.62, -1.42) * mm});
            skArc(sketch, "E41.13.105.0", {"start": v(110.62, 1.42) * mm, "mid": v(110.88, 1.65) * mm, "end": v(110.97, 1.98) * mm});
            skLineSegment(sketch, "E41.14.105.0", {"start": v(109.19, 0) * mm, "end": v(110.99, 0) * mm, "construction": true});
            skArc(sketch, "E41.17.105.0", {"start": v(110.97, -1.98) * mm, "mid": v(110.88, -1.65) * mm, "end": v(110.62, -1.42) * mm});
            skArc(sketch, "E41.21.105.0", {"start": v(109.19, -0.5) * mm, "mid": v(109.19, 0) * mm, "end": v(109.19, 0.5) * mm});
            skArc(sketch, "E41.25.105.0", {"start": v(109.19, -0.5) * mm, "mid": v(109.25, -0.71) * mm, "end": v(109.42, -0.86) * mm});
            skArc(sketch, "E41.29.105.0", {"start": v(109.42, 0.86) * mm, "mid": v(109.25, 0.71) * mm, "end": v(109.19, 0.5) * mm});
            skLineSegment(sketch, "E41.3.106.0", {"start": v(109.27, 5.77) * mm, "end": v(110.45, 6.38) * mm});
            skPoint(sketch, "E41.6.106.0", {"position": v(110.8, 6.56) * mm});
            skPoint(sketch, "E41.7.106.0", {"position": v(109.1, 4.15) * mm});
            skPoint(sketch, "E41.8.106.0", {"position": v(109.04, 5.65) * mm});
            skPoint(sketch, "E41.9.106.0", {"position": v(110.94, 3.4) * mm});
            skLineSegment(sketch, "E41.10.106.0", {"start": v(109.35, 4.05) * mm, "end": v(110.58, 3.54) * mm});
            skArc(sketch, "E41.13.106.0", {"start": v(110.45, 6.38) * mm, "mid": v(110.7, 6.62) * mm, "end": v(110.77, 6.95) * mm});
            skLineSegment(sketch, "E41.14.106.0", {"start": v(109.08, 4.9) * mm, "end": v(110.88, 4.98) * mm, "construction": true});
            skArc(sketch, "E41.17.106.0", {"start": v(110.95, 3) * mm, "mid": v(110.84, 3.33) * mm, "end": v(110.58, 3.54) * mm});
            skArc(sketch, "E41.21.106.0", {"start": v(109.1, 4.4) * mm, "mid": v(109.08, 4.9) * mm, "end": v(109.06, 5.4) * mm});
            skArc(sketch, "E41.25.106.0", {"start": v(109.1, 4.4) * mm, "mid": v(109.17, 4.2) * mm, "end": v(109.35, 4.05) * mm});
            skArc(sketch, "E41.29.106.0", {"start": v(109.27, 5.77) * mm, "mid": v(109.1, 5.61) * mm, "end": v(109.06, 5.4) * mm});
            skLineSegment(sketch, "E41.3.107.0", {"start": v(108.9, 10.66) * mm, "end": v(110.05, 11.33) * mm});
            skPoint(sketch, "E41.6.107.0", {"position": v(110.39, 11.53) * mm});
            skPoint(sketch, "E41.7.107.0", {"position": v(108.81, 9.04) * mm});
            skPoint(sketch, "E41.8.107.0", {"position": v(108.68, 10.53) * mm});
            skPoint(sketch, "E41.9.107.0", {"position": v(110.67, 8.37) * mm});
            skLineSegment(sketch, "E41.10.107.0", {"start": v(109.05, 8.95) * mm, "end": v(110.3, 8.5) * mm});
            skArc(sketch, "E41.13.107.0", {"start": v(110.05, 11.33) * mm, "mid": v(110.29, 11.58) * mm, "end": v(110.35, 11.91) * mm});
            skLineSegment(sketch, "E41.14.107.0", {"start": v(108.75, 9.79) * mm, "end": v(110.54, 9.95) * mm, "construction": true});
            skArc(sketch, "E41.17.107.0", {"start": v(110.7, 7.98) * mm, "mid": v(110.58, 8.3) * mm, "end": v(110.3, 8.5) * mm});
            skArc(sketch, "E41.21.107.0", {"start": v(108.8, 9.3) * mm, "mid": v(108.75, 9.79) * mm, "end": v(108.7, 10.28) * mm});
            skArc(sketch, "E41.25.107.0", {"start": v(108.8, 9.3) * mm, "mid": v(108.87, 9.09) * mm, "end": v(109.05, 8.95) * mm});
            skArc(sketch, "E41.29.107.0", {"start": v(108.9, 10.66) * mm, "mid": v(108.75, 10.5) * mm, "end": v(108.7, 10.28) * mm});
            skLineSegment(sketch, "E41.3.108.0", {"start": v(108.31, 15.54) * mm, "end": v(109.43, 16.26) * mm});
            skPoint(sketch, "E41.6.108.0", {"position": v(109.76, 16.47) * mm});
            skPoint(sketch, "E41.7.108.0", {"position": v(108.3, 13.91) * mm});
            skPoint(sketch, "E41.8.108.0", {"position": v(108.1, 15.4) * mm});
            skPoint(sketch, "E41.9.108.0", {"position": v(110.19, 13.33) * mm});
            skLineSegment(sketch, "E41.10.108.0", {"start": v(108.54, 13.84) * mm, "end": v(109.81, 13.44) * mm});
            skArc(sketch, "E41.13.108.0", {"start": v(109.43, 16.26) * mm, "mid": v(109.66, 16.52) * mm, "end": v(109.7, 16.85) * mm});
            skLineSegment(sketch, "E41.14.108.0", {"start": v(108.2, 14.66) * mm, "end": v(109.98, 14.9) * mm, "construction": true});
            skArc(sketch, "E41.17.108.0", {"start": v(110.23, 12.94) * mm, "mid": v(110.1, 13.25) * mm, "end": v(109.81, 13.44) * mm});
            skArc(sketch, "E41.21.108.0", {"start": v(108.27, 14.17) * mm, "mid": v(108.2, 14.66) * mm, "end": v(108.13, 15.15) * mm});
            skArc(sketch, "E41.25.108.0", {"start": v(108.27, 14.17) * mm, "mid": v(108.36, 13.96) * mm, "end": v(108.54, 13.84) * mm});
            skArc(sketch, "E41.29.108.0", {"start": v(108.31, 15.54) * mm, "mid": v(108.17, 15.37) * mm, "end": v(108.13, 15.15) * mm});
            skLineSegment(sketch, "E41.3.109.0", {"start": v(107.5, 20.38) * mm, "end": v(108.6, 21.15) * mm});
            skPoint(sketch, "E41.6.109.0", {"position": v(108.91, 21.38) * mm});
            skPoint(sketch, "E41.7.109.0", {"position": v(107.57, 18.76) * mm});
            skPoint(sketch, "E41.8.109.0", {"position": v(107.3, 20.23) * mm});
            skPoint(sketch, "E41.9.109.0", {"position": v(109.48, 18.26) * mm});
            skLineSegment(sketch, "E41.10.109.0", {"start": v(107.81, 18.7) * mm, "end": v(109.1, 18.35) * mm});
            skArc(sketch, "E41.13.109.0", {"start": v(108.6, 21.15) * mm, "mid": v(108.8, 21.42) * mm, "end": v(108.83, 21.76) * mm});
            skLineSegment(sketch, "E41.14.109.0", {"start": v(107.43, 19.5) * mm, "end": v(109.2, 19.82) * mm, "construction": true});
            skArc(sketch, "E41.17.109.0", {"start": v(109.54, 17.87) * mm, "mid": v(109.4, 18.18) * mm, "end": v(109.1, 18.35) * mm});
            skArc(sketch, "E41.21.109.0", {"start": v(107.52, 19.01) * mm, "mid": v(107.43, 19.5) * mm, "end": v(107.34, 19.98) * mm});
            skArc(sketch, "E41.25.109.0", {"start": v(107.52, 19.01) * mm, "mid": v(107.62, 18.8) * mm, "end": v(107.81, 18.7) * mm});
            skArc(sketch, "E41.29.109.0", {"start": v(107.5, 20.38) * mm, "mid": v(107.37, 20.2) * mm, "end": v(107.34, 19.98) * mm});
            skLineSegment(sketch, "E41.3.110.0", {"start": v(106.48, 25.18) * mm, "end": v(107.53, 26) * mm});
            skPoint(sketch, "E41.6.110.0", {"position": v(107.84, 26.24) * mm});
            skPoint(sketch, "E41.7.110.0", {"position": v(106.62, 23.56) * mm});
            skPoint(sketch, "E41.8.110.0", {"position": v(106.28, 25.03) * mm});
            skPoint(sketch, "E41.9.110.0", {"position": v(108.55, 23.15) * mm});
            skLineSegment(sketch, "E41.10.110.0", {"start": v(106.87, 23.51) * mm, "end": v(108.17, 23.23) * mm});
            skArc(sketch, "E41.13.110.0", {"start": v(107.53, 26) * mm, "mid": v(107.73, 26.28) * mm, "end": v(107.75, 26.62) * mm});
            skLineSegment(sketch, "E41.14.110.0", {"start": v(106.45, 24.3) * mm, "end": v(108.2, 24.7) * mm, "construction": true});
            skArc(sketch, "E41.17.110.0", {"start": v(108.63, 22.77) * mm, "mid": v(108.47, 23.07) * mm, "end": v(108.17, 23.23) * mm});
            skArc(sketch, "E41.21.110.0", {"start": v(106.56, 23.81) * mm, "mid": v(106.45, 24.3) * mm, "end": v(106.34, 24.78) * mm});
            skArc(sketch, "E41.25.110.0", {"start": v(106.56, 23.81) * mm, "mid": v(106.67, 23.62) * mm, "end": v(106.87, 23.51) * mm});
            skArc(sketch, "E41.29.110.0", {"start": v(106.48, 25.18) * mm, "mid": v(106.35, 25) * mm, "end": v(106.34, 24.78) * mm});
            skLineSegment(sketch, "E41.3.111.0", {"start": v(105.25, 29.94) * mm, "end": v(106.26, 30.8) * mm});
            skPoint(sketch, "E41.6.111.0", {"position": v(106.56, 31.05) * mm});
            skPoint(sketch, "E41.7.111.0", {"position": v(105.45, 28.32) * mm});
            skPoint(sketch, "E41.8.111.0", {"position": v(105.05, 29.77) * mm});
            skPoint(sketch, "E41.9.111.0", {"position": v(107.4, 28) * mm});
            skLineSegment(sketch, "E41.10.111.0", {"start": v(105.7, 28.28) * mm, "end": v(107.02, 28.06) * mm});
            skArc(sketch, "E41.13.111.0", {"start": v(106.26, 30.8) * mm, "mid": v(106.45, 31.09) * mm, "end": v(106.45, 31.43) * mm});
            skLineSegment(sketch, "E41.14.111.0", {"start": v(105.25, 29.05) * mm, "end": v(106.99, 29.53) * mm, "construction": true});
            skArc(sketch, "E41.17.111.0", {"start": v(107.5, 27.62) * mm, "mid": v(107.32, 27.91) * mm, "end": v(107.02, 28.06) * mm});
            skArc(sketch, "E41.21.111.0", {"start": v(105.38, 28.57) * mm, "mid": v(105.25, 29.05) * mm, "end": v(105.12, 29.52) * mm});
            skArc(sketch, "E41.25.111.0", {"start": v(105.38, 28.57) * mm, "mid": v(105.5, 28.38) * mm, "end": v(105.7, 28.28) * mm});
            skArc(sketch, "E41.29.111.0", {"start": v(105.25, 29.94) * mm, "mid": v(105.12, 29.75) * mm, "end": v(105.12, 29.52) * mm});
            skLineSegment(sketch, "E41.3.112.0", {"start": v(103.8, 34.63) * mm, "end": v(104.77, 35.54) * mm});
            skPoint(sketch, "E41.6.112.0", {"position": v(105.06, 35.8) * mm});
            skPoint(sketch, "E41.7.112.0", {"position": v(104.07, 33.03) * mm});
            skPoint(sketch, "E41.8.112.0", {"position": v(103.61, 34.45) * mm});
            skPoint(sketch, "E41.9.112.0", {"position": v(106.04, 32.79) * mm});
            skLineSegment(sketch, "E41.10.112.0", {"start": v(104.33, 33) * mm, "end": v(105.65, 32.83) * mm});
            skArc(sketch, "E41.13.112.0", {"start": v(104.77, 35.54) * mm, "mid": v(104.94, 35.83) * mm, "end": v(104.93, 36.17) * mm});
            skLineSegment(sketch, "E41.14.112.0", {"start": v(103.84, 33.74) * mm, "end": v(105.56, 34.3) * mm, "construction": true});
            skArc(sketch, "E41.17.112.0", {"start": v(106.15, 32.41) * mm, "mid": v(105.96, 32.7) * mm, "end": v(105.65, 32.83) * mm});
            skArc(sketch, "E41.21.112.0", {"start": v(104, 33.27) * mm, "mid": v(103.84, 33.74) * mm, "end": v(103.7, 34.21) * mm});
            skArc(sketch, "E41.25.112.0", {"start": v(104, 33.27) * mm, "mid": v(104.12, 33.08) * mm, "end": v(104.33, 33) * mm});
            skArc(sketch, "E41.29.112.0", {"start": v(103.8, 34.63) * mm, "mid": v(103.68, 34.44) * mm, "end": v(103.7, 34.21) * mm});
            skLineSegment(sketch, "E41.3.113.0", {"start": v(102.14, 39.25) * mm, "end": v(103.07, 40.2) * mm});
            skPoint(sketch, "E41.6.113.0", {"position": v(103.34, 40.48) * mm});
            skPoint(sketch, "E41.7.113.0", {"position": v(102.49, 37.66) * mm});
            skPoint(sketch, "E41.8.113.0", {"position": v(101.96, 39.07) * mm});
            skPoint(sketch, "E41.9.113.0", {"position": v(104.46, 37.51) * mm});
            skLineSegment(sketch, "E41.10.113.0", {"start": v(102.74, 37.64) * mm, "end": v(104.07, 37.54) * mm});
            skArc(sketch, "E41.13.113.0", {"start": v(103.07, 40.2) * mm, "mid": v(103.23, 40.5) * mm, "end": v(103.2, 40.84) * mm});
            skLineSegment(sketch, "E41.14.113.0", {"start": v(102.23, 38.37) * mm, "end": v(103.91, 39) * mm, "construction": true});
            skArc(sketch, "E41.17.113.0", {"start": v(104.59, 37.14) * mm, "mid": v(104.39, 37.42) * mm, "end": v(104.07, 37.54) * mm});
            skArc(sketch, "E41.21.113.0", {"start": v(102.4, 37.9) * mm, "mid": v(102.23, 38.37) * mm, "end": v(102.05, 38.83) * mm});
            skArc(sketch, "E41.25.113.0", {"start": v(102.4, 37.9) * mm, "mid": v(102.53, 37.72) * mm, "end": v(102.74, 37.64) * mm});
            skArc(sketch, "E41.29.113.0", {"start": v(102.14, 39.25) * mm, "mid": v(102.03, 39.05) * mm, "end": v(102.05, 38.83) * mm});
            skLineSegment(sketch, "E41.3.114.0", {"start": v(100.28, 43.8) * mm, "end": v(101.16, 44.78) * mm});
            skPoint(sketch, "E41.6.114.0", {"position": v(101.42, 45.07) * mm});
            skPoint(sketch, "E41.7.114.0", {"position": v(100.7, 42.22) * mm});
            skPoint(sketch, "E41.8.114.0", {"position": v(100.1, 43.6) * mm});
            skPoint(sketch, "E41.9.114.0", {"position": v(102.67, 42.16) * mm});
            skLineSegment(sketch, "E41.10.114.0", {"start": v(100.95, 42.21) * mm, "end": v(102.28, 42.17) * mm});
            skArc(sketch, "E41.13.114.0", {"start": v(101.16, 44.78) * mm, "mid": v(101.3, 45.1) * mm, "end": v(101.26, 45.43) * mm});
            skLineSegment(sketch, "E41.14.114.0", {"start": v(100.4, 42.91) * mm, "end": v(102.06, 43.62) * mm, "construction": true});
            skArc(sketch, "E41.17.114.0", {"start": v(102.82, 41.8) * mm, "mid": v(102.6, 42.06) * mm, "end": v(102.28, 42.17) * mm});
            skArc(sketch, "E41.21.114.0", {"start": v(100.6, 42.46) * mm, "mid": v(100.4, 42.91) * mm, "end": v(100.2, 43.37) * mm});
            skArc(sketch, "E41.25.114.0", {"start": v(100.6, 42.46) * mm, "mid": v(100.74, 42.28) * mm, "end": v(100.95, 42.21) * mm});
            skArc(sketch, "E41.29.114.0", {"start": v(100.28, 43.8) * mm, "mid": v(100.18, 43.6) * mm, "end": v(100.2, 43.37) * mm});
            skLineSegment(sketch, "E41.3.115.0", {"start": v(98.21, 48.25) * mm, "end": v(99.05, 49.28) * mm});
            skPoint(sketch, "E41.6.115.0", {"position": v(99.3, 49.58) * mm});
            skPoint(sketch, "E41.7.115.0", {"position": v(98.7, 46.7) * mm});
            skPoint(sketch, "E41.8.115.0", {"position": v(98.05, 48.05) * mm});
            skPoint(sketch, "E41.9.115.0", {"position": v(100.67, 46.72) * mm});
            skLineSegment(sketch, "E41.10.115.0", {"start": v(98.95, 46.7) * mm, "end": v(100.29, 46.72) * mm});
            skArc(sketch, "E41.13.115.0", {"start": v(99.05, 49.28) * mm, "mid": v(99.18, 49.6) * mm, "end": v(99.12, 49.93) * mm});
            skLineSegment(sketch, "E41.14.115.0", {"start": v(98.38, 47.38) * mm, "end": v(100, 48.16) * mm, "construction": true});
            skArc(sketch, "E41.17.115.0", {"start": v(100.84, 46.37) * mm, "mid": v(100.61, 46.63) * mm, "end": v(100.29, 46.72) * mm});
            skArc(sketch, "E41.21.115.0", {"start": v(98.59, 46.93) * mm, "mid": v(98.38, 47.38) * mm, "end": v(98.16, 47.82) * mm});
            skArc(sketch, "E41.25.115.0", {"start": v(98.59, 46.93) * mm, "mid": v(98.74, 46.76) * mm, "end": v(98.95, 46.7) * mm});
            skArc(sketch, "E41.29.115.0", {"start": v(98.21, 48.25) * mm, "mid": v(98.12, 48.04) * mm, "end": v(98.16, 47.82) * mm});
            skLineSegment(sketch, "E41.3.116.0", {"start": v(95.95, 52.6) * mm, "end": v(96.74, 53.67) * mm});
            skPoint(sketch, "E41.6.116.0", {"position": v(96.97, 53.98) * mm});
            skPoint(sketch, "E41.7.116.0", {"position": v(96.5, 51.08) * mm});
            skPoint(sketch, "E41.8.116.0", {"position": v(95.8, 52.4) * mm});
            skPoint(sketch, "E41.9.116.0", {"position": v(98.48, 51.2) * mm});
            skLineSegment(sketch, "E41.10.116.0", {"start": v(96.76, 51.1) * mm, "end": v(98.09, 51.17) * mm});
            skArc(sketch, "E41.13.116.0", {"start": v(96.74, 53.67) * mm, "mid": v(96.86, 54) * mm, "end": v(96.78, 54.33) * mm});
            skLineSegment(sketch, "E41.14.116.0", {"start": v(96.15, 51.74) * mm, "end": v(97.74, 52.6) * mm, "construction": true});
            skArc(sketch, "E41.17.116.0", {"start": v(98.66, 50.85) * mm, "mid": v(98.42, 51.1) * mm, "end": v(98.09, 51.17) * mm});
            skArc(sketch, "E41.21.116.0", {"start": v(96.38, 51.3) * mm, "mid": v(96.15, 51.74) * mm, "end": v(95.92, 52.18) * mm});
            skArc(sketch, "E41.25.116.0", {"start": v(96.38, 51.3) * mm, "mid": v(96.54, 51.14) * mm, "end": v(96.76, 51.1) * mm});
            skArc(sketch, "E41.29.116.0", {"start": v(95.95, 52.6) * mm, "mid": v(95.87, 52.4) * mm, "end": v(95.92, 52.18) * mm});
            skLineSegment(sketch, "E41.3.117.0", {"start": v(93.49, 56.86) * mm, "end": v(94.24, 57.96) * mm});
            skPoint(sketch, "E41.6.117.0", {"position": v(94.46, 58.28) * mm});
            skPoint(sketch, "E41.7.117.0", {"position": v(94.12, 55.36) * mm});
            skPoint(sketch, "E41.8.117.0", {"position": v(93.35, 56.65) * mm});
            skPoint(sketch, "E41.9.117.0", {"position": v(96.08, 55.56) * mm});
            skLineSegment(sketch, "E41.10.117.0", {"start": v(94.37, 55.38) * mm, "end": v(95.7, 55.52) * mm});
            skArc(sketch, "E41.13.117.0", {"start": v(94.24, 57.96) * mm, "mid": v(94.34, 58.28) * mm, "end": v(94.25, 58.61) * mm});
            skLineSegment(sketch, "E41.14.117.0", {"start": v(93.73, 56) * mm, "end": v(95.28, 56.93) * mm, "construction": true});
            skArc(sketch, "E41.17.117.0", {"start": v(96.28, 55.22) * mm, "mid": v(96.03, 55.46) * mm, "end": v(95.7, 55.52) * mm});
            skArc(sketch, "E41.21.117.0", {"start": v(93.99, 55.58) * mm, "mid": v(93.73, 56) * mm, "end": v(93.48, 56.43) * mm});
            skArc(sketch, "E41.25.117.0", {"start": v(93.99, 55.58) * mm, "mid": v(94.15, 55.42) * mm, "end": v(94.37, 55.38) * mm});
            skArc(sketch, "E41.29.117.0", {"start": v(93.49, 56.86) * mm, "mid": v(93.42, 56.64) * mm, "end": v(93.48, 56.43) * mm});
            skLineSegment(sketch, "E41.3.118.0", {"start": v(90.84, 61) * mm, "end": v(91.54, 62.13) * mm});
            skPoint(sketch, "E41.6.118.0", {"position": v(91.75, 62.46) * mm});
            skPoint(sketch, "E41.7.118.0", {"position": v(91.54, 59.52) * mm});
            skPoint(sketch, "E41.8.118.0", {"position": v(90.71, 60.78) * mm});
            skPoint(sketch, "E41.9.118.0", {"position": v(93.5, 59.81) * mm});
            skLineSegment(sketch, "E41.10.118.0", {"start": v(91.8, 59.56) * mm, "end": v(93.1, 59.76) * mm});
            skArc(sketch, "E41.13.118.0", {"start": v(91.54, 62.13) * mm, "mid": v(91.63, 62.46) * mm, "end": v(91.53, 62.78) * mm});
            skLineSegment(sketch, "E41.14.118.0", {"start": v(91.13, 60.15) * mm, "end": v(92.63, 61.14) * mm, "construction": true});
            skArc(sketch, "E41.17.118.0", {"start": v(93.7, 59.49) * mm, "mid": v(93.44, 59.7) * mm, "end": v(93.1, 59.76) * mm});
            skArc(sketch, "E41.21.118.0", {"start": v(91.4, 59.74) * mm, "mid": v(91.13, 60.15) * mm, "end": v(90.85, 60.56) * mm});
            skArc(sketch, "E41.25.118.0", {"start": v(91.4, 59.74) * mm, "mid": v(91.57, 59.6) * mm, "end": v(91.8, 59.56) * mm});
            skArc(sketch, "E41.29.118.0", {"start": v(90.84, 61) * mm, "mid": v(90.79, 60.78) * mm, "end": v(90.85, 60.56) * mm});
            skLineSegment(sketch, "E41.3.119.0", {"start": v(88.02, 65) * mm, "end": v(88.66, 66.17) * mm});
            skPoint(sketch, "E41.6.119.0", {"position": v(88.85, 66.51) * mm});
            skPoint(sketch, "E41.7.119.0", {"position": v(88.77, 63.57) * mm});
            skPoint(sketch, "E41.8.119.0", {"position": v(87.9, 64.78) * mm});
            skPoint(sketch, "E41.9.119.0", {"position": v(90.71, 63.95) * mm});
            skLineSegment(sketch, "E41.10.119.0", {"start": v(89.03, 63.62) * mm, "end": v(90.33, 63.87) * mm});
            skArc(sketch, "E41.13.119.0", {"start": v(88.66, 66.17) * mm, "mid": v(88.74, 66.5) * mm, "end": v(88.62, 66.83) * mm});
            skLineSegment(sketch, "E41.14.119.0", {"start": v(88.34, 64.18) * mm, "end": v(89.8, 65.24) * mm, "construction": true});
            skArc(sketch, "E41.17.119.0", {"start": v(90.94, 63.63) * mm, "mid": v(90.67, 63.84) * mm, "end": v(90.33, 63.87) * mm});
            skArc(sketch, "E41.21.119.0", {"start": v(88.62, 63.78) * mm, "mid": v(88.34, 64.18) * mm, "end": v(88.04, 64.58) * mm});
            skArc(sketch, "E41.25.119.0", {"start": v(88.62, 63.78) * mm, "mid": v(88.8, 63.64) * mm, "end": v(89.03, 63.62) * mm});
            skArc(sketch, "E41.29.119.0", {"start": v(88.02, 65) * mm, "mid": v(87.97, 64.79) * mm, "end": v(88.04, 64.58) * mm});
            skLineSegment(sketch, "E41.3.120.0", {"start": v(85.01, 68.9) * mm, "end": v(85.6, 70.08) * mm});
            skPoint(sketch, "E41.6.120.0", {"position": v(85.78, 70.43) * mm});
            skPoint(sketch, "E41.7.120.0", {"position": v(85.83, 67.49) * mm});
            skPoint(sketch, "E41.8.120.0", {"position": v(84.9, 68.66) * mm});
            skPoint(sketch, "E41.9.120.0", {"position": v(87.75, 67.95) * mm});
            skLineSegment(sketch, "E41.10.120.0", {"start": v(86.08, 67.55) * mm, "end": v(87.38, 67.86) * mm});
            skArc(sketch, "E41.13.120.0", {"start": v(85.6, 70.08) * mm, "mid": v(85.66, 70.42) * mm, "end": v(85.53, 70.73) * mm});
            skLineSegment(sketch, "E41.14.120.0", {"start": v(85.37, 68.08) * mm, "end": v(86.77, 69.2) * mm, "construction": true});
            skArc(sketch, "E41.17.120.0", {"start": v(88, 67.64) * mm, "mid": v(87.72, 67.85) * mm, "end": v(87.38, 67.86) * mm});
            skArc(sketch, "E41.21.120.0", {"start": v(85.67, 67.7) * mm, "mid": v(85.37, 68.08) * mm, "end": v(85.06, 68.46) * mm});
            skArc(sketch, "E41.25.120.0", {"start": v(85.67, 67.7) * mm, "mid": v(85.86, 67.56) * mm, "end": v(86.08, 67.55) * mm});
            skArc(sketch, "E41.29.120.0", {"start": v(85.01, 68.9) * mm, "mid": v(84.97, 68.67) * mm, "end": v(85.06, 68.46) * mm});
            skLineSegment(sketch, "E41.3.121.0", {"start": v(81.84, 72.64) * mm, "end": v(82.37, 73.85) * mm});
            skPoint(sketch, "E41.6.121.0", {"position": v(82.53, 74.21) * mm});
            skPoint(sketch, "E41.7.121.0", {"position": v(82.72, 71.27) * mm});
            skPoint(sketch, "E41.8.121.0", {"position": v(81.73, 72.4) * mm});
            skPoint(sketch, "E41.9.121.0", {"position": v(84.62, 71.82) * mm});
            skLineSegment(sketch, "E41.10.121.0", {"start": v(82.96, 71.34) * mm, "end": v(84.24, 71.71) * mm});
            skArc(sketch, "E41.13.121.0", {"start": v(82.37, 73.85) * mm, "mid": v(82.42, 74.2) * mm, "end": v(82.27, 74.5) * mm});
            skLineSegment(sketch, "E41.14.121.0", {"start": v(82.23, 71.84) * mm, "end": v(83.58, 73.02) * mm, "construction": true});
            skArc(sketch, "E41.17.121.0", {"start": v(84.87, 71.52) * mm, "mid": v(84.58, 71.71) * mm, "end": v(84.24, 71.71) * mm});
            skArc(sketch, "E41.21.121.0", {"start": v(82.55, 71.47) * mm, "mid": v(82.23, 71.84) * mm, "end": v(81.9, 72.21) * mm});
            skArc(sketch, "E41.25.121.0", {"start": v(82.55, 71.47) * mm, "mid": v(82.74, 71.34) * mm, "end": v(82.96, 71.34) * mm});
            skArc(sketch, "E41.29.121.0", {"start": v(81.84, 72.64) * mm, "mid": v(81.8, 72.41) * mm, "end": v(81.9, 72.21) * mm});
            skLineSegment(sketch, "E41.3.122.0", {"start": v(78.5, 76.24) * mm, "end": v(78.98, 77.48) * mm});
            skPoint(sketch, "E41.6.122.0", {"position": v(79.12, 77.84) * mm});
            skPoint(sketch, "E41.7.122.0", {"position": v(79.44, 74.91) * mm});
            skPoint(sketch, "E41.8.122.0", {"position": v(78.4, 76) * mm});
            skPoint(sketch, "E41.9.122.0", {"position": v(81.3, 75.55) * mm});
            skLineSegment(sketch, "E41.10.122.0", {"start": v(79.68, 75) * mm, "end": v(80.94, 75.42) * mm});
            skArc(sketch, "E41.13.122.0", {"start": v(78.98, 77.48) * mm, "mid": v(79, 77.82) * mm, "end": v(78.84, 78.12) * mm});
            skLineSegment(sketch, "E41.14.122.0", {"start": v(78.92, 75.46) * mm, "end": v(80.22, 76.7) * mm, "construction": true});
            skArc(sketch, "E41.17.122.0", {"start": v(81.57, 75.26) * mm, "mid": v(81.28, 75.43) * mm, "end": v(80.94, 75.42) * mm});
            skArc(sketch, "E41.21.122.0", {"start": v(79.26, 75.1) * mm, "mid": v(78.92, 75.46) * mm, "end": v(78.58, 75.81) * mm});
            skArc(sketch, "E41.25.122.0", {"start": v(79.26, 75.1) * mm, "mid": v(79.46, 74.99) * mm, "end": v(79.68, 75) * mm});
            skArc(sketch, "E41.29.122.0", {"start": v(78.5, 76.24) * mm, "mid": v(78.47, 76.01) * mm, "end": v(78.58, 75.81) * mm});
            skLineSegment(sketch, "E41.3.123.0", {"start": v(75, 79.68) * mm, "end": v(75.42, 80.94) * mm});
            skPoint(sketch, "E41.6.123.0", {"position": v(75.55, 81.3) * mm});
            skPoint(sketch, "E41.7.123.0", {"position": v(76, 78.4) * mm});
            skPoint(sketch, "E41.8.123.0", {"position": v(74.91, 79.44) * mm});
            skPoint(sketch, "E41.9.123.0", {"position": v(77.84, 79.12) * mm});
            skLineSegment(sketch, "E41.10.123.0", {"start": v(76.24, 78.5) * mm, "end": v(77.48, 78.98) * mm});
            skArc(sketch, "E41.13.123.0", {"start": v(75.42, 80.94) * mm, "mid": v(75.43, 81.28) * mm, "end": v(75.26, 81.57) * mm});
            skLineSegment(sketch, "E41.14.123.0", {"start": v(75.46, 78.92) * mm, "end": v(76.7, 80.22) * mm, "construction": true});
            skArc(sketch, "E41.17.123.0", {"start": v(78.12, 78.84) * mm, "mid": v(77.82, 79) * mm, "end": v(77.48, 78.98) * mm});
            skArc(sketch, "E41.21.123.0", {"start": v(75.81, 78.58) * mm, "mid": v(75.46, 78.92) * mm, "end": v(75.1, 79.26) * mm});
            skArc(sketch, "E41.25.123.0", {"start": v(75.81, 78.58) * mm, "mid": v(76.01, 78.47) * mm, "end": v(76.24, 78.5) * mm});
            skArc(sketch, "E41.29.123.0", {"start": v(75, 79.68) * mm, "mid": v(74.99, 79.46) * mm, "end": v(75.1, 79.26) * mm});
            skLineSegment(sketch, "E41.3.124.0", {"start": v(71.34, 82.96) * mm, "end": v(71.71, 84.24) * mm});
            skPoint(sketch, "E41.6.124.0", {"position": v(71.82, 84.62) * mm});
            skPoint(sketch, "E41.7.124.0", {"position": v(72.4, 81.73) * mm});
            skPoint(sketch, "E41.8.124.0", {"position": v(71.27, 82.72) * mm});
            skPoint(sketch, "E41.9.124.0", {"position": v(74.21, 82.53) * mm});
            skLineSegment(sketch, "E41.10.124.0", {"start": v(72.64, 81.84) * mm, "end": v(73.85, 82.37) * mm});
            skArc(sketch, "E41.13.124.0", {"start": v(71.71, 84.24) * mm, "mid": v(71.71, 84.58) * mm, "end": v(71.52, 84.87) * mm});
            skLineSegment(sketch, "E41.14.124.0", {"start": v(71.84, 82.23) * mm, "end": v(73.02, 83.58) * mm, "construction": true});
            skArc(sketch, "E41.17.124.0", {"start": v(74.5, 82.27) * mm, "mid": v(74.2, 82.42) * mm, "end": v(73.85, 82.37) * mm});
            skArc(sketch, "E41.21.124.0", {"start": v(72.21, 81.9) * mm, "mid": v(71.84, 82.23) * mm, "end": v(71.47, 82.55) * mm});
            skArc(sketch, "E41.25.124.0", {"start": v(72.21, 81.9) * mm, "mid": v(72.41, 81.8) * mm, "end": v(72.64, 81.84) * mm});
            skArc(sketch, "E41.29.124.0", {"start": v(71.34, 82.96) * mm, "mid": v(71.34, 82.74) * mm, "end": v(71.47, 82.55) * mm});
            skLineSegment(sketch, "E41.3.125.0", {"start": v(67.55, 86.08) * mm, "end": v(67.86, 87.38) * mm});
            skPoint(sketch, "E41.6.125.0", {"position": v(67.95, 87.75) * mm});
            skPoint(sketch, "E41.7.125.0", {"position": v(68.66, 84.9) * mm});
            skPoint(sketch, "E41.8.125.0", {"position": v(67.49, 85.83) * mm});
            skPoint(sketch, "E41.9.125.0", {"position": v(70.43, 85.78) * mm});
            skLineSegment(sketch, "E41.10.125.0", {"start": v(68.9, 85.01) * mm, "end": v(70.08, 85.6) * mm});
            skArc(sketch, "E41.13.125.0", {"start": v(67.86, 87.38) * mm, "mid": v(67.85, 87.72) * mm, "end": v(67.64, 88) * mm});
            skLineSegment(sketch, "E41.14.125.0", {"start": v(68.08, 85.37) * mm, "end": v(69.2, 86.77) * mm, "construction": true});
            skArc(sketch, "E41.17.125.0", {"start": v(70.73, 85.53) * mm, "mid": v(70.42, 85.66) * mm, "end": v(70.08, 85.6) * mm});
            skArc(sketch, "E41.21.125.0", {"start": v(68.46, 85.06) * mm, "mid": v(68.08, 85.37) * mm, "end": v(67.7, 85.67) * mm});
            skArc(sketch, "E41.25.125.0", {"start": v(68.46, 85.06) * mm, "mid": v(68.67, 84.97) * mm, "end": v(68.9, 85.01) * mm});
            skArc(sketch, "E41.29.125.0", {"start": v(67.55, 86.08) * mm, "mid": v(67.56, 85.86) * mm, "end": v(67.7, 85.67) * mm});
            skLineSegment(sketch, "E41.3.126.0", {"start": v(63.62, 89.03) * mm, "end": v(63.87, 90.33) * mm});
            skPoint(sketch, "E41.6.126.0", {"position": v(63.95, 90.71) * mm});
            skPoint(sketch, "E41.7.126.0", {"position": v(64.78, 87.9) * mm});
            skPoint(sketch, "E41.8.126.0", {"position": v(63.57, 88.77) * mm});
            skPoint(sketch, "E41.9.126.0", {"position": v(66.51, 88.85) * mm});
            skLineSegment(sketch, "E41.10.126.0", {"start": v(65, 88.02) * mm, "end": v(66.17, 88.66) * mm});
            skArc(sketch, "E41.13.126.0", {"start": v(63.87, 90.33) * mm, "mid": v(63.84, 90.67) * mm, "end": v(63.63, 90.94) * mm});
            skLineSegment(sketch, "E41.14.126.0", {"start": v(64.18, 88.34) * mm, "end": v(65.24, 89.8) * mm, "construction": true});
            skArc(sketch, "E41.17.126.0", {"start": v(66.83, 88.62) * mm, "mid": v(66.5, 88.74) * mm, "end": v(66.17, 88.66) * mm});
            skArc(sketch, "E41.21.126.0", {"start": v(64.58, 88.04) * mm, "mid": v(64.18, 88.34) * mm, "end": v(63.78, 88.62) * mm});
            skArc(sketch, "E41.25.126.0", {"start": v(64.58, 88.04) * mm, "mid": v(64.79, 87.97) * mm, "end": v(65, 88.02) * mm});
            skArc(sketch, "E41.29.126.0", {"start": v(63.62, 89.03) * mm, "mid": v(63.64, 88.8) * mm, "end": v(63.78, 88.62) * mm});
            skLineSegment(sketch, "E41.3.127.0", {"start": v(59.56, 91.8) * mm, "end": v(59.76, 93.1) * mm});
            skPoint(sketch, "E41.6.127.0", {"position": v(59.81, 93.5) * mm});
            skPoint(sketch, "E41.7.127.0", {"position": v(60.78, 90.71) * mm});
            skPoint(sketch, "E41.8.127.0", {"position": v(59.52, 91.54) * mm});
            skPoint(sketch, "E41.9.127.0", {"position": v(62.46, 91.75) * mm});
            skLineSegment(sketch, "E41.10.127.0", {"start": v(61, 90.84) * mm, "end": v(62.13, 91.54) * mm});
            skArc(sketch, "E41.13.127.0", {"start": v(59.76, 93.1) * mm, "mid": v(59.7, 93.44) * mm, "end": v(59.49, 93.7) * mm});
            skLineSegment(sketch, "E41.14.127.0", {"start": v(60.15, 91.13) * mm, "end": v(61.14, 92.63) * mm, "construction": true});
            skArc(sketch, "E41.17.127.0", {"start": v(62.78, 91.53) * mm, "mid": v(62.46, 91.63) * mm, "end": v(62.13, 91.54) * mm});
            skArc(sketch, "E41.21.127.0", {"start": v(60.56, 90.85) * mm, "mid": v(60.15, 91.13) * mm, "end": v(59.74, 91.4) * mm});
            skArc(sketch, "E41.25.127.0", {"start": v(60.56, 90.85) * mm, "mid": v(60.78, 90.79) * mm, "end": v(61, 90.84) * mm});
            skArc(sketch, "E41.29.127.0", {"start": v(59.56, 91.8) * mm, "mid": v(59.6, 91.57) * mm, "end": v(59.74, 91.4) * mm});
            skLineSegment(sketch, "E41.3.128.0", {"start": v(55.38, 94.37) * mm, "end": v(55.52, 95.7) * mm});
            skPoint(sketch, "E41.6.128.0", {"position": v(55.56, 96.08) * mm});
            skPoint(sketch, "E41.7.128.0", {"position": v(56.65, 93.35) * mm});
            skPoint(sketch, "E41.8.128.0", {"position": v(55.36, 94.12) * mm});
            skPoint(sketch, "E41.9.128.0", {"position": v(58.28, 94.46) * mm});
            skLineSegment(sketch, "E41.10.128.0", {"start": v(56.86, 93.49) * mm, "end": v(57.96, 94.24) * mm});
            skArc(sketch, "E41.13.128.0", {"start": v(55.52, 95.7) * mm, "mid": v(55.46, 96.03) * mm, "end": v(55.22, 96.28) * mm});
            skLineSegment(sketch, "E41.14.128.0", {"start": v(56, 93.73) * mm, "end": v(56.93, 95.28) * mm, "construction": true});
            skArc(sketch, "E41.17.128.0", {"start": v(58.61, 94.25) * mm, "mid": v(58.28, 94.34) * mm, "end": v(57.96, 94.24) * mm});
            skArc(sketch, "E41.21.128.0", {"start": v(56.43, 93.48) * mm, "mid": v(56, 93.73) * mm, "end": v(55.58, 93.99) * mm});
            skArc(sketch, "E41.25.128.0", {"start": v(56.43, 93.48) * mm, "mid": v(56.64, 93.42) * mm, "end": v(56.86, 93.49) * mm});
            skArc(sketch, "E41.29.128.0", {"start": v(55.38, 94.37) * mm, "mid": v(55.42, 94.15) * mm, "end": v(55.58, 93.99) * mm});
            skLineSegment(sketch, "E41.3.129.0", {"start": v(51.1, 96.76) * mm, "end": v(51.17, 98.09) * mm});
            skPoint(sketch, "E41.6.129.0", {"position": v(51.2, 98.48) * mm});
            skPoint(sketch, "E41.7.129.0", {"position": v(52.4, 95.8) * mm});
            skPoint(sketch, "E41.8.129.0", {"position": v(51.08, 96.5) * mm});
            skPoint(sketch, "E41.9.129.0", {"position": v(53.98, 96.97) * mm});
            skLineSegment(sketch, "E41.10.129.0", {"start": v(52.6, 95.95) * mm, "end": v(53.67, 96.74) * mm});
            skArc(sketch, "E41.13.129.0", {"start": v(51.17, 98.09) * mm, "mid": v(51.1, 98.42) * mm, "end": v(50.85, 98.66) * mm});
            skLineSegment(sketch, "E41.14.129.0", {"start": v(51.74, 96.15) * mm, "end": v(52.6, 97.74) * mm, "construction": true});
            skArc(sketch, "E41.17.129.0", {"start": v(54.33, 96.78) * mm, "mid": v(54, 96.86) * mm, "end": v(53.67, 96.74) * mm});
            skArc(sketch, "E41.21.129.0", {"start": v(52.18, 95.92) * mm, "mid": v(51.74, 96.15) * mm, "end": v(51.3, 96.38) * mm});
            skArc(sketch, "E41.25.129.0", {"start": v(52.18, 95.92) * mm, "mid": v(52.4, 95.87) * mm, "end": v(52.6, 95.95) * mm});
            skArc(sketch, "E41.29.129.0", {"start": v(51.1, 96.76) * mm, "mid": v(51.14, 96.54) * mm, "end": v(51.3, 96.38) * mm});
            skLineSegment(sketch, "E41.3.130.0", {"start": v(46.7, 98.95) * mm, "end": v(46.72, 100.29) * mm});
            skPoint(sketch, "E41.6.130.0", {"position": v(46.72, 100.67) * mm});
            skPoint(sketch, "E41.7.130.0", {"position": v(48.05, 98.05) * mm});
            skPoint(sketch, "E41.8.130.0", {"position": v(46.7, 98.7) * mm});
            skPoint(sketch, "E41.9.130.0", {"position": v(49.58, 99.3) * mm});
            skLineSegment(sketch, "E41.10.130.0", {"start": v(48.25, 98.21) * mm, "end": v(49.28, 99.05) * mm});
            skArc(sketch, "E41.13.130.0", {"start": v(46.72, 100.29) * mm, "mid": v(46.63, 100.61) * mm, "end": v(46.37, 100.84) * mm});
            skLineSegment(sketch, "E41.14.130.0", {"start": v(47.38, 98.38) * mm, "end": v(48.16, 100) * mm, "construction": true});
            skArc(sketch, "E41.17.130.0", {"start": v(49.93, 99.12) * mm, "mid": v(49.6, 99.18) * mm, "end": v(49.28, 99.05) * mm});
            skArc(sketch, "E41.21.130.0", {"start": v(47.82, 98.16) * mm, "mid": v(47.38, 98.38) * mm, "end": v(46.93, 98.59) * mm});
            skArc(sketch, "E41.25.130.0", {"start": v(47.82, 98.16) * mm, "mid": v(48.04, 98.12) * mm, "end": v(48.25, 98.21) * mm});
            skArc(sketch, "E41.29.130.0", {"start": v(46.7, 98.95) * mm, "mid": v(46.76, 98.74) * mm, "end": v(46.93, 98.59) * mm});
            skLineSegment(sketch, "E41.3.131.0", {"start": v(42.21, 100.95) * mm, "end": v(42.17, 102.28) * mm});
            skPoint(sketch, "E41.6.131.0", {"position": v(42.16, 102.67) * mm});
            skPoint(sketch, "E41.7.131.0", {"position": v(43.6, 100.1) * mm});
            skPoint(sketch, "E41.8.131.0", {"position": v(42.22, 100.7) * mm});
            skPoint(sketch, "E41.9.131.0", {"position": v(45.07, 101.42) * mm});
            skLineSegment(sketch, "E41.10.131.0", {"start": v(43.8, 100.28) * mm, "end": v(44.78, 101.16) * mm});
            skArc(sketch, "E41.13.131.0", {"start": v(42.17, 102.28) * mm, "mid": v(42.06, 102.6) * mm, "end": v(41.8, 102.82) * mm});
            skLineSegment(sketch, "E41.14.131.0", {"start": v(42.91, 100.4) * mm, "end": v(43.62, 102.06) * mm, "construction": true});
            skArc(sketch, "E41.17.131.0", {"start": v(45.43, 101.26) * mm, "mid": v(45.1, 101.3) * mm, "end": v(44.78, 101.16) * mm});
            skArc(sketch, "E41.21.131.0", {"start": v(43.37, 100.2) * mm, "mid": v(42.91, 100.4) * mm, "end": v(42.46, 100.6) * mm});
            skArc(sketch, "E41.25.131.0", {"start": v(43.37, 100.2) * mm, "mid": v(43.6, 100.18) * mm, "end": v(43.8, 100.28) * mm});
            skArc(sketch, "E41.29.131.0", {"start": v(42.21, 100.95) * mm, "mid": v(42.28, 100.74) * mm, "end": v(42.46, 100.6) * mm});
            skLineSegment(sketch, "E41.3.132.0", {"start": v(37.64, 102.74) * mm, "end": v(37.54, 104.07) * mm});
            skPoint(sketch, "E41.6.132.0", {"position": v(37.51, 104.46) * mm});
            skPoint(sketch, "E41.7.132.0", {"position": v(39.07, 101.96) * mm});
            skPoint(sketch, "E41.8.132.0", {"position": v(37.66, 102.49) * mm});
            skPoint(sketch, "E41.9.132.0", {"position": v(40.48, 103.34) * mm});
            skLineSegment(sketch, "E41.10.132.0", {"start": v(39.25, 102.14) * mm, "end": v(40.2, 103.07) * mm});
            skArc(sketch, "E41.13.132.0", {"start": v(37.54, 104.07) * mm, "mid": v(37.42, 104.39) * mm, "end": v(37.14, 104.59) * mm});
            skLineSegment(sketch, "E41.14.132.0", {"start": v(38.37, 102.23) * mm, "end": v(39, 103.91) * mm, "construction": true});
            skArc(sketch, "E41.17.132.0", {"start": v(40.84, 103.2) * mm, "mid": v(40.5, 103.23) * mm, "end": v(40.2, 103.07) * mm});
            skArc(sketch, "E41.21.132.0", {"start": v(38.83, 102.05) * mm, "mid": v(38.37, 102.23) * mm, "end": v(37.9, 102.4) * mm});
            skArc(sketch, "E41.25.132.0", {"start": v(38.83, 102.05) * mm, "mid": v(39.05, 102.03) * mm, "end": v(39.25, 102.14) * mm});
            skArc(sketch, "E41.29.132.0", {"start": v(37.64, 102.74) * mm, "mid": v(37.72, 102.53) * mm, "end": v(37.9, 102.4) * mm});
            skLineSegment(sketch, "E41.3.133.0", {"start": v(33, 104.33) * mm, "end": v(32.83, 105.65) * mm});
            skPoint(sketch, "E41.6.133.0", {"position": v(32.79, 106.04) * mm});
            skPoint(sketch, "E41.7.133.0", {"position": v(34.45, 103.61) * mm});
            skPoint(sketch, "E41.8.133.0", {"position": v(33.03, 104.07) * mm});
            skPoint(sketch, "E41.9.133.0", {"position": v(35.8, 105.06) * mm});
            skLineSegment(sketch, "E41.10.133.0", {"start": v(34.63, 103.8) * mm, "end": v(35.54, 104.77) * mm});
            skArc(sketch, "E41.13.133.0", {"start": v(32.83, 105.65) * mm, "mid": v(32.7, 105.96) * mm, "end": v(32.41, 106.15) * mm});
            skLineSegment(sketch, "E41.14.133.0", {"start": v(33.74, 103.84) * mm, "end": v(34.3, 105.56) * mm, "construction": true});
            skArc(sketch, "E41.17.133.0", {"start": v(36.17, 104.93) * mm, "mid": v(35.83, 104.94) * mm, "end": v(35.54, 104.77) * mm});
            skArc(sketch, "E41.21.133.0", {"start": v(34.21, 103.7) * mm, "mid": v(33.74, 103.84) * mm, "end": v(33.27, 104) * mm});
            skArc(sketch, "E41.25.133.0", {"start": v(34.21, 103.7) * mm, "mid": v(34.44, 103.68) * mm, "end": v(34.63, 103.8) * mm});
            skArc(sketch, "E41.29.133.0", {"start": v(33, 104.33) * mm, "mid": v(33.08, 104.12) * mm, "end": v(33.27, 104) * mm});
            skLineSegment(sketch, "E41.3.134.0", {"start": v(28.28, 105.7) * mm, "end": v(28.06, 107.02) * mm});
            skPoint(sketch, "E41.6.134.0", {"position": v(28, 107.4) * mm});
            skPoint(sketch, "E41.7.134.0", {"position": v(29.77, 105.05) * mm});
            skPoint(sketch, "E41.8.134.0", {"position": v(28.32, 105.45) * mm});
            skPoint(sketch, "E41.9.134.0", {"position": v(31.05, 106.56) * mm});
            skLineSegment(sketch, "E41.10.134.0", {"start": v(29.94, 105.25) * mm, "end": v(30.8, 106.26) * mm});
            skArc(sketch, "E41.13.134.0", {"start": v(28.06, 107.02) * mm, "mid": v(27.91, 107.32) * mm, "end": v(27.62, 107.5) * mm});
            skLineSegment(sketch, "E41.14.134.0", {"start": v(29.05, 105.25) * mm, "end": v(29.53, 106.99) * mm, "construction": true});
            skArc(sketch, "E41.17.134.0", {"start": v(31.43, 106.45) * mm, "mid": v(31.09, 106.45) * mm, "end": v(30.8, 106.26) * mm});
            skArc(sketch, "E41.21.134.0", {"start": v(29.52, 105.12) * mm, "mid": v(29.05, 105.25) * mm, "end": v(28.57, 105.38) * mm});
            skArc(sketch, "E41.25.134.0", {"start": v(29.52, 105.12) * mm, "mid": v(29.75, 105.12) * mm, "end": v(29.94, 105.25) * mm});
            skArc(sketch, "E41.29.134.0", {"start": v(28.28, 105.7) * mm, "mid": v(28.38, 105.5) * mm, "end": v(28.57, 105.38) * mm});
            skLineSegment(sketch, "E41.3.135.0", {"start": v(23.51, 106.87) * mm, "end": v(23.23, 108.17) * mm});
            skPoint(sketch, "E41.6.135.0", {"position": v(23.15, 108.55) * mm});
            skPoint(sketch, "E41.7.135.0", {"position": v(25.03, 106.28) * mm});
            skPoint(sketch, "E41.8.135.0", {"position": v(23.56, 106.62) * mm});
            skPoint(sketch, "E41.9.135.0", {"position": v(26.24, 107.84) * mm});
            skLineSegment(sketch, "E41.10.135.0", {"start": v(25.18, 106.48) * mm, "end": v(26, 107.53) * mm});
            skArc(sketch, "E41.13.135.0", {"start": v(23.23, 108.17) * mm, "mid": v(23.07, 108.47) * mm, "end": v(22.77, 108.63) * mm});
            skLineSegment(sketch, "E41.14.135.0", {"start": v(24.3, 106.45) * mm, "end": v(24.7, 108.2) * mm, "construction": true});
            skArc(sketch, "E41.17.135.0", {"start": v(26.62, 107.75) * mm, "mid": v(26.28, 107.73) * mm, "end": v(26, 107.53) * mm});
            skArc(sketch, "E41.21.135.0", {"start": v(24.78, 106.34) * mm, "mid": v(24.3, 106.45) * mm, "end": v(23.81, 106.56) * mm});
            skArc(sketch, "E41.25.135.0", {"start": v(24.78, 106.34) * mm, "mid": v(25, 106.35) * mm, "end": v(25.18, 106.48) * mm});
            skArc(sketch, "E41.29.135.0", {"start": v(23.51, 106.87) * mm, "mid": v(23.62, 106.67) * mm, "end": v(23.81, 106.56) * mm});
            skLineSegment(sketch, "E41.3.136.0", {"start": v(18.7, 107.81) * mm, "end": v(18.35, 109.1) * mm});
            skPoint(sketch, "E41.6.136.0", {"position": v(18.26, 109.48) * mm});
            skPoint(sketch, "E41.7.136.0", {"position": v(20.23, 107.3) * mm});
            skPoint(sketch, "E41.8.136.0", {"position": v(18.76, 107.57) * mm});
            skPoint(sketch, "E41.9.136.0", {"position": v(21.38, 108.91) * mm});
            skLineSegment(sketch, "E41.10.136.0", {"start": v(20.38, 107.5) * mm, "end": v(21.15, 108.6) * mm});
            skArc(sketch, "E41.13.136.0", {"start": v(18.35, 109.1) * mm, "mid": v(18.18, 109.4) * mm, "end": v(17.87, 109.54) * mm});
            skLineSegment(sketch, "E41.14.136.0", {"start": v(19.5, 107.43) * mm, "end": v(19.82, 109.2) * mm, "construction": true});
            skArc(sketch, "E41.17.136.0", {"start": v(21.76, 108.83) * mm, "mid": v(21.42, 108.8) * mm, "end": v(21.15, 108.6) * mm});
            skArc(sketch, "E41.21.136.0", {"start": v(19.98, 107.34) * mm, "mid": v(19.5, 107.43) * mm, "end": v(19.01, 107.52) * mm});
            skArc(sketch, "E41.25.136.0", {"start": v(19.98, 107.34) * mm, "mid": v(20.2, 107.37) * mm, "end": v(20.38, 107.5) * mm});
            skArc(sketch, "E41.29.136.0", {"start": v(18.7, 107.81) * mm, "mid": v(18.8, 107.62) * mm, "end": v(19.01, 107.52) * mm});
            skLineSegment(sketch, "E41.3.137.0", {"start": v(13.84, 108.54) * mm, "end": v(13.44, 109.81) * mm});
            skPoint(sketch, "E41.6.137.0", {"position": v(13.33, 110.19) * mm});
            skPoint(sketch, "E41.7.137.0", {"position": v(15.4, 108.1) * mm});
            skPoint(sketch, "E41.8.137.0", {"position": v(13.91, 108.3) * mm});
            skPoint(sketch, "E41.9.137.0", {"position": v(16.47, 109.76) * mm});
            skLineSegment(sketch, "E41.10.137.0", {"start": v(15.54, 108.31) * mm, "end": v(16.26, 109.43) * mm});
            skArc(sketch, "E41.13.137.0", {"start": v(13.44, 109.81) * mm, "mid": v(13.25, 110.1) * mm, "end": v(12.94, 110.23) * mm});
            skLineSegment(sketch, "E41.14.137.0", {"start": v(14.66, 108.2) * mm, "end": v(14.9, 109.98) * mm, "construction": true});
            skArc(sketch, "E41.17.137.0", {"start": v(16.85, 109.7) * mm, "mid": v(16.52, 109.66) * mm, "end": v(16.26, 109.43) * mm});
            skArc(sketch, "E41.21.137.0", {"start": v(15.15, 108.13) * mm, "mid": v(14.66, 108.2) * mm, "end": v(14.17, 108.27) * mm});
            skArc(sketch, "E41.25.137.0", {"start": v(15.15, 108.13) * mm, "mid": v(15.37, 108.17) * mm, "end": v(15.54, 108.31) * mm});
            skArc(sketch, "E41.29.137.0", {"start": v(13.84, 108.54) * mm, "mid": v(13.96, 108.36) * mm, "end": v(14.17, 108.27) * mm});
            skLineSegment(sketch, "E41.3.138.0", {"start": v(8.95, 109.05) * mm, "end": v(8.5, 110.3) * mm});
            skPoint(sketch, "E41.6.138.0", {"position": v(8.37, 110.67) * mm});
            skPoint(sketch, "E41.7.138.0", {"position": v(10.53, 108.68) * mm});
            skPoint(sketch, "E41.8.138.0", {"position": v(9.04, 108.81) * mm});
            skPoint(sketch, "E41.9.138.0", {"position": v(11.53, 110.39) * mm});
            skLineSegment(sketch, "E41.10.138.0", {"start": v(10.66, 108.9) * mm, "end": v(11.33, 110.05) * mm});
            skArc(sketch, "E41.13.138.0", {"start": v(8.5, 110.3) * mm, "mid": v(8.3, 110.58) * mm, "end": v(7.98, 110.7) * mm});
            skLineSegment(sketch, "E41.14.138.0", {"start": v(9.79, 108.75) * mm, "end": v(9.95, 110.54) * mm, "construction": true});
            skArc(sketch, "E41.17.138.0", {"start": v(11.91, 110.35) * mm, "mid": v(11.58, 110.29) * mm, "end": v(11.33, 110.05) * mm});
            skArc(sketch, "E41.21.138.0", {"start": v(10.28, 108.7) * mm, "mid": v(9.79, 108.75) * mm, "end": v(9.3, 108.8) * mm});
            skArc(sketch, "E41.25.138.0", {"start": v(10.28, 108.7) * mm, "mid": v(10.5, 108.75) * mm, "end": v(10.66, 108.9) * mm});
            skArc(sketch, "E41.29.138.0", {"start": v(8.95, 109.05) * mm, "mid": v(9.09, 108.87) * mm, "end": v(9.3, 108.8) * mm});
            skLineSegment(sketch, "E41.3.139.0", {"start": v(4.05, 109.35) * mm, "end": v(3.54, 110.58) * mm});
            skPoint(sketch, "E41.6.139.0", {"position": v(3.4, 110.94) * mm});
            skPoint(sketch, "E41.7.139.0", {"position": v(5.65, 109.04) * mm});
            skPoint(sketch, "E41.8.139.0", {"position": v(4.15, 109.1) * mm});
            skPoint(sketch, "E41.9.139.0", {"position": v(6.56, 110.8) * mm});
            skLineSegment(sketch, "E41.10.139.0", {"start": v(5.77, 109.27) * mm, "end": v(6.38, 110.45) * mm});
            skArc(sketch, "E41.13.139.0", {"start": v(3.54, 110.58) * mm, "mid": v(3.33, 110.84) * mm, "end": v(3, 110.95) * mm});
            skLineSegment(sketch, "E41.14.139.0", {"start": v(4.9, 109.08) * mm, "end": v(4.98, 110.88) * mm, "construction": true});
            skArc(sketch, "E41.17.139.0", {"start": v(6.95, 110.77) * mm, "mid": v(6.62, 110.7) * mm, "end": v(6.38, 110.45) * mm});
            skArc(sketch, "E41.21.139.0", {"start": v(5.4, 109.06) * mm, "mid": v(4.9, 109.08) * mm, "end": v(4.4, 109.1) * mm});
            skArc(sketch, "E41.25.139.0", {"start": v(5.4, 109.06) * mm, "mid": v(5.61, 109.1) * mm, "end": v(5.77, 109.27) * mm});
            skArc(sketch, "E41.29.139.0", {"start": v(4.05, 109.35) * mm, "mid": v(4.2, 109.17) * mm, "end": v(4.4, 109.1) * mm});
            skArc(sketch, "E42.trimOffspring", {"start": v(-80.22, 76.7) * mm, "mid": v(-81.39, 75.46) * mm, "end": v(-82.53, 74.21) * mm, "construction": true});
            skArc(sketch, "E43.trimOffspring", {"start": v(-80.22, 76.7) * mm, "mid": v(-81.39, 75.46) * mm, "end": v(-82.53, 74.21) * mm});
            skArc(sketch, "E44.trimOffspring", {"start": v(-83.58, 73.02) * mm, "mid": v(-84.69, 71.74) * mm, "end": v(-85.78, 70.43) * mm, "construction": true});
            skArc(sketch, "E45.trimOffspring", {"start": v(-83.58, 73.02) * mm, "mid": v(-84.69, 71.74) * mm, "end": v(-85.78, 70.43) * mm});
            skArc(sketch, "E46.trimOffspring", {"start": v(-86.77, 69.2) * mm, "mid": v(-87.82, 67.86) * mm, "end": v(-88.85, 66.51) * mm, "construction": true});
            skArc(sketch, "E47.trimOffspring", {"start": v(-86.77, 69.2) * mm, "mid": v(-87.82, 67.86) * mm, "end": v(-88.85, 66.51) * mm});
            skArc(sketch, "E48.trimOffspring", {"start": v(-89.8, 65.24) * mm, "mid": v(-90.78, 63.86) * mm, "end": v(-91.75, 62.46) * mm, "construction": true});
            skArc(sketch, "E49.trimOffspring", {"start": v(-89.8, 65.24) * mm, "mid": v(-90.78, 63.86) * mm, "end": v(-91.75, 62.46) * mm});
            skArc(sketch, "E50.trimOffspring", {"start": v(-92.63, 61.14) * mm, "mid": v(-93.55, 59.72) * mm, "end": v(-94.46, 58.28) * mm, "construction": true});
            skArc(sketch, "E51.trimOffspring", {"start": v(-92.63, 61.14) * mm, "mid": v(-93.55, 59.72) * mm, "end": v(-94.46, 58.28) * mm});
            skArc(sketch, "E52.trimOffspring", {"start": v(-95.28, 56.93) * mm, "mid": v(-96.14, 55.46) * mm, "end": v(-96.97, 53.98) * mm, "construction": true});
            skArc(sketch, "E53.trimOffspring", {"start": v(-95.28, 56.93) * mm, "mid": v(-96.14, 55.46) * mm, "end": v(-96.97, 53.98) * mm});
            skArc(sketch, "E54.trimOffspring", {"start": v(-97.74, 52.6) * mm, "mid": v(-98.44, 51.27) * mm, "end": v(-99.12, 49.93) * mm, "construction": true});
            skArc(sketch, "E55.trimOffspring", {"start": v(-97.74, 52.6) * mm, "mid": v(-98.44, 51.27) * mm, "end": v(-99.12, 49.93) * mm});
            skArc(sketch, "E56.trimOffspring", {"start": v(-100, 48.16) * mm, "mid": v(-100.64, 46.8) * mm, "end": v(-101.26, 45.43) * mm, "construction": true});
            skArc(sketch, "E57.trimOffspring", {"start": v(-100, 48.16) * mm, "mid": v(-100.72, 46.62) * mm, "end": v(-101.42, 45.07) * mm});
            skArc(sketch, "E58.trimOffspring", {"start": v(-102.06, 43.62) * mm, "mid": v(-102.71, 42.05) * mm, "end": v(-103.34, 40.48) * mm, "construction": true});
            skArc(sketch, "E59.trimOffspring", {"start": v(-102.06, 43.62) * mm, "mid": v(-102.64, 42.24) * mm, "end": v(-103.2, 40.84) * mm});
            skArc(sketch, "E60.trimOffspring", {"start": v(-103.91, 39) * mm, "mid": v(-104.43, 37.59) * mm, "end": v(-104.93, 36.17) * mm, "construction": true});
            skArc(sketch, "E61.trimOffspring", {"start": v(-103.91, 39) * mm, "mid": v(-104.5, 37.4) * mm, "end": v(-105.06, 35.8) * mm});
            skArc(sketch, "E62.trimOffspring", {"start": v(-105.56, 34.3) * mm, "mid": v(-106.3, 31.92) * mm, "end": v(-106.99, 29.53) * mm, "construction": true});
            skArc(sketch, "E63.trimOffspring", {"start": v(-105.56, 34.3) * mm, "mid": v(62.4, -91.8) * mm, "end": v(6.95, 110.77) * mm});
            skArc(sketch, "E64.trimOffspring", {"start": v(-107.4, 28) * mm, "mid": v(92.52, -61.3) * mm, "end": v(-67.64, 88) * mm, "construction": true});
            skSolve(sketch);
        }
        {
            var Q0;
            Q0=qSketchRegion(id+"F0",true);
            extrude(context, id + "F1", {"entities" : qUnion([Q0]), "depth" : ((27 / 25.4) / 2) * mm});
        }
        {
            var Q0;
            Q0=makeQuery(id+"F1.opExtrude","CAP_FACE",FACE,{"disambiguationData":[OSD([sQuery(id+"F0.wireOp",EDGE,"E0"),sQuery(id+"F0.wireOp",EDGE,"E1"),sQuery(id+"F0.wireOp",EDGE,"E3"),sQuery(id+"F0.wireOp",EDGE,"E4"),sQuery(id+"F0.wireOp",EDGE,"E6.filletArc"),sQuery(id+"F0.wireOp",EDGE,"E7.filletArc"),sQuery(id+"F0.wireOp",EDGE,"E8.filletArc"),sQuery(id+"F0.wireOp",EDGE,"E9.filletArc"),sQuery(id+"F0.wireOp",EDGE,"E10.1.1"),sQuery(id+"F0.wireOp",EDGE,"E10.1.6"),sQuery(id+"F0.wireOp",EDGE,"E10.1.7"),sQuery(id+"F0.wireOp",EDGE,"E10.1.8"),sQuery(id+"F0.wireOp",EDGE,"E10.1.9"),sQuery(id+"F0.wireOp",EDGE,"E10.1.10"),sQuery(id+"F0.wireOp",EDGE,"E10.1.11"),sQuery(id+"F0.wireOp",EDGE,"E10.2.1"),sQuery(id+"F0.wireOp",EDGE,"E10.2.6"),sQuery(id+"F0.wireOp",EDGE,"E10.2.7"),sQuery(id+"F0.wireOp",EDGE,"E10.2.8"),sQuery(id+"F0.wireOp",EDGE,"E10.2.9"),sQuery(id+"F0.wireOp",EDGE,"E10.2.10"),sQuery(id+"F0.wireOp",EDGE,"E10.2.11"),sQuery(id+"F0.wireOp",EDGE,"E10.3.1"),sQuery(id+"F0.wireOp",EDGE,"E10.3.6"),sQuery(id+"F0.wireOp",EDGE,"E10.3.7"),sQuery(id+"F0.wireOp",EDGE,"E10.3.8"),sQuery(id+"F0.wireOp",EDGE,"E10.3.9"),sQuery(id+"F0.wireOp",EDGE,"E10.3.10"),sQuery(id+"F0.wireOp",EDGE,"E10.3.11"),sQuery(id+"F0.wireOp",EDGE,"E10.4.1"),sQuery(id+"F0.wireOp",EDGE,"E10.4.6"),sQuery(id+"F0.wireOp",EDGE,"E10.4.7"),sQuery(id+"F0.wireOp",EDGE,"E10.4.8"),sQuery(id+"F0.wireOp",EDGE,"E10.4.9"),sQuery(id+"F0.wireOp",EDGE,"E10.4.10"),sQuery(id+"F0.wireOp",EDGE,"E10.4.11"),sQuery(id+"F0.wireOp",EDGE,"E10.5.1"),sQuery(id+"F0.wireOp",EDGE,"E10.5.6"),sQuery(id+"F0.wireOp",EDGE,"E10.5.7"),sQuery(id+"F0.wireOp",EDGE,"E10.5.8"),sQuery(id+"F0.wireOp",EDGE,"E10.5.9"),sQuery(id+"F0.wireOp",EDGE,"E10.5.10"),sQuery(id+"F0.wireOp",EDGE,"E10.5.11"),sQuery(id+"F0.wireOp",EDGE,"E10.6.1"),sQuery(id+"F0.wireOp",EDGE,"E10.6.6"),sQuery(id+"F0.wireOp",EDGE,"E10.6.7"),sQuery(id+"F0.wireOp",EDGE,"E10.6.8"),sQuery(id+"F0.wireOp",EDGE,"E10.6.9"),sQuery(id+"F0.wireOp",EDGE,"E10.6.10"),sQuery(id+"F0.wireOp",EDGE,"E10.6.11"),sQuery(id+"F0.wireOp",EDGE,"E10.7.1"),sQuery(id+"F0.wireOp",EDGE,"E10.7.6"),sQuery(id+"F0.wireOp",EDGE,"E10.7.7"),sQuery(id+"F0.wireOp",EDGE,"E10.7.8"),sQuery(id+"F0.wireOp",EDGE,"E10.7.9"),sQuery(id+"F0.wireOp",EDGE,"E10.7.10"),sQuery(id+"F0.wireOp",EDGE,"E10.7.11"),sQuery(id+"F0.wireOp",EDGE,"E10.8.1"),sQuery(id+"F0.wireOp",EDGE,"E10.8.6"),sQuery(id+"F0.wireOp",EDGE,"E10.8.7"),sQuery(id+"F0.wireOp",EDGE,"E10.8.8"),sQuery(id+"F0.wireOp",EDGE,"E10.8.9"),sQuery(id+"F0.wireOp",EDGE,"E10.8.10"),sQuery(id+"F0.wireOp",EDGE,"E10.8.11"),sQuery(id+"F0.wireOp",EDGE,"E10.9.1"),sQuery(id+"F0.wireOp",EDGE,"E10.9.6"),sQuery(id+"F0.wireOp",EDGE,"E10.9.7"),sQuery(id+"F0.wireOp",EDGE,"E10.9.8"),sQuery(id+"F0.wireOp",EDGE,"E10.9.9"),sQuery(id+"F0.wireOp",EDGE,"E10.9.10"),sQuery(id+"F0.wireOp",EDGE,"E10.9.11"),sQuery(id+"F0.wireOp",EDGE,"E10.10.1"),sQuery(id+"F0.wireOp",EDGE,"E10.10.6"),sQuery(id+"F0.wireOp",EDGE,"E10.10.7"),sQuery(id+"F0.wireOp",EDGE,"E10.10.8"),sQuery(id+"F0.wireOp",EDGE,"E10.10.9"),sQuery(id+"F0.wireOp",EDGE,"E10.10.10"),sQuery(id+"F0.wireOp",EDGE,"E10.10.11"),sQuery(id+"F0.wireOp",EDGE,"E10.11.1"),sQuery(id+"F0.wireOp",EDGE,"E10.11.6"),sQuery(id+"F0.wireOp",EDGE,"E10.11.7"),sQuery(id+"F0.wireOp",EDGE,"E10.11.8"),sQuery(id+"F0.wireOp",EDGE,"E10.11.9"),sQuery(id+"F0.wireOp",EDGE,"E10.11.10"),sQuery(id+"F0.wireOp",EDGE,"E10.11.11"),sQuery(id+"F0.wireOp",EDGE,"E10.12.1"),sQuery(id+"F0.wireOp",EDGE,"E10.12.6"),sQuery(id+"F0.wireOp",EDGE,"E10.12.7"),sQuery(id+"F0.wireOp",EDGE,"E10.12.8"),sQuery(id+"F0.wireOp",EDGE,"E10.12.9"),sQuery(id+"F0.wireOp",EDGE,"E10.12.10"),sQuery(id+"F0.wireOp",EDGE,"E10.12.11"),sQuery(id+"F0.wireOp",EDGE,"E10.13.1"),sQuery(id+"F0.wireOp",EDGE,"E10.13.6"),sQuery(id+"F0.wireOp",EDGE,"E10.13.7"),sQuery(id+"F0.wireOp",EDGE,"E10.13.8"),sQuery(id+"F0.wireOp",EDGE,"E10.13.9"),sQuery(id+"F0.wireOp",EDGE,"E10.13.10"),sQuery(id+"F0.wireOp",EDGE,"E10.13.11"),sQuery(id+"F0.wireOp",EDGE,"E10.14.1"),sQuery(id+"F0.wireOp",EDGE,"E10.14.6"),sQuery(id+"F0.wireOp",EDGE,"E10.14.7"),sQuery(id+"F0.wireOp",EDGE,"E10.14.8"),sQuery(id+"F0.wireOp",EDGE,"E10.14.9"),sQuery(id+"F0.wireOp",EDGE,"E10.14.10"),sQuery(id+"F0.wireOp",EDGE,"E10.14.11"),sQuery(id+"F0.wireOp",EDGE,"E10.15.1"),sQuery(id+"F0.wireOp",EDGE,"E10.15.6"),sQuery(id+"F0.wireOp",EDGE,"E10.15.7"),sQuery(id+"F0.wireOp",EDGE,"E10.15.8"),sQuery(id+"F0.wireOp",EDGE,"E10.15.9"),sQuery(id+"F0.wireOp",EDGE,"E10.15.10"),sQuery(id+"F0.wireOp",EDGE,"E10.15.11"),sQuery(id+"F0.wireOp",EDGE,"E11.trimOffspring"),sQuery(id+"F0.wireOp",EDGE,"E12.trimOffspring"),sQuery(id+"F0.wireOp",EDGE,"E13.trimOffspring"),sQuery(id+"F0.wireOp",EDGE,"E14.trimOffspring"),sQuery(id+"F0.wireOp",EDGE,"E15.trimOffspring"),sQuery(id+"F0.wireOp",EDGE,"E16.trimOffspring"),sQuery(id+"F0.wireOp",EDGE,"E17.trimOffspring"),sQuery(id+"F0.wireOp",EDGE,"E18.trimOffspring"),sQuery(id+"F0.wireOp",EDGE,"E19.trimOffspring"),sQuery(id+"F0.wireOp",EDGE,"E20.trimOffspring"),sQuery(id+"F0.wireOp",EDGE,"E21.trimOffspring"),sQuery(id+"F0.wireOp",EDGE,"E22.trimOffspring"),sQuery(id+"F0.wireOp",EDGE,"E23.trimOffspring"),sQuery(id+"F0.wireOp",EDGE,"E24.trimOffspring"),sQuery(id+"F0.wireOp",EDGE,"E25.trimOffspring")])],"isStart":false});
            var sketch = newSketch(context, id + "F2", { "sketchPlane" : qUnion([Q0])});
            skCircle(sketch, "E65", {"center": v(0, 0) * mm, "radius": 114.69 * mm});
            skLineSegment(sketch, "E66", {"start": v(0, 0) * mm, "end": v(2.5, 110.96) * mm, "construction": true});
            skLineSegment(sketch, "E67", {"start": v(2.5, 110.96) * mm, "end": v(2.57, 114.66) * mm, "construction": true});
            skSolve(sketch);
        }
        {
            var Q0;
            Q0=qSketchRegion(id+"F2",true);
            extrude(context, id + "F3", {"entities" : qUnion([Q0]), "operationType" : NewBodyOperationType.ADD, "depth" : 12.7 * mm});
        }
        {
            var Q0;
            Q0=makeQuery(id+"F3.opExtrude","CAP_EDGE",EDGE,{"disambiguationData":[OSD([sQuery(id+"F2.wireOp",EDGE,"E65")])],"isStart":true});
            var Q1;
            Q1=makeQuery(id+"F3.opExtrude","CAP_EDGE",EDGE,{"disambiguationData":[OSD([sQuery(id+"F2.wireOp",EDGE,"E65")])],"isStart":false});
            chamfer(context, id + "F4", {"entities" : qUnion([Q0, Q1]), "chamferType" : ChamferType.TWO_OFFSETS, "width1" : 1.52 * mm, "oppositeDirection" : false, "width2" : 3.05 * mm, "tangentPropagation" : true});
        }
        {
            var Q0;
            Q0=makeQuery(id+"F1.opExtrude","CAP_FACE",FACE,{"disambiguationData":[OSD([sQuery(id+"F0.wireOp",EDGE,"E0"),sQuery(id+"F0.wireOp",EDGE,"E1"),sQuery(id+"F0.wireOp",EDGE,"E3"),sQuery(id+"F0.wireOp",EDGE,"E4"),sQuery(id+"F0.wireOp",EDGE,"E6.filletArc"),sQuery(id+"F0.wireOp",EDGE,"E7.filletArc"),sQuery(id+"F0.wireOp",EDGE,"E8.filletArc"),sQuery(id+"F0.wireOp",EDGE,"E9.filletArc"),sQuery(id+"F0.wireOp",EDGE,"E10.1.1"),sQuery(id+"F0.wireOp",EDGE,"E10.1.6"),sQuery(id+"F0.wireOp",EDGE,"E10.1.7"),sQuery(id+"F0.wireOp",EDGE,"E10.1.8"),sQuery(id+"F0.wireOp",EDGE,"E10.1.9"),sQuery(id+"F0.wireOp",EDGE,"E10.1.10"),sQuery(id+"F0.wireOp",EDGE,"E10.1.11"),sQuery(id+"F0.wireOp",EDGE,"E10.2.1"),sQuery(id+"F0.wireOp",EDGE,"E10.2.6"),sQuery(id+"F0.wireOp",EDGE,"E10.2.7"),sQuery(id+"F0.wireOp",EDGE,"E10.2.8"),sQuery(id+"F0.wireOp",EDGE,"E10.2.9"),sQuery(id+"F0.wireOp",EDGE,"E10.2.10"),sQuery(id+"F0.wireOp",EDGE,"E10.2.11"),sQuery(id+"F0.wireOp",EDGE,"E10.3.1"),sQuery(id+"F0.wireOp",EDGE,"E10.3.6"),sQuery(id+"F0.wireOp",EDGE,"E10.3.7"),sQuery(id+"F0.wireOp",EDGE,"E10.3.8"),sQuery(id+"F0.wireOp",EDGE,"E10.3.9"),sQuery(id+"F0.wireOp",EDGE,"E10.3.10"),sQuery(id+"F0.wireOp",EDGE,"E10.3.11"),sQuery(id+"F0.wireOp",EDGE,"E10.4.1"),sQuery(id+"F0.wireOp",EDGE,"E10.4.6"),sQuery(id+"F0.wireOp",EDGE,"E10.4.7"),sQuery(id+"F0.wireOp",EDGE,"E10.4.8"),sQuery(id+"F0.wireOp",EDGE,"E10.4.9"),sQuery(id+"F0.wireOp",EDGE,"E10.4.10"),sQuery(id+"F0.wireOp",EDGE,"E10.4.11"),sQuery(id+"F0.wireOp",EDGE,"E10.5.1"),sQuery(id+"F0.wireOp",EDGE,"E10.5.6"),sQuery(id+"F0.wireOp",EDGE,"E10.5.7"),sQuery(id+"F0.wireOp",EDGE,"E10.5.8"),sQuery(id+"F0.wireOp",EDGE,"E10.5.9"),sQuery(id+"F0.wireOp",EDGE,"E10.5.10"),sQuery(id+"F0.wireOp",EDGE,"E10.5.11"),sQuery(id+"F0.wireOp",EDGE,"E10.6.1"),sQuery(id+"F0.wireOp",EDGE,"E10.6.6"),sQuery(id+"F0.wireOp",EDGE,"E10.6.7"),sQuery(id+"F0.wireOp",EDGE,"E10.6.8"),sQuery(id+"F0.wireOp",EDGE,"E10.6.9"),sQuery(id+"F0.wireOp",EDGE,"E10.6.10"),sQuery(id+"F0.wireOp",EDGE,"E10.6.11"),sQuery(id+"F0.wireOp",EDGE,"E10.7.1"),sQuery(id+"F0.wireOp",EDGE,"E10.7.6"),sQuery(id+"F0.wireOp",EDGE,"E10.7.7"),sQuery(id+"F0.wireOp",EDGE,"E10.7.8"),sQuery(id+"F0.wireOp",EDGE,"E10.7.9"),sQuery(id+"F0.wireOp",EDGE,"E10.7.10"),sQuery(id+"F0.wireOp",EDGE,"E10.7.11"),sQuery(id+"F0.wireOp",EDGE,"E10.8.1"),sQuery(id+"F0.wireOp",EDGE,"E10.8.6"),sQuery(id+"F0.wireOp",EDGE,"E10.8.7"),sQuery(id+"F0.wireOp",EDGE,"E10.8.8"),sQuery(id+"F0.wireOp",EDGE,"E10.8.9"),sQuery(id+"F0.wireOp",EDGE,"E10.8.10"),sQuery(id+"F0.wireOp",EDGE,"E10.8.11"),sQuery(id+"F0.wireOp",EDGE,"E10.9.1"),sQuery(id+"F0.wireOp",EDGE,"E10.9.6"),sQuery(id+"F0.wireOp",EDGE,"E10.9.7"),sQuery(id+"F0.wireOp",EDGE,"E10.9.8"),sQuery(id+"F0.wireOp",EDGE,"E10.9.9"),sQuery(id+"F0.wireOp",EDGE,"E10.9.10"),sQuery(id+"F0.wireOp",EDGE,"E10.9.11"),sQuery(id+"F0.wireOp",EDGE,"E10.10.1"),sQuery(id+"F0.wireOp",EDGE,"E10.10.6"),sQuery(id+"F0.wireOp",EDGE,"E10.10.7"),sQuery(id+"F0.wireOp",EDGE,"E10.10.8"),sQuery(id+"F0.wireOp",EDGE,"E10.10.9"),sQuery(id+"F0.wireOp",EDGE,"E10.10.10"),sQuery(id+"F0.wireOp",EDGE,"E10.10.11"),sQuery(id+"F0.wireOp",EDGE,"E10.11.1"),sQuery(id+"F0.wireOp",EDGE,"E10.11.6"),sQuery(id+"F0.wireOp",EDGE,"E10.11.7"),sQuery(id+"F0.wireOp",EDGE,"E10.11.8"),sQuery(id+"F0.wireOp",EDGE,"E10.11.9"),sQuery(id+"F0.wireOp",EDGE,"E10.11.10"),sQuery(id+"F0.wireOp",EDGE,"E10.11.11"),sQuery(id+"F0.wireOp",EDGE,"E10.12.1"),sQuery(id+"F0.wireOp",EDGE,"E10.12.6"),sQuery(id+"F0.wireOp",EDGE,"E10.12.7"),sQuery(id+"F0.wireOp",EDGE,"E10.12.8"),sQuery(id+"F0.wireOp",EDGE,"E10.12.9"),sQuery(id+"F0.wireOp",EDGE,"E10.12.10"),sQuery(id+"F0.wireOp",EDGE,"E10.12.11"),sQuery(id+"F0.wireOp",EDGE,"E10.13.1"),sQuery(id+"F0.wireOp",EDGE,"E10.13.6"),sQuery(id+"F0.wireOp",EDGE,"E10.13.7"),sQuery(id+"F0.wireOp",EDGE,"E10.13.8"),sQuery(id+"F0.wireOp",EDGE,"E10.13.9"),sQuery(id+"F0.wireOp",EDGE,"E10.13.10"),sQuery(id+"F0.wireOp",EDGE,"E10.13.11"),sQuery(id+"F0.wireOp",EDGE,"E10.14.1"),sQuery(id+"F0.wireOp",EDGE,"E10.14.6"),sQuery(id+"F0.wireOp",EDGE,"E10.14.7"),sQuery(id+"F0.wireOp",EDGE,"E10.14.8"),sQuery(id+"F0.wireOp",EDGE,"E10.14.9"),sQuery(id+"F0.wireOp",EDGE,"E10.14.10"),sQuery(id+"F0.wireOp",EDGE,"E10.14.11"),sQuery(id+"F0.wireOp",EDGE,"E10.15.1"),sQuery(id+"F0.wireOp",EDGE,"E10.15.6"),sQuery(id+"F0.wireOp",EDGE,"E10.15.7"),sQuery(id+"F0.wireOp",EDGE,"E10.15.8"),sQuery(id+"F0.wireOp",EDGE,"E10.15.9"),sQuery(id+"F0.wireOp",EDGE,"E10.15.10"),sQuery(id+"F0.wireOp",EDGE,"E10.15.11"),sQuery(id+"F0.wireOp",EDGE,"E11.trimOffspring"),sQuery(id+"F0.wireOp",EDGE,"E12.trimOffspring"),sQuery(id+"F0.wireOp",EDGE,"E13.trimOffspring"),sQuery(id+"F0.wireOp",EDGE,"E14.trimOffspring"),sQuery(id+"F0.wireOp",EDGE,"E15.trimOffspring"),sQuery(id+"F0.wireOp",EDGE,"E16.trimOffspring"),sQuery(id+"F0.wireOp",EDGE,"E17.trimOffspring"),sQuery(id+"F0.wireOp",EDGE,"E18.trimOffspring"),sQuery(id+"F0.wireOp",EDGE,"E19.trimOffspring"),sQuery(id+"F0.wireOp",EDGE,"E20.trimOffspring"),sQuery(id+"F0.wireOp",EDGE,"E21.trimOffspring"),sQuery(id+"F0.wireOp",EDGE,"E22.trimOffspring"),sQuery(id+"F0.wireOp",EDGE,"E23.trimOffspring"),sQuery(id+"F0.wireOp",EDGE,"E24.trimOffspring"),sQuery(id+"F0.wireOp",EDGE,"E25.trimOffspring")])],"isStart":true});
            var sketch = newSketch(context, id + "F5", { "sketchPlane" : qUnion([Q0])});
            skCircle(sketch, "E68", {"center": v(0, 0) * mm, "radius": 3.05 * mm});
            skSolve(sketch);
        }
        {
            var Q0;
            Q0=qSketchRegion(id+"F5",true);
            extrude(context, id + "F6", {"entities" : qUnion([Q0]), "operationType" : NewBodyOperationType.REMOVE, "endBound" : BoundingType.THROUGH_ALL, "oppositeDirection" : true, "depth" : 25.4 * mm});
        }
        {
            var Q0;
            Q0=makeQuery(id+"F3.opExtrude","CAP_FACE",FACE,{"disambiguationData":[OSD([sQuery(id+"F2.wireOp",EDGE,"E65")])],"isStart":false});
            var sketch = newSketch(context, id + "F7", { "sketchPlane" : qUnion([Q0])});
            skCircle(sketch, "E69", {"center": v(0, 7.88) * mm, "radius": 1.73 * mm});
            skCircle(sketch, "E70", {"center": v(-7.88, 0) * mm, "radius": 1.73 * mm});
            skCircle(sketch, "E71", {"center": v(0, -7.88) * mm, "radius": 1.73 * mm});
            skCircle(sketch, "E72", {"center": v(7.88, 0) * mm, "radius": 1.73 * mm});
            skCircle(sketch, "E73", {"center": v(0, 0) * mm, "radius": 7.88 * mm, "construction": true});
            skSolve(sketch);
        }
        {
            var Q0;
            Q0=qSketchRegion(id+"F7",true);
            extrude(context, id + "F8", {"entities" : qUnion([Q0]), "operationType" : NewBodyOperationType.REMOVE, "endBound" : BoundingType.THROUGH_ALL, "oppositeDirection" : true, "depth" : 25.4 * mm});
        }
        {
            var Q0;
            Q0=makeQuery(id+"F3.opExtrude","CAP_FACE",FACE,{"disambiguationData":[OSD([sQuery(id+"F2.wireOp",EDGE,"E65")])],"isStart":false});
            var sketch = newSketch(context, id + "F9", { "sketchPlane" : qUnion([Q0])});
            skLineSegment(sketch, "E74", {"start": v(0, 11.32) * mm, "end": v(-11.32, 0) * mm});
            skLineSegment(sketch, "E75", {"start": v(-11.32, 0) * mm, "end": v(0, -11.32) * mm});
            skLineSegment(sketch, "E76", {"start": v(0, -11.32) * mm, "end": v(11.32, 0) * mm});
            skLineSegment(sketch, "E77", {"start": v(11.32, 0) * mm, "end": v(0, 11.32) * mm});
            skSolve(sketch);
        }
        {
            var Q0;
            Q0=qSketchRegion(id+"F9",true);
            extrude(context, id + "F10", {"entities" : qUnion([Q0]), "operationType" : NewBodyOperationType.REMOVE, "oppositeDirection" : true, "depth" : 7 * mm});
        }
        {
            var Q0;
            Q0=makeQuery(id+"F10.boolean.opBoolean","COPY",FACE,{"derivedFrom":makeQuery(id+"F10.opExtrude","SWEPT_FACE",FACE,{"disambiguationData":[OSD([sQuery(id+"F9.wireOp",EDGE,"E75")])]})});
            var sketch = newSketch(context, id + "F11", { "sketchPlane" : qUnion([Q0])});
            skArc(sketch, "E78", {"start": v(-22.7, -2.54) * mm, "mid": v(-20.16, 0) * mm, "end": v(-22.7, 2.54) * mm});
            skLineSegment(sketch, "E79", {"start": v(-22.7, 2.54) * mm, "end": v(-26.2, 2.54) * mm});
            skLineSegment(sketch, "E80", {"start": v(-26.2, 2.54) * mm, "end": v(-26.2, -2.54) * mm});
            skLineSegment(sketch, "E81", {"start": v(-26.2, -2.54) * mm, "end": v(-22.7, -2.54) * mm});
            skSolve(sketch);
        }
        {
            var Q0;
            Q0=makeQuery(id+"F11.imprint","IMPRINT",FACE,{"disambiguationData":[TD([[makeQuery(id+"F11.imprint","IMPRINT",EDGE,{"derivedFrom":sQuery(id+"F11.wireOp",EDGE,"E78")}),1.0]])]});
            extrude(context, id + "F12", {"entities" : qUnion([Q0]), "operationType" : NewBodyOperationType.REMOVE, "endBound" : BoundingType.THROUGH_ALL, "oppositeDirection" : true, "depth" : 25.4 * mm});
        }
        {
            var Q0;
            Q0=makeQuery(id+"F1.opExtrude","SWEPT_BODY",BODY,{"disambiguationData":[OSD([sQuery(id+"F0.wireOp",EDGE,"E0"),sQuery(id+"F0.wireOp",EDGE,"E1"),sQuery(id+"F0.wireOp",EDGE,"E3"),sQuery(id+"F0.wireOp",EDGE,"E4"),sQuery(id+"F0.wireOp",EDGE,"E6.filletArc"),sQuery(id+"F0.wireOp",EDGE,"E7.filletArc"),sQuery(id+"F0.wireOp",EDGE,"E8.filletArc"),sQuery(id+"F0.wireOp",EDGE,"E9.filletArc"),sQuery(id+"F0.wireOp",EDGE,"E10.1.1"),sQuery(id+"F0.wireOp",EDGE,"E10.1.6"),sQuery(id+"F0.wireOp",EDGE,"E10.1.7"),sQuery(id+"F0.wireOp",EDGE,"E10.1.8"),sQuery(id+"F0.wireOp",EDGE,"E10.1.9"),sQuery(id+"F0.wireOp",EDGE,"E10.1.10"),sQuery(id+"F0.wireOp",EDGE,"E10.1.11"),sQuery(id+"F0.wireOp",EDGE,"E10.2.1"),sQuery(id+"F0.wireOp",EDGE,"E10.2.6"),sQuery(id+"F0.wireOp",EDGE,"E10.2.7"),sQuery(id+"F0.wireOp",EDGE,"E10.2.8"),sQuery(id+"F0.wireOp",EDGE,"E10.2.9"),sQuery(id+"F0.wireOp",EDGE,"E10.2.10"),sQuery(id+"F0.wireOp",EDGE,"E10.2.11"),sQuery(id+"F0.wireOp",EDGE,"E10.3.1"),sQuery(id+"F0.wireOp",EDGE,"E10.3.6"),sQuery(id+"F0.wireOp",EDGE,"E10.3.7"),sQuery(id+"F0.wireOp",EDGE,"E10.3.8"),sQuery(id+"F0.wireOp",EDGE,"E10.3.9"),sQuery(id+"F0.wireOp",EDGE,"E10.3.10"),sQuery(id+"F0.wireOp",EDGE,"E10.3.11"),sQuery(id+"F0.wireOp",EDGE,"E10.4.1"),sQuery(id+"F0.wireOp",EDGE,"E10.4.6"),sQuery(id+"F0.wireOp",EDGE,"E10.4.7"),sQuery(id+"F0.wireOp",EDGE,"E10.4.8"),sQuery(id+"F0.wireOp",EDGE,"E10.4.9"),sQuery(id+"F0.wireOp",EDGE,"E10.4.10"),sQuery(id+"F0.wireOp",EDGE,"E10.4.11"),sQuery(id+"F0.wireOp",EDGE,"E10.5.1"),sQuery(id+"F0.wireOp",EDGE,"E10.5.6"),sQuery(id+"F0.wireOp",EDGE,"E10.5.7"),sQuery(id+"F0.wireOp",EDGE,"E10.5.8"),sQuery(id+"F0.wireOp",EDGE,"E10.5.9"),sQuery(id+"F0.wireOp",EDGE,"E10.5.10"),sQuery(id+"F0.wireOp",EDGE,"E10.5.11"),sQuery(id+"F0.wireOp",EDGE,"E10.6.1"),sQuery(id+"F0.wireOp",EDGE,"E10.6.6"),sQuery(id+"F0.wireOp",EDGE,"E10.6.7"),sQuery(id+"F0.wireOp",EDGE,"E10.6.8"),sQuery(id+"F0.wireOp",EDGE,"E10.6.9"),sQuery(id+"F0.wireOp",EDGE,"E10.6.10"),sQuery(id+"F0.wireOp",EDGE,"E10.6.11"),sQuery(id+"F0.wireOp",EDGE,"E10.7.1"),sQuery(id+"F0.wireOp",EDGE,"E10.7.6"),sQuery(id+"F0.wireOp",EDGE,"E10.7.7"),sQuery(id+"F0.wireOp",EDGE,"E10.7.8"),sQuery(id+"F0.wireOp",EDGE,"E10.7.9"),sQuery(id+"F0.wireOp",EDGE,"E10.7.10"),sQuery(id+"F0.wireOp",EDGE,"E10.7.11"),sQuery(id+"F0.wireOp",EDGE,"E10.8.1"),sQuery(id+"F0.wireOp",EDGE,"E10.8.6"),sQuery(id+"F0.wireOp",EDGE,"E10.8.7"),sQuery(id+"F0.wireOp",EDGE,"E10.8.8"),sQuery(id+"F0.wireOp",EDGE,"E10.8.9"),sQuery(id+"F0.wireOp",EDGE,"E10.8.10"),sQuery(id+"F0.wireOp",EDGE,"E10.8.11"),sQuery(id+"F0.wireOp",EDGE,"E10.9.1"),sQuery(id+"F0.wireOp",EDGE,"E10.9.6"),sQuery(id+"F0.wireOp",EDGE,"E10.9.7"),sQuery(id+"F0.wireOp",EDGE,"E10.9.8"),sQuery(id+"F0.wireOp",EDGE,"E10.9.9"),sQuery(id+"F0.wireOp",EDGE,"E10.9.10"),sQuery(id+"F0.wireOp",EDGE,"E10.9.11"),sQuery(id+"F0.wireOp",EDGE,"E10.10.1"),sQuery(id+"F0.wireOp",EDGE,"E10.10.6"),sQuery(id+"F0.wireOp",EDGE,"E10.10.7"),sQuery(id+"F0.wireOp",EDGE,"E10.10.8"),sQuery(id+"F0.wireOp",EDGE,"E10.10.9"),sQuery(id+"F0.wireOp",EDGE,"E10.10.10"),sQuery(id+"F0.wireOp",EDGE,"E10.10.11"),sQuery(id+"F0.wireOp",EDGE,"E10.11.1"),sQuery(id+"F0.wireOp",EDGE,"E10.11.6"),sQuery(id+"F0.wireOp",EDGE,"E10.11.7"),sQuery(id+"F0.wireOp",EDGE,"E10.11.8"),sQuery(id+"F0.wireOp",EDGE,"E10.11.9"),sQuery(id+"F0.wireOp",EDGE,"E10.11.10"),sQuery(id+"F0.wireOp",EDGE,"E10.11.11"),sQuery(id+"F0.wireOp",EDGE,"E10.12.1"),sQuery(id+"F0.wireOp",EDGE,"E10.12.6"),sQuery(id+"F0.wireOp",EDGE,"E10.12.7"),sQuery(id+"F0.wireOp",EDGE,"E10.12.8"),sQuery(id+"F0.wireOp",EDGE,"E10.12.9"),sQuery(id+"F0.wireOp",EDGE,"E10.12.10"),sQuery(id+"F0.wireOp",EDGE,"E10.12.11"),sQuery(id+"F0.wireOp",EDGE,"E10.13.1"),sQuery(id+"F0.wireOp",EDGE,"E10.13.6"),sQuery(id+"F0.wireOp",EDGE,"E10.13.7"),sQuery(id+"F0.wireOp",EDGE,"E10.13.8"),sQuery(id+"F0.wireOp",EDGE,"E10.13.9"),sQuery(id+"F0.wireOp",EDGE,"E10.13.10"),sQuery(id+"F0.wireOp",EDGE,"E10.13.11"),sQuery(id+"F0.wireOp",EDGE,"E10.14.1"),sQuery(id+"F0.wireOp",EDGE,"E10.14.6"),sQuery(id+"F0.wireOp",EDGE,"E10.14.7"),sQuery(id+"F0.wireOp",EDGE,"E10.14.8"),sQuery(id+"F0.wireOp",EDGE,"E10.14.9"),sQuery(id+"F0.wireOp",EDGE,"E10.14.10"),sQuery(id+"F0.wireOp",EDGE,"E10.14.11"),sQuery(id+"F0.wireOp",EDGE,"E10.15.1"),sQuery(id+"F0.wireOp",EDGE,"E10.15.6"),sQuery(id+"F0.wireOp",EDGE,"E10.15.7"),sQuery(id+"F0.wireOp",EDGE,"E10.15.8"),sQuery(id+"F0.wireOp",EDGE,"E10.15.9"),sQuery(id+"F0.wireOp",EDGE,"E10.15.10"),sQuery(id+"F0.wireOp",EDGE,"E10.15.11"),sQuery(id+"F0.wireOp",EDGE,"E11.trimOffspring"),sQuery(id+"F0.wireOp",EDGE,"E12.trimOffspring"),sQuery(id+"F0.wireOp",EDGE,"E13.trimOffspring"),sQuery(id+"F0.wireOp",EDGE,"E14.trimOffspring"),sQuery(id+"F0.wireOp",EDGE,"E15.trimOffspring"),sQuery(id+"F0.wireOp",EDGE,"E16.trimOffspring"),sQuery(id+"F0.wireOp",EDGE,"E17.trimOffspring"),sQuery(id+"F0.wireOp",EDGE,"E18.trimOffspring"),sQuery(id+"F0.wireOp",EDGE,"E19.trimOffspring"),sQuery(id+"F0.wireOp",EDGE,"E20.trimOffspring"),sQuery(id+"F0.wireOp",EDGE,"E21.trimOffspring"),sQuery(id+"F0.wireOp",EDGE,"E22.trimOffspring"),sQuery(id+"F0.wireOp",EDGE,"E23.trimOffspring"),sQuery(id+"F0.wireOp",EDGE,"E24.trimOffspring"),sQuery(id+"F0.wireOp",EDGE,"E25.trimOffspring")])]});
            var Q1;
            Q1=qCreatedBy(makeId("Front.planeOp"),FACE);
            mirror(context, id + "F13", {"operationType" : NewBodyOperationType.ADD, "entities" : qUnion([Q0]), "mirrorPlane" : qUnion([Q1])});
        }
        {
            var Q0;
            Q0=qCreatedBy(makeId("Top.planeOp"),FACE);
            cPlane(context, id + "F14", {"entities" : qUnion([Q0]), "cplaneType" : CPlaneType.OFFSET, "offset" : 11.43 * mm, "width" : 152.4 * mm, "height" : 152.4 * mm});
        }
        {
            var Q0;
            Q0=qCreatedBy(id+"F14.planeOp",FACE);
            var sketch = newSketch(context, id + "F15", { "sketchPlane" : qUnion([Q0])});
            skCircle(sketch, "E82", {"center": v(0, -19.85) * mm, "radius": 3.17 * mm});
            skCircle(sketch, "E83", {"center": v(0, 20.35) * mm, "radius": 3.18 * mm});
            skSolve(sketch);
        }
        {
            var Q0;
            Q0 = qSketchRegion(id + "F15", true);
            extrude(context, id + "F16", {"entities" : qUnion([Q0]), "operationType" : NewBodyOperationType.REMOVE, "endBound" : BoundingType.THROUGH_ALL, "depth" : 25.4 * mm});
        }
        {
            var Q0;
            Q0=qCreatedBy(makeId("Top.planeOp"),FACE);
            cPlane(context, id + "F17", {"entities" : qUnion([Q0]), "cplaneType" : CPlaneType.OFFSET, "offset" : 11.43 * mm, "oppositeDirection" : true, "width" : 152.4 * mm, "height" : 152.4 * mm});
        }
        {
            var Q0;
            Q0=qCreatedBy(id+"F17.planeOp",FACE);
            var sketch = newSketch(context, id + "F18", { "sketchPlane" : qUnion([Q0])});
            skCircle(sketch, "E84", {"center": v(0, -19.85) * mm, "radius": 3.18 * mm});
            skCircle(sketch, "E85", {"center": v(0, 19.85) * mm, "radius": 3.18 * mm});
            skSolve(sketch);
        }
        {
            var Q0;
            Q0 = qSketchRegion(id + "F18", true);
            extrude(context, id + "F19", {"entities" : qUnion([Q0]), "operationType" : NewBodyOperationType.REMOVE, "endBound" : BoundingType.THROUGH_ALL, "oppositeDirection" : true, "depth" : 25.4 * mm});
        }
    });
